FCSTD DOCUMENT  (FreeCAD 0.15R4649 (Git))
Label: PrintBot_EvolutionV1.0
License: CC-BY 3.0
LicenseURL: http://creativecommons.org/licenses/by/3.0/
objects: Part::Feature×190, Part::MultiFuse×45, Part::Cylinder×44, Sketcher::SketchObject×39, Part::Box×37, Part::Cut×34, App::DocumentObjectGroup×32, Part::Fillet×26, PartDesign::Pad×21, PartDesign::Pocket×12, Part::Chamfer×8, PartDesign::Revolution×6, Part::Compound×5, Part::Sphere×4, Part::Torus×4, Mesh::Feature×2, PartDesign::PolarPattern×1, Part::Extrusion×1, PartDesign::Mirrored×1
note: 517 computed .brp shape members not serialized (recipe doc carries the construction recipe); baked Part::Feature solids carry a one-line shape summary decoded from their .brp

FEATURE [Part::Compound] Compound  label="bottom-screws"
FEATURE [Part::Feature] Chamfer  label="shaft"
  Placement = pos=(10.55,0,41.9) rot=(0,0,1;0rad)
  shape: bbox 6 x 6 x 4.4 mm, 90 faces (baked)
FEATURE [Part::MultiFuse] Fusion  label="wires"
  Placement = pos=(20.55,0,6.35) rot=(0,0,1;0rad)
FEATURE [Part::MultiFuse] Fusion001  label="servo-1"
FEATURE [Part::Compound] Compound001  label="Servo-SM-S4303R_1"
  Links = -> [Chamfer,Fusion001,Fusion,Compound]
  Placement = pos=(9,-4,13.5) rot=(1,0,0;1.5708rad)
FEATURE [Part::MultiFuse] Fusion002  label="wires001"
  Placement = pos=(20.55,0,6.35) rot=(0,0,1;0rad)
FEATURE [Part::Compound] Compound003  label="bottom-screws001"
FEATURE [Part::MultiFuse] Fusion003  label="servo-002"
FEATURE [Part::Feature] Chamfer001  label="shaft001"
  Placement = pos=(10.55,0,41.9) rot=(0,0,1;0rad)
  shape: bbox 6 x 6 x 4.4 mm, 90 faces (baked)
FEATURE [Part::Compound] Compound002  label="Servo-SM-S4303R_2"
  Links = -> [Chamfer001,Fusion003,Fusion002,Compound003]
  Placement = pos=(9,4,13.5) rot=(-1,0,0;1.5708rad)
FEATURE [Part::Feature] Part__Feature  label="Document078"
  shape: bbox 48.01 x 1.1 x 9.213 mm, 3 faces, 0 solids (baked)
FEATURE [Part::Feature] Part__Feature001  label="Document028"
  shape: bbox 48.01 x 1.1 x 9.213 mm, 3 faces, 0 solids (baked)
FEATURE [Part::Feature] Part__Feature002  label="Document026"
  shape: bbox 48.01 x 1.1 x 9.213 mm, 3 faces, 0 solids (baked)
FEATURE [Part::Feature] Part__Feature003  label="Document025"
  shape: bbox 72.61 x 69.1 x 20.61 mm, 206 faces, 0 solids (baked)
FEATURE [Part::Feature] Part__Feature004  label="Document027"
  shape: bbox 48.01 x 1.1 x 9.213 mm, 3 faces, 0 solids (baked)
FEATURE [Part::Feature] Part__Feature005  label="Document079"
  shape: bbox 48.01 x 1.1 x 9.213 mm, 3 faces, 0 solids (baked)
FEATURE [Part::Feature] Part__Feature006  label="Document077"
  shape: bbox 48.01 x 1.1 x 9.213 mm, 3 faces, 0 solids (baked)
FEATURE [Part::Feature] Part__Feature007  label="Document080"
  shape: bbox 72.61 x 69.1 x 20.61 mm, 206 faces, 0 solids (baked)
FEATURE [Part::MultiFuse] Fusion004  label="Portapilas"
  Placement = pos=(-53,0,18) rot=(0,1,0;1.5708rad)
  Shapes = -> [Part__Feature002,Part__Feature004,Part__Feature001,Part__Feature006,Part__Feature,Part__Feature005,Part__Feature003,Part__Feature007]
FEATURE [Part::Feature] Part__Feature008  label="VRbqZUM_bloqs_Light002"
  Placement = pos=(-3.04408,-0.259919,0) rot=(0,0,-1;1.5708rad)
  shape: bbox 1.028 x 1.028 x 0.89 mm, 5 faces (baked)
FEATURE [Part::Feature] Part__Feature009  label="D2bqZUM_bloqs_Light"
  Placement = pos=(7.50008,-5.79987,0) rot=(0,0,1;3.14159rad)
  shape: bbox 1.83 x 0.8489 x 0.71 mm, 32 faces (baked)
FEATURE [Part::Feature] Part__Feature010  label="R1bqZUM_bloqs_Light"
  Placement = pos=(3.61,4.2,0) rot=(0,0,1;3.14159rad)
  shape: bbox 1.6 x 0.8 x 0.4 mm, 36 faces (baked)
FEATURE [Part::Feature] Part__Feature011  label="LDbqZUM_bloqs_Light004"
  Placement = pos=(-6.16487,-6.8001,0) rot=(0,0,-1;1.5708rad)
  shape: bbox 0.275 x 0.65 x 0.35 mm, 14 faces (baked)
FEATURE [Part::Feature] Part__Feature012  label="LDbqZUM_bloqs_Light001"
  Placement = pos=(-6.16487,-6.8001,0) rot=(0,0,-1;1.5708rad)
  shape: bbox 1 x 0.725 x 0.35 mm, 6 faces (baked)
FEATURE [Part::Feature] Part__Feature013  label="VRbqZUM_bloqs_Light"
  Placement = pos=(-3.04408,-0.259919,0) rot=(0,0,-1;1.5708rad)
  shape: bbox 1.028 x 1.028 x 0.89 mm, 5 faces (baked)
FEATURE [Part::Feature] Part__Feature014  label="R9bqZUM_bloqs_Light"
  Placement = pos=(-6.69,-5.3,0) rot=(0,0,1;3.14159rad)
  shape: bbox 1.6 x 0.8 x 0.4 mm, 36 faces (baked)
FEATURE [Part::Feature] Part__Feature015  label="R6bqZUM_bloqs_Light"
  Placement = pos=(1.91,-1.7,0) rot=(0,0,1;3.14159rad)
  shape: bbox 1.6 x 0.8 x 0.4 mm, 36 faces (baked)
FEATURE [Part::Feature] Part__Feature016  label="C3bqZUM_bloqs_Light"
  Placement = pos=(1.91,1.1,0) rot=(0,0,1;3.14159rad)
  shape: bbox 1.6 x 0.8 x 0.6 mm, 44 faces (baked)
FEATURE [Part::Feature] Part__Feature017  label="VRbqZUM_bloqs_Light006"
  Placement = pos=(-3.04408,-0.259919,0) rot=(0,0,-1;1.5708rad)
  shape: bbox 0.46 x 0.46 x 5.8 mm, 4 faces (baked)
FEATURE [Part::Feature] Part__Feature018  label="VRbqZUM_bloqs_Light007"
  Placement = pos=(-3.04408,-0.259919,0) rot=(0,0,-1;1.5708rad)
  shape: bbox 7.054 x 6.6 x 4.7 mm, 177 faces (baked)
FEATURE [Part::Feature] Part__Feature019  label="C4bqZUM_bloqs_Light"
  Placement = pos=(6.21,4.2,0) rot=(0,0,1;3.14159rad)
  shape: bbox 1.6 x 0.8 x 0.6 mm, 44 faces (baked)
FEATURE [Part::Feature] Part__Feature020  label="C1bqZUM_bloqs_Light"
  Placement = pos=(3.91,-5.1,0) rot=(0,0,1;3.14159rad)
  shape: bbox 1.6 x 0.8 x 0.6 mm, 44 faces (baked)
FEATURE [Part::Feature] Part__Feature021  label="J1bqZUM_bloqs_Light"
  Placement = pos=(-4.08502e-05,-19.573,2.98) rot=(1,0,0;1.5708rad)
  shape: bbox 10.16 x 13.59 x 10.29 mm, 129 faces (baked)
FEATURE [Part::Feature] Part__Feature022  label="VRbqZUM_bloqs_Light003"
  Placement = pos=(-3.04408,-0.259919,0) rot=(0,0,-1;1.5708rad)
  shape: bbox 1.028 x 1.028 x 0.89 mm, 5 faces (baked)
FEATURE [Part::Feature] Part__Feature023  label="LDbqZUM_bloqs_Light"
  Placement = pos=(-6.16487,-6.8001,0) rot=(0,0,-1;1.5708rad)
  shape: bbox 1.6 x 0.725 x 0.3 mm, 10 faces (baked)
FEATURE [Part::Feature] Part__Feature024  label="VRbqZUM_bloqs_Light004"
  Placement = pos=(-3.04408,-0.259919,0) rot=(0,0,-1;1.5708rad)
  shape: bbox 0.46 x 0.46 x 5.8 mm, 4 faces (baked)
FEATURE [Part::Feature] Part__Feature025  label="LDbqZUM_bloqs_Light003"
  Placement = pos=(-6.16487,-6.8001,0) rot=(0,0,-1;1.5708rad)
  shape: bbox 0.275 x 0.65 x 0.35 mm, 14 faces (baked)
FEATURE [Part::Feature] Part__Feature026  label="U2bqZUM_bloqs_Light"
  Placement = pos=(5.10492,-0.244957,0) rot=(0.57735,0.57735,0.57735;2.0944rad)
  shape: bbox 3 x 6.456 x 1.2 mm, 129 faces (baked)
FEATURE [Part::Feature] Part__Feature027  label="VRbqZUM_bloqs_Light001"
  Placement = pos=(-3.04408,-0.259919,0) rot=(0,0,-1;1.5708rad)
  shape: bbox 1.028 x 1.028 x 0.89 mm, 5 faces (baked)
FEATURE [Part::Feature] Part__Feature028  label="C2bqZUM_bloqs_Light"
  Placement = pos=(-4.21,4.2,0) rot=(0,0,1;0rad)
  shape: bbox 1.6 x 0.8 x 0.6 mm, 44 faces (baked)
FEATURE [Part::Feature] Part__Feature029  label="PCB"
  Placement = pos=(0,0,-1.6) rot=(0,0,1;0rad)
  shape: bbox 28.95 x 26.02 x 1.6 mm, 83 faces (baked)
FEATURE [Part::Feature] Part__Feature030  label="RfbbqZUM_bloqs_Light"
  Placement = pos=(7.49,-7.22,0) rot=(0,0,1;0rad)
  shape: bbox 1.6 x 0.8 x 0.4 mm, 36 faces (baked)
FEATURE [Part::Feature] Part__Feature031  label="R7bqZUM_bloqs_Light"
  Placement = pos=(1.91,-0.3,0) rot=(0,0,1;3.14159rad)
  shape: bbox 1.6 x 0.8 x 0.4 mm, 36 faces (baked)
FEATURE [Part::Feature] Part__Feature032  label="LDbqZUM_bloqs_Light002"
  Placement = pos=(-6.16487,-6.8001,0) rot=(0,0,-1;1.5708rad)
  shape: bbox 0.1601 x 0.1489 x 0.075 mm, 6 faces (baked)
FEATURE [Part::Feature] Part__Feature033  label="R5bqZUM_bloqs_Light"
  Placement = pos=(1.01,4.2,0) rot=(0,0,1;3.14159rad)
  shape: bbox 1.6 x 0.8 x 0.4 mm, 36 faces (baked)
FEATURE [Part::Feature] Part__Feature034  label="VRbqZUM_bloqs_Light005"
  Placement = pos=(-3.04408,-0.259919,0) rot=(0,0,-1;1.5708rad)
  shape: bbox 0.46 x 0.46 x 5.8 mm, 4 faces (baked)
FEATURE [Part::Feature] Part__Feature035  label="R2bqZUM_bloqs_Light"
  Placement = pos=(-1.59,4.2,0) rot=(0,0,1;3.14159rad)
  shape: bbox 1.6 x 0.8 x 0.4 mm, 36 faces (baked)
FEATURE [Part::Feature] Part__Feature036  label="RfbbqZUM_bloqs_Light001"
  Placement = pos=(7.49,-7.22,0) rot=(0,0,1;0rad)
  shape: bbox 1.6 x 0.8 x 0.4 mm, 36 faces (baked)
FEATURE [Part::Feature] Part__Feature037  label="VRbqZUM_bloqs_Light008"
  Placement = pos=(-3.04408,-0.259919,0) rot=(0,0,-1;1.5708rad)
  shape: bbox 1.028 x 1.028 x 0.89 mm, 5 faces (baked)
FEATURE [Part::Feature] Part__Feature038  label="C1bqZUM_bloqs_Light001"
  Placement = pos=(3.91,-5.1,0) rot=(0,0,1;3.14159rad)
  shape: bbox 1.6 x 0.8 x 0.6 mm, 44 faces (baked)
FEATURE [Part::Feature] Part__Feature039  label="VRbqZUM_bloqs_Light009"
  Placement = pos=(-3.04408,-0.259919,0) rot=(0,0,-1;1.5708rad)
  shape: bbox 1.028 x 1.028 x 0.89 mm, 5 faces (baked)
FEATURE [Part::Feature] Part__Feature040  label="U2bqZUM_bloqs_Light001"
  Placement = pos=(5.10492,-0.244957,0) rot=(0.57735,0.57735,0.57735;2.0944rad)
  shape: bbox 3 x 6.456 x 1.2 mm, 129 faces (baked)
FEATURE [Part::Feature] Part__Feature041  label="VRbqZUM_bloqs_Light010"
  Placement = pos=(-3.04408,-0.259919,0) rot=(0,0,-1;1.5708rad)
  shape: bbox 1.028 x 1.028 x 0.89 mm, 5 faces (baked)
FEATURE [Part::Feature] Part__Feature042  label="VRbqZUM_bloqs_Light011"
  Placement = pos=(-3.04408,-0.259919,0) rot=(0,0,-1;1.5708rad)
  shape: bbox 0.46 x 0.46 x 5.8 mm, 4 faces (baked)
FEATURE [Part::Feature] Part__Feature043  label="J1bqZUM_bloqs_Light001"
  Placement = pos=(-4.08502e-05,-19.573,2.98) rot=(1,0,0;1.5708rad)
  shape: bbox 10.16 x 13.59 x 10.29 mm, 129 faces (baked)
FEATURE [Part::Feature] Part__Feature044  label="LDbqZUM_bloqs_Light005"
  Placement = pos=(-6.16487,-6.8001,0) rot=(0,0,-1;1.5708rad)
  shape: bbox 0.275 x 0.65 x 0.35 mm, 14 faces (baked)
FEATURE [Part::Feature] Part__Feature045  label="C2bqZUM_bloqs_Light001"
  Placement = pos=(-4.21,4.2,0) rot=(0,0,1;0rad)
  shape: bbox 1.6 x 0.8 x 0.6 mm, 44 faces (baked)
FEATURE [Part::Feature] Part__Feature046  label="R1bqZUM_bloqs_Light001"
  Placement = pos=(3.61,4.2,0) rot=(0,0,1;3.14159rad)
  shape: bbox 1.6 x 0.8 x 0.4 mm, 36 faces (baked)
FEATURE [Part::Feature] Part__Feature047  label="LDbqZUM_bloqs_Light006"
  Placement = pos=(-6.16487,-6.8001,0) rot=(0,0,-1;1.5708rad)
  shape: bbox 1.6 x 0.725 x 0.3 mm, 10 faces (baked)
FEATURE [Part::Feature] Part__Feature048  label="R6bqZUM_bloqs_Light001"
  Placement = pos=(1.91,-1.7,0) rot=(0,0,1;3.14159rad)
  shape: bbox 1.6 x 0.8 x 0.4 mm, 36 faces (baked)
FEATURE [Part::Feature] Part__Feature049  label="C3bqZUM_bloqs_Light001"
  Placement = pos=(1.91,1.1,0) rot=(0,0,1;3.14159rad)
  shape: bbox 1.6 x 0.8 x 0.6 mm, 44 faces (baked)
FEATURE [Part::Feature] Part__Feature050  label="R9bqZUM_bloqs_Light001"
  Placement = pos=(-6.69,-5.3,0) rot=(0,0,1;3.14159rad)
  shape: bbox 1.6 x 0.8 x 0.4 mm, 36 faces (baked)
FEATURE [Part::Feature] Part__Feature051  label="LDbqZUM_bloqs_Light007"
  Placement = pos=(-6.16487,-6.8001,0) rot=(0,0,-1;1.5708rad)
  shape: bbox 0.275 x 0.65 x 0.35 mm, 14 faces (baked)
FEATURE [Part::Feature] Part__Feature052  label="R2bqZUM_bloqs_Light001"
  Placement = pos=(-1.59,4.2,0) rot=(0,0,1;3.14159rad)
  shape: bbox 1.6 x 0.8 x 0.4 mm, 36 faces (baked)
FEATURE [Part::Feature] Part__Feature053  label="VRbqZUM_bloqs_Light012"
  Placement = pos=(-3.04408,-0.259919,0) rot=(0,0,-1;1.5708rad)
  shape: bbox 7.054 x 6.6 x 4.7 mm, 177 faces (baked)
FEATURE [Part::Feature] Part__Feature054  label="C4bqZUM_bloqs_Light001"
  Placement = pos=(6.21,4.2,0) rot=(0,0,1;3.14159rad)
  shape: bbox 1.6 x 0.8 x 0.6 mm, 44 faces (baked)
FEATURE [Part::Feature] Part__Feature055  label="R5bqZUM_bloqs_Light001"
  Placement = pos=(1.01,4.2,0) rot=(0,0,1;3.14159rad)
  shape: bbox 1.6 x 0.8 x 0.4 mm, 36 faces (baked)
FEATURE [Part::Feature] Part__Feature056  label="VRbqZUM_bloqs_Light013"
  Placement = pos=(-3.04408,-0.259919,0) rot=(0,0,-1;1.5708rad)
  shape: bbox 0.46 x 0.46 x 5.8 mm, 4 faces (baked)
FEATURE [Part::Feature] Part__Feature057  label="PCB001"
  Placement = pos=(0,0,-1.6) rot=(0,0,1;0rad)
  shape: bbox 28.95 x 26.02 x 1.6 mm, 83 faces (baked)
FEATURE [Part::Feature] Part__Feature058  label="LDbqZUM_bloqs_Light008"
  Placement = pos=(-6.16487,-6.8001,0) rot=(0,0,-1;1.5708rad)
  shape: bbox 0.1601 x 0.1489 x 0.075 mm, 6 faces (baked)
FEATURE [Part::Feature] Part__Feature059  label="VRbqZUM_bloqs_Light014"
  Placement = pos=(-3.04408,-0.259919,0) rot=(0,0,-1;1.5708rad)
  shape: bbox 0.46 x 0.46 x 5.8 mm, 4 faces (baked)
FEATURE [Part::Feature] Part__Feature060  label="VRbqZUM_bloqs_Light015"
  Placement = pos=(-3.04408,-0.259919,0) rot=(0,0,-1;1.5708rad)
  shape: bbox 1.028 x 1.028 x 0.89 mm, 5 faces (baked)
FEATURE [Part::Feature] Part__Feature061  label="LDbqZUM_bloqs_Light009"
  Placement = pos=(-6.16487,-6.8001,0) rot=(0,0,-1;1.5708rad)
  shape: bbox 1 x 0.725 x 0.35 mm, 6 faces (baked)
FEATURE [Part::Feature] Part__Feature062  label="R7bqZUM_bloqs_Light001"
  Placement = pos=(1.91,-0.3,0) rot=(0,0,1;3.14159rad)
  shape: bbox 1.6 x 0.8 x 0.4 mm, 36 faces (baked)
FEATURE [Part::Feature] Part__Feature063  label="D2bqZUM_bloqs_Light001"
  Placement = pos=(7.50008,-5.79987,0) rot=(0,0,1;3.14159rad)
  shape: bbox 1.83 x 0.8489 x 0.71 mm, 32 faces (baked)
FEATURE [Part::Feature] Part__Feature064  label="ZUM_PCB"
  Placement = pos=(-31,-26.5,50) rot=(0,0,1;0rad)
  shape: bbox 68.6 x 53.36 x 1.91 mm, 540 faces (baked)
FEATURE [Part::Feature] Part__Feature068  label="J1"
  Placement = pos=(-4.08502e-05,-19.573,2.98) rot=(1,0,0;1.5708rad)
  shape: bbox 10.16 x 13.59 x 10.29 mm, 129 faces (baked)
FEATURE [Part::Feature] Part__Feature069  label="BUZ"
  Placement = pos=(-4.27575e-05,5.30009,0) rot=(0,0.707107,0.707107;3.14159rad)
  shape: bbox 12.81 x 12.81 x 13.08 mm, 24 faces (baked)
FEATURE [Part::Feature] Part__Feature070  label="PCB002"
  Placement = pos=(0,0,-1.6) rot=(0,0,1;0rad)
  shape: bbox 28.95 x 26.02 x 1.6 mm, 78 faces (baked)
FEATURE [Mesh::Feature] Miniservo
  Placement = pos=(53,5.65,3) rot=(0,0,1;0rad)
FEATURE [Part::MultiFuse] Fusion007  label="Zumbador_PCB"
  Placement = pos=(20.5,-5,35) rot=(0,0,1;1.5708rad)
  Shapes = -> [Part__Feature068,Part__Feature069,Part__Feature070,Miniservo]
FEATURE [Part::Box] Box001  label="Cuerpo_Madre"
  Height = 30
  Length = 62
  Placement = pos=(-22,-33,3) rot=(0,0,1;0rad)
  Width = 66
FEATURE [Part::Feature] Part__Feature078  label="Ultrasonido_BAT"
  Placement = pos=(70,0,43.5) rot=(0.57735,-0.57735,0.57735;4.18879rad)
  shape: bbox 18.72 x 56 x 27.52 mm, 81 faces (baked)
FEATURE [Part::Box] Box  label="Cuerpo_vaciado_X"
  Height = 27
  Length = 62
  Placement = pos=(-22,-25,3) rot=(0,0,1;0rad)
  Width = 50
FEATURE [Part::Box] Box002  label="Hueco_Cuerpo_Tuerca_4"
  Height = 6
  Length = 62
  Placement = pos=(-22,27.5,5.75) rot=(0,0,1;0rad)
  Width = 3
FEATURE [Part::Box] Box003  label="Hueco_Cuerpo_Tuerca_1"
  Height = 6
  Length = 62
  Placement = pos=(-22,27.55,15.75) rot=(0,0,1;0rad)
  Width = 3
FEATURE [Part::Box] Box004  label="Hueco_Cuerpo_Tuerca_2"
  Height = 6
  Length = 62
  Placement = pos=(-22,-30.5,15.75) rot=(0,0,1;0rad)
  Width = 3
FEATURE [Part::Box] Box005  label="Hueco_Cuerpo_Tuerca_3"
  Height = 6
  Length = 62
  Placement = pos=(-22,-30.55,5.75) rot=(0,0,1;0rad)
  Width = 3
FEATURE [Part::Box] Box006  label="Cuerpo_Vaciado_Y"
  Height = 22.5
  Length = 42
  Placement = pos=(-12,-33,2) rot=(0,0,1;0rad)
  Width = 66
FEATURE [Part::Cylinder] Cylinder  label="Taladro_Tornillo_Servo_2"
  Angle = 360
  Height = 8
  Placement = pos=(-16.2,25,8.4) rot=(-1,0,0;1.5708rad)
  Radius = 1.75
FEATURE [Part::Cylinder] Cylinder001  label="Taladro_Tornillo_Servo_1"
  Angle = 360
  Height = 12
  Placement = pos=(-16.2,21,18.6) rot=(-1,0,0;1.5708rad)
  Radius = 1.75
FEATURE [Part::Cylinder] Cylinder002  label="Taladro_Tornillo_Servo_3"
  Angle = 360
  Height = 9
  Placement = pos=(34.2,24,18.6) rot=(-1,0,0;1.5708rad)
  Radius = 1.75
FEATURE [Part::Cylinder] Cylinder003  label="Taladro_Tornillos_Servo_3"
  Angle = 360
  Height = 8
  Placement = pos=(34.2,25,8.4) rot=(-1,0,0;1.5708rad)
  Radius = 1.75
FEATURE [Part::Feature] Part__Feature080  label="TornilloM3x8_Servo1"
  Placement = pos=(34,-35.5,8.5) rot=(-1,0,0;1.5708rad)
  shape: bbox 5.953 x 11 x 5.953 mm, 174 faces (baked)
FEATURE [Part::Feature] Part__Feature081  label="TornilloM3x8_Servo2"
  Placement = pos=(-16,-35.5,18.5) rot=(-1,0,0;1.5708rad)
  shape: bbox 5.953 x 11 x 5.953 mm, 174 faces (baked)
FEATURE [Part::Feature] Part__Feature082  label="TornilloM3x8_Servo3"
  Placement = pos=(-16,35.5,8.5) rot=(1,0,0;1.5708rad)
  shape: bbox 5.953 x 11 x 5.953 mm, 174 faces (baked)
FEATURE [Part::Feature] Part__Feature083  label="TornilloM3x8_Servo4"
  Placement = pos=(-16,35.5,18.5) rot=(1,0,0;1.5708rad)
  shape: bbox 5.953 x 11 x 5.953 mm, 174 faces (baked)
FEATURE [Part::Cylinder] Cylinder005  label="Placa_separador_hueco"
  Angle = 360
  Height = 16
  Placement = pos=(-17,-24,33) rot=(0,0,1;0rad)
  Radius = 1.75
FEATURE [Part::Feature] Part__Feature088  label="TornilloM3x8_Servo5"
  Placement = pos=(34,35.5,18.5) rot=(1,0,0;1.5708rad)
  shape: bbox 5.953 x 11 x 5.953 mm, 174 faces (baked)
FEATURE [Part::Feature] Part__Feature089  label="TornilloM3x8_Servo6"
  Placement = pos=(34,35.5,8.5) rot=(1,0,0;1.5708rad)
  shape: bbox 5.953 x 11 x 5.953 mm, 174 faces (baked)
FEATURE [Part::Feature] Part__Feature090  label="TornilloM3x8_Servo7"
  Placement = pos=(34,-35.5,18.5) rot=(-1,0,0;1.5708rad)
  shape: bbox 5.953 x 11 x 5.953 mm, 174 faces (baked)
FEATURE [Part::Feature] Part__Feature091  label="TornilloM3x8_Servo8"
  Placement = pos=(-16,-35.5,8.5) rot=(-1,0,0;1.5708rad)
  shape: bbox 5.953 x 11 x 5.953 mm, 174 faces (baked)
FEATURE [Part::Feature] Part__Feature092  label="TornilloM3x8_Zumbador_2"
  Placement = pos=(20.5,-15,35) rot=(1,0,0;3.14159rad)
  shape: bbox 5.953 x 5.953 x 11 mm, 174 faces (baked)
FEATURE [Part::Feature] Part__Feature093  label="TornilloM3x8_Zumbador_1"
  Placement = pos=(20.5,5,35) rot=(1,0,0;3.14159rad)
  shape: bbox 5.953 x 5.953 x 11 mm, 174 faces (baked)
FEATURE [Part::Feature] Part__Feature098  label="TuercaM3_Zumbador_2"
  Placement = pos=(20.5,5,30) rot=(0,0,1;0rad)
  shape: bbox 6.929 x 6.929 x 2.801 mm, 56 faces (baked)
FEATURE [Part::Feature] Part__Feature099  label="TuercaM3_Zumbador_1"
  Placement = pos=(20.5,-15,30) rot=(0,0,1;0rad)
  shape: bbox 6.929 x 6.929 x 2.801 mm, 56 faces (baked)
FEATURE [Part::Feature] Part__Feature100  label="TornilloM3x8_LDR1"
  Placement = pos=(83.5,-37.9,5) rot=(1,0,0;3.14159rad)
  shape: bbox 5.953 x 5.953 x 11 mm, 174 faces (baked)
FEATURE [Part::MultiFuse] Fusion005  label="Sensor_IR_1"
  Placement = pos=(77,6,5) rot=(0,0,-1;1.5708rad)
  Shapes = -> [Part__Feature026,Part__Feature032,Part__Feature029,Part__Feature019,Part__Feature015,Part__Feature034,Part__Feature024,Part__Feature023,Part__Feature009,Part__Feature010,Part__Feature025,Part__Feature035,Part__Feature016,Part__Feature030,Part__Feature014,Part__Feature020,Part__Feature012,Part__Feature031,Part__Feature027,Part__Feature008,Part__Feature017,Part__Feature013,Part__Feature022,+5 more]
FEATURE [Part::MultiFuse] Fusion006  label="Sensor_IR_2"
  Placement = pos=(77,-6,5) rot=(0,0,-1;1.5708rad)
  Shapes = -> [Part__Feature040,Part__Feature058,Part__Feature057,Part__Feature054,Part__Feature048,Part__Feature059,Part__Feature042,Part__Feature047,Part__Feature063,Part__Feature046,Part__Feature051,Part__Feature052,Part__Feature049,Part__Feature036,Part__Feature050,Part__Feature038,Part__Feature061,Part__Feature062,Part__Feature041,Part__Feature037,Part__Feature056,Part__Feature039,Part__Feature060,+5 more]
FEATURE [Part::Feature] Part__Feature101  label="TornilloM3x8_LDR2"
  Placement = pos=(83.5,-17.9,5) rot=(1,0,0;3.14159rad)
  shape: bbox 5.953 x 5.953 x 11 mm, 174 faces (baked)
FEATURE [Part::Feature] Part__Feature102  label="TornilloM3x8_LDR3"
  Placement = pos=(83.5,17.9,5) rot=(1,0,0;3.14159rad)
  shape: bbox 5.953 x 5.953 x 11 mm, 174 faces (baked)
FEATURE [Part::Feature] Part__Feature103  label="TornilloM3x8_LDR4"
  Placement = pos=(83.5,37.9,5) rot=(1,0,0;3.14159rad)
  shape: bbox 5.953 x 5.953 x 11 mm, 174 faces (baked)
FEATURE [Part::Feature] Part__Feature104  label="TornilloM3x8_IR1"
  Placement = pos=(98.9,-15.9,5) rot=(1,0,0;3.14159rad)
  shape: bbox 5.953 x 5.953 x 11 mm, 174 faces (baked)
FEATURE [Part::Feature] Part__Feature105  label="TornilloM3x8_IR2"
  Placement = pos=(98.9,16.1,5) rot=(1,0,0;3.14159rad)
  shape: bbox 5.953 x 5.953 x 11 mm, 174 faces (baked)
FEATURE [Part::Feature] Part__Feature106  label="TuercaM3_Servo1"
  Placement = pos=(-16,27.65,8.75) rot=(1,0,0;1.5708rad)
  shape: bbox 6.929 x 2.801 x 6.929 mm, 56 faces (baked)
FEATURE [Part::Feature] Part__Feature107  label="TuercaM3_Servo2"
  Placement = pos=(-16,27.65,18.75) rot=(1,0,0;1.5708rad)
  shape: bbox 6.929 x 2.801 x 6.929 mm, 56 faces (baked)
FEATURE [Part::Feature] Part__Feature108  label="TuercaM3_Servo3"
  Placement = pos=(-16,-30.35,8.75) rot=(1,0,0;1.5708rad)
  shape: bbox 6.929 x 2.801 x 6.929 mm, 56 faces (baked)
FEATURE [Part::Feature] Part__Feature109  label="TuercaM3_Servo4"
  Placement = pos=(-16,-30.35,18.75) rot=(1,0,0;1.5708rad)
  shape: bbox 6.929 x 2.801 x 6.929 mm, 56 faces (baked)
FEATURE [Part::Feature] Part__Feature110  label="TuercaM3_Servo5"
  Placement = pos=(34,27.65,8.75) rot=(1,0,0;1.5708rad)
  shape: bbox 6.929 x 2.801 x 6.929 mm, 56 faces (baked)
FEATURE [Part::Feature] Part__Feature111  label="TuercaM3_Servo6"
  Placement = pos=(34,27.65,18.75) rot=(1,0,0;1.5708rad)
  shape: bbox 6.929 x 2.801 x 6.929 mm, 56 faces (baked)
FEATURE [Part::Feature] Part__Feature112  label="TuercaM3_Servo7"
  Placement = pos=(34,-30.35,18.75) rot=(1,0,0;1.5708rad)
  shape: bbox 6.929 x 2.801 x 6.929 mm, 56 faces (baked)
FEATURE [Part::Feature] Part__Feature113  label="TuercaM3_Servo8"
  Placement = pos=(34,-30.35,8.75) rot=(1,0,0;1.5708rad)
  shape: bbox 6.929 x 2.801 x 6.929 mm, 56 faces (baked)
FEATURE [Part::Feature] Part__Feature115  label="TuercaM3_LDR1"
  Placement = pos=(75.5,38,0) rot=(0,0,1;0rad)
  shape: bbox 6.929 x 6.929 x 2.801 mm, 56 faces (baked)
FEATURE [Part::Feature] Part__Feature116  label="TuercaM3_LDR3"
  Placement = pos=(75.5,-18,0) rot=(0,0,1;0rad)
  shape: bbox 6.929 x 6.929 x 2.801 mm, 56 faces (baked)
FEATURE [Part::Feature] Part__Feature117  label="TuercaM3_LDR4"
  Placement = pos=(75.5,-38,0) rot=(0,0,1;0rad)
  shape: bbox 6.929 x 6.929 x 2.801 mm, 56 faces (baked)
FEATURE [Part::Feature] Part__Feature118  label="TuercaM3_IR1"
  Placement = pos=(91,-16,0) rot=(0,0,1;0rad)
  shape: bbox 6.929 x 6.929 x 2.801 mm, 56 faces (baked)
FEATURE [Part::Feature] Part__Feature119  label="TuercaM3_IR2"
  Placement = pos=(91,16,0) rot=(0,0,1;0rad)
  shape: bbox 6.929 x 6.929 x 2.801 mm, 56 faces (baked)
FEATURE [App::DocumentObjectGroup] Group008  label="Sensores_Tornillos"
  Group = -> [Part__Feature100,Part__Feature101,Part__Feature102,Part__Feature103,Part__Feature104,Part__Feature105]
FEATURE [Part::Feature] Part__Feature122  label="final-screw-R1"
  Placement = pos=(19.5,-54.5,13.5) rot=(1,0,0;1.5708rad)
  shape: bbox 7 x 15.94 x 7 mm, 34 faces (baked)
FEATURE [Part::Feature] Part__Feature123  label="final-screw-R2"
  Placement = pos=(19.5,54.5,13.5) rot=(-1,0,0;1.5708rad)
  shape: bbox 7 x 15.94 x 7 mm, 34 faces (baked)
FEATURE [App::DocumentObjectGroup] Group014  label="Servos_Tornillos"
  Group = -> [Part__Feature080,Part__Feature081,Part__Feature082,Part__Feature083,Part__Feature088,Part__Feature089,Part__Feature090,Part__Feature091]
FEATURE [App::DocumentObjectGroup] Group015  label="Tuercas_servo"
  Group = -> [Part__Feature106,Part__Feature107,Part__Feature108,Part__Feature109,Part__Feature110,Part__Feature111,Part__Feature112,Part__Feature113]
FEATURE [App::DocumentObjectGroup] Group013  label="Servos"
  Group = -> [Group014,Group015,Compound001,Compound002]
FEATURE [App::DocumentObjectGroup] Group018  label="Tornillos_Zumbador"
  Group = -> [Part__Feature093,Part__Feature092]
FEATURE [App::DocumentObjectGroup] Group019  label="Tuercas_Zumbador"
  Group = -> [Part__Feature099,Part__Feature098]
FEATURE [App::DocumentObjectGroup] Group017  label="Zumbador"
  Group = -> [Fusion007,Group018,Group019]
FEATURE [App::DocumentObjectGroup] Group020  label="Ruedas_Tornillos"
  Group = -> [Part__Feature122,Part__Feature123]
FEATURE [Mesh::Feature] Miniservo001
  Placement = pos=(61,6,3) rot=(0,0,1;0rad)
FEATURE [Part::Box] Box013  label="Ultrasonido_cuerpo"
  Height = 2
  Length = 12
  Placement = pos=(68,-27.9,31) rot=(0,-1,0;1.5708rad)
  Width = 56
FEATURE [Part::Feature] Part__Feature128  label="TornilloM3x8_Ultrasonido1"
  Placement = pos=(71.5,-24.9,43.5) rot=(0,-1,0;1.5708rad)
  shape: bbox 11 x 5.953 x 5.953 mm, 174 faces (baked)
FEATURE [Part::Feature] Part__Feature129  label="TornilloM3x8_Ultrasonido2"
  Placement = pos=(71.5,24.9,43.5) rot=(0,-1,0;1.5708rad)
  shape: bbox 11 x 5.953 x 5.953 mm, 174 faces (baked)
FEATURE [Part::Feature] Part__Feature130  label="TuercaM3_Ultrasonido1"
  Placement = pos=(66,-25,43.5) rot=(0,1,0;1.5708rad)
  shape: bbox 2.801 x 6.929 x 6.929 mm, 56 faces (baked)
FEATURE [Part::Feature] Part__Feature131  label="TuercaM3_Ultrasonido2"
  Placement = pos=(66,25,43.5) rot=(0,1,0;1.5708rad)
  shape: bbox 2.801 x 6.929 x 6.929 mm, 56 faces (baked)
FEATURE [Part::Feature] Part__Feature133  label="Shaft-screw-final-005"
  Placement = pos=(61,0,27.5) rot=(0,0,1;0rad)
  shape: bbox 4.864 x 4.864 x 9.65 mm, 49 faces (baked)
FEATURE [Part::Box] Box015  label="Brazo_Miniservo_2"
  Height = 2.5
  Length = 13
  Placement = pos=(50,-108.5,16) rot=(0,0,1;0rad)
  Width = 4.9
FEATURE [Part::Box] Box016  label="Sujeta_miniservo_cuerpo"
  Height = 20
  Length = 18
  Placement = pos=(45,-138,1) rot=(0,0,1;0rad)
  Width = 35.9
FEATURE [Part::Cylinder] Cylinder014  label="Orificio_tornilloM3_Miniservo_1"
  Angle = 360
  Height = 20
  Placement = pos=(48,-132.8,1) rot=(0,0,1;0rad)
  Radius = 1.9
FEATURE [Part::Cylinder] Cylinder015  label="Orificio_tornilloM3_Miniservo_2"
  Angle = 360
  Height = 20
  Placement = pos=(48,-107.2,1) rot=(0,0,1;0rad)
  Radius = 1.9
FEATURE [Part::Feature] Part__Feature135  label="Shaft-screw-final-007"
  Placement = pos=(61,-8,14.5) rot=(0,0,1;0rad)
  shape: bbox 4.864 x 4.864 x 9.65 mm, 49 faces (baked)
FEATURE [Part::Feature] Part__Feature136  label="Shaft-screw-final-008"
  Placement = pos=(61,20,14.5) rot=(0,0,1;0rad)
  shape: bbox 4.864 x 4.864 x 9.65 mm, 49 faces (baked)
FEATURE [Part::Feature] Part__Feature139  label="TuercaM3_Ultrasonido3"
  Placement = pos=(52,19,0) rot=(0,0,1;0rad)
  shape: bbox 6.929 x 6.929 x 2.801 mm, 56 faces (baked)
FEATURE [Part::Feature] Part__Feature140  label="TuercaM3_Ultrasonido4"
  Placement = pos=(52,-7,0) rot=(0,0,1;0rad)
  shape: bbox 6.929 x 6.929 x 2.801 mm, 56 faces (baked)
FEATURE [App::DocumentObjectGroup] Group022  label="Ultrasonidos_Tuercas"
  Group = -> [Part__Feature131,Part__Feature130,Part__Feature139,Part__Feature140]
FEATURE [Part::Box] Box017  label="Porta-Portapilas_Madre"
  Height = 60
  Length = 26
  Placement = pos=(-57,-29,-13) rot=(0,0,1;0rad)
  Width = 58
FEATURE [Part::Box] Box018  label="Hueco_portapilas"
  Height = 55
  Length = 26
  Placement = pos=(-54,-25.5,-10.5) rot=(0,0,1;0rad)
  Width = 51
FEATURE [Sketcher::SketchObject] Sketch014  label="Portapilas_rueda_loca"
  Placement = pos=(-46.5,0,0) rot=(0.57735,-0.57735,-0.57735;2.0944rad)
  sketch-geometry (6):
    g0: LineSegment [constr] StartX=0 StartY=0 StartZ=0 EndX=0 EndY=-13 EndZ=0
    g1: ArcOfCircle CenterX=0 CenterY=-16.7163 CenterZ=0 NormalX=0 NormalY=0 NormalZ=1 Radius=3.7 StartAngle=3.87448 EndAngle=5.55029
    g2: ArcOfCircle CenterX=17.6149 CenterY=-32.5721 CenterZ=0 NormalX=0 NormalY=0 NormalZ=1 Radius=20 StartAngle=1.77802 EndAngle=2.4087
    g3: ArcOfCircle CenterX=-17.6149 CenterY=-32.5721 CenterZ=0 NormalX=0 NormalY=0 NormalZ=1 Radius=20 StartAngle=0.73289 EndAngle=1.36357
    g4: LineSegment [constr] StartX=-2.75 StartY=-19.1917 StartZ=0 EndX=2.75 EndY=-19.1917 EndZ=0
    g5: LineSegment StartX=-13.5 StartY=-13 StartZ=0 EndX=13.5 EndY=-13 EndZ=0
  constraints (19):
    c: Coincident(g0,g-1)
    c: Vertical(g0)
    c: DistanceY(g0) = -13
    c: PointOnObject(g1,g-2)
    c: Coincident(g2,g1)
    c: Coincident(g4,g1)
    c: Horizontal(g4)
    c: Coincident(g1,g3)
    c: Symmetric(g3,g2,g0)
    c: Coincident(g4,g1)
    c: Tangent(g1,g3)
    c: Coincident(g5,g3)
    c: Coincident(g5,g2)
    c: DistanceX(g5) = 27
    c: PointOnObject(g0,g5)
    c: DistanceX(g4) = 5.5
    c: Radius(g3) = 20
    c: Equal(g2,g3)
    c: Radius(g1) = 3.7
FEATURE [PartDesign::Pad] Pad002  label="[Extrusion]_Rueda_Loca"
  Length = 5
  Length2 = 100
  Placement = pos=(-46.5,0,0) rot=(0.57735,-0.57735,-0.57735;2.0944rad)
  Reversed = true
  Sketch = -> Sketch014
  Type = 0
FEATURE [Sketcher::SketchObject] Sketch015  label="[Croquis]_Rueda_Loca_para_revolucion_1"
  Placement = pos=(-46.5,0,-13) rot=(0.57735,-0.57735,-0.57735;2.0944rad)
  sketch-geometry (5):
    g0: ArcOfCircle CenterX=0 CenterY=-3.71632 CenterZ=0 NormalX=0 NormalY=0 NormalZ=1 Radius=3.7 StartAngle=3.87448 EndAngle=5.55029
    g1: ArcOfCircle CenterX=17.6149 CenterY=-19.5721 CenterZ=0 NormalX=0 NormalY=0 NormalZ=1 Radius=20 StartAngle=1.77802 EndAngle=2.4087
    g2: ArcOfCircle CenterX=-17.6149 CenterY=-19.5721 CenterZ=0 NormalX=0 NormalY=0 NormalZ=1 Radius=20 StartAngle=0.732891 EndAngle=1.36357
    g3: LineSegment [constr] StartX=-2.75 StartY=-6.19169 StartZ=0 EndX=2.75 EndY=-6.19169 EndZ=0
    g4: LineSegment StartX=-13.5 StartY=0 StartZ=0 EndX=13.5 EndY=0 EndZ=0
  constraints (17):
    c: PointOnObject(g0,g-2)
    c: Coincident(g1,g0)
    c: Coincident(g3,g0)
    c: Horizontal(g3)
    c: Coincident(g0,g2)
    c: Coincident(g3,g0)
    c: Tangent(g0,g2)
    c: DistanceX(g3) = 5.5
    c: Radius(g2) = 20
    c: Equal(g1,g2)
    c: Radius(g0) = 3.7
    c: Coincident(g4,g2)
    c: Coincident(g4,g1)
    c: DistanceX(g4) = 27
    c: PointOnObject(g2,g-1)
    c: PointOnObject(g1,g-1)
    c: Symmetric(g2,g1,g-2)
FEATURE [PartDesign::Revolution] Revolution  label="[Revolucion]_Rueda_Loca_2"
  Angle = 90
  Axis = (0,-1,0)
  Base = (-46.5,0,-13)
  Placement = pos=(-46.5,0,-13) rot=(0.57735,-0.57735,-0.57735;2.0944rad)
  ReferenceAxis = -> Sketch015 [H_Axis]
  Reversed = true
  Sketch = -> Sketch015
FEATURE [Sketcher::SketchObject] Sketch016  label="[Croquis]_Rueda_Loca_para_revolucion_2"
  Placement = pos=(-41.5,0,-13) rot=(0.57735,-0.57735,-0.57735;2.0944rad)
  sketch-geometry (5):
    g0: ArcOfCircle CenterX=0 CenterY=-3.71632 CenterZ=0 NormalX=0 NormalY=0 NormalZ=1 Radius=3.7 StartAngle=3.87448 EndAngle=5.55029
    g1: ArcOfCircle CenterX=17.6149 CenterY=-19.5721 CenterZ=0 NormalX=0 NormalY=0 NormalZ=1 Radius=20 StartAngle=1.77802 EndAngle=2.4087
    g2: ArcOfCircle CenterX=-17.6149 CenterY=-19.5721 CenterZ=0 NormalX=0 NormalY=0 NormalZ=1 Radius=20 StartAngle=0.732891 EndAngle=1.36357
    g3: LineSegment [constr] StartX=-2.75 StartY=-6.19169 StartZ=0 EndX=2.75 EndY=-6.19169 EndZ=0
    g4: LineSegment StartX=-13.5 StartY=0 StartZ=0 EndX=13.5 EndY=-1e-12 EndZ=0
  constraints (17):
    c: PointOnObject(g0,g-2)
    c: Coincident(g1,g0)
    c: Coincident(g3,g0)
    c: Horizontal(g3)
    c: Coincident(g0,g2)
    c: Coincident(g3,g0)
    c: Tangent(g0,g2)
    c: DistanceX(g3) = 5.5
    c: Radius(g2) = 20
    c: Equal(g1,g2)
    c: Radius(g0) = 3.7
    c: Coincident(g4,g2)
    c: Coincident(g4,g1)
    c: DistanceX(g4) = 27
    c: PointOnObject(g2,g-1)
    c: PointOnObject(g1,g-1)
    c: Symmetric(g2,g1,g-2)
FEATURE [PartDesign::Revolution] Revolution001  label="[Revolucion]_Rueda_Loca_1"
  Angle = 90
  Axis = (0,-1,0)
  Base = (-41.5,0,-13)
  Placement = pos=(-41.5,0,-13) rot=(0.57735,-0.57735,-0.57735;2.0944rad)
  ReferenceAxis = -> Sketch016 [H_Axis]
  Sketch = -> Sketch016
FEATURE [Part::Sphere] Sphere  label="Porta-Portapilas_Hueco_Dedo_1"
  Angle1 = -90
  Angle2 = 90
  Angle3 = 360
  Placement = pos=(-47,35,22) rot=(0,0,1;0rad)
  Radius = 9
FEATURE [Part::Sphere] Sphere001  label="Porta-Portapilas_Hueco_Dedo_2"
  Angle1 = -90
  Angle2 = 90
  Angle3 = 360
  Placement = pos=(-47,-35,22) rot=(0,0,1;0rad)
  Radius = 9
FEATURE [Part::MultiFuse] Fusion017  label="[Union]_Porta-Portapilas_Dedo"
  Placement = pos=(0,0,2) rot=(0,0,1;0rad)
  Shapes = -> [Sphere,Sphere001]
FEATURE [Sketcher::SketchObject] Sketch018  label="[Croquis]_Base"
  sketch-geometry (32):
    g0: LineSegment StartX=-57 StartY=-29.5 StartZ=0 EndX=-57 EndY=-42.2633 EndZ=0
    g1: ArcOfCircle CenterX=56 CenterY=10.5824 CenterZ=0 NormalX=0 NormalY=0 NormalZ=1 Radius=45.4176 StartAngle=1.05094 EndAngle=1.5708
    g2: LineSegment StartX=78.5613 StartY=50 StartZ=0 EndX=99.5269 EndY=38 EndZ=0
    g3: LineSegment StartX=115 StartY=15 StartZ=0 EndX=115 EndY=-15 EndZ=0
    g4: ArcOfCircle CenterX=56 CenterY=-10.5824 CenterZ=0 NormalX=0 NormalY=0 NormalZ=1 Radius=45.4176 StartAngle=4.71239 EndAngle=5.23224
    g5: LineSegment StartX=78.5613 StartY=-50 StartZ=0 EndX=99.5269 EndY=-38 EndZ=0
    g6: LineSegment StartX=-33 StartY=56 StartZ=0 EndX=-17 EndY=56 EndZ=0
    g7: LineSegment StartX=-17 StartY=56 StartZ=0 EndX=-17 EndY=44 EndZ=0
    g8: LineSegment StartX=-17 StartY=44 StartZ=0 EndX=56 EndY=44 EndZ=0
    g9: LineSegment StartX=56 StartY=56 StartZ=0 EndX=56 EndY=44 EndZ=0
    g10: LineSegment StartX=-33 StartY=-56 StartZ=0 EndX=-17 EndY=-56 EndZ=0
    g11: LineSegment StartX=-17 StartY=-56 StartZ=0 EndX=-17 EndY=-44 EndZ=0
    g12: LineSegment StartX=-17 StartY=-44 StartZ=0 EndX=56 EndY=-44 EndZ=0
    g13: LineSegment StartX=56 StartY=-44 StartZ=0 EndX=56 EndY=-56 EndZ=0
    g14: LineSegment [constr] StartX=-23 StartY=56 StartZ=0 EndX=-23 EndY=0 EndZ=0
    g15: LineSegment [constr] StartX=0 StartY=0 StartZ=0 EndX=115 EndY=0 EndZ=0
    g16: LineSegment [constr] StartX=-17 StartY=44 StartZ=0 EndX=-23 EndY=44 EndZ=0
    g17: LineSegment [constr] StartX=-23 StartY=0 StartZ=0 EndX=0 EndY=0 EndZ=0
    g18: LineSegment [constr] StartX=78.5613 StartY=50 StartZ=0 EndX=78.5613 EndY=0 EndZ=0
    g19: LineSegment [constr] StartX=99.5269 StartY=38 StartZ=0 EndX=99.5269 EndY=0 EndZ=0
    g20: LineSegment StartX=-57 StartY=42.2633 StartZ=0 EndX=-57 EndY=29.5 EndZ=0
    g21: LineSegment StartX=-57 StartY=29.5 StartZ=0 EndX=-29 EndY=29.5 EndZ=0
    g22: LineSegment StartX=-57 StartY=-29.5 StartZ=0 EndX=-29 EndY=-29.5 EndZ=0
    g23: LineSegment StartX=-29 StartY=29.5 StartZ=0 EndX=-29 EndY=-29.5 EndZ=0
    g24: LineSegment [constr] StartX=-29 StartY=0 StartZ=0 EndX=0 EndY=0 EndZ=0
    g25: LineSegment [constr] StartX=0 StartY=0 StartZ=0 EndX=115 EndY=0 EndZ=0
    g26: LineSegment StartX=99.5269 StartY=-38 StartZ=0 EndX=99.5269 EndY=-23.8562 EndZ=0
    g27: LineSegment StartX=99.5269 StartY=-23.8562 StartZ=0 EndX=115 EndY=-15 EndZ=0
    g28: LineSegment StartX=99.5269 StartY=38 StartZ=0 EndX=99.5269 EndY=23.8562 EndZ=0
    g29: LineSegment StartX=99.5269 StartY=23.8562 StartZ=0 EndX=115 EndY=15 EndZ=0
    g30: LineSegment StartX=-57 StartY=-42.2633 StartZ=0 EndX=-33 EndY=-56 EndZ=0
    g31: LineSegment StartX=-57 StartY=42.2633 StartZ=0 EndX=-33 EndY=56 EndZ=0
  constraints (95):
    c: Vertical(g0)
    c: Coincident(g2,g1)
    c: Vertical(g3)
    c: Coincident(g5,g4)
    c: Horizontal(g6)
    c: Coincident(g7,g6)
    c: Vertical(g7)
    c: Coincident(g8,g7)
    c: Horizontal(g8)
    c: Coincident(g9,g1)
    c: Coincident(g9,g8)
    c: Vertical(g9)
    c: Horizontal(g10)
    c: Coincident(g11,g10)
    c: Vertical(g11)
    c: Coincident(g12,g11)
    c: Horizontal(g12)
    c: Coincident(g13,g12)
    c: Coincident(g13,g4)
    c: Vertical(g13)
    c: Equal(g6,g10)
    c: Equal(g8,g12)
    c: Equal(g9,g13)
    c: Equal(g7,g11)
    c: Equal(g13,g11)
    c: Equal(g4,g1)
    c: Equal(g2,g5)
    c: Tangent(g4,g5)
    c: DistanceX(g12) = 73
    c: Perpendicular(g4,g13)
    c: DistanceY(g3) = -30
    c: Symmetric(g3,g3,g-1)
    c: DistanceY(g7) = -12
    c: PointOnObject(g14,g6)
    c: Vertical(g14)
    c: DistanceY(g14) = -56
    c: Coincident(g15,g-1)
    c: PointOnObject(g15,g3)
    c: Horizontal(g15)
    c: DistanceX(g15) = 115
    c: Coincident(g16,g7)
    c: PointOnObject(g16,g14)
    c: Horizontal(g16)
    c: DistanceX(g16) = -6
    c: Coincident(g17,g14)
    c: Coincident(g17,g-1)
    c: DistanceX(g17) = 23
    c: Symmetric(g5,g2,g-1)
    c: Coincident(g18,g1)
    c: PointOnObject(g18,g15)
    c: Vertical(g18)
    c: Coincident(g19,g2)
    c: PointOnObject(g19,g15)
    c: Vertical(g19)
    c: DistanceY(g19) = -38
    c: DistanceY(g18) = -50
    c: Vertical(g20)
    c: Symmetric(g0,g20,g-1)
    c: Coincident(g21,g20)
    c: Horizontal(g21)
    c: Coincident(g22,g0)
    c: Horizontal(g22)
    c: Coincident(g23,g21)
    c: Coincident(g23,g22)
    c: Vertical(g23)
    c: DistanceX(g21) = 28
    c: DistanceY(g23) = -59
    c: PointOnObject(g24,g23)
    c: Coincident(g24,g-1)
    c: Horizontal(g24)
    c: DistanceX(g24) = 29
    c: Horizontal(g17)
    c: Symmetric(g12,g8,g-1)
    c: PointOnObject(g25,g-2)
    c: Coincident(g25,g15)
    c: Horizontal(g25)
    c: DistanceX(g10) = 16
    c: Tangent(g2,g1)
    c: Vertical(g26)
    c: Coincident(g27,g26)
    c: Coincident(g27,g3)
    c: Parallel(g5,g27)
    c: Coincident(g5,g26)
    c: Coincident(g28,g2)
    c: PointOnObject(g28,g19)
    c: Coincident(g29,g28)
    c: Coincident(g29,g3)
    c: Equal(g28,g26)
    c: Distance(g29) = 17.8283
    c: Parallel(g30,g29)
    c: Coincident(g0,g30)
    c: Coincident(g10,g30)
    c: Parallel(g31,g27)
    c: Coincident(g6,g31)
    c: Coincident(g20,g31)
FEATURE [Part::Cylinder] Cylinder018  label="Rueda_Madre"
  Angle = 360
  Height = 8
  Placement = pos=(19.5,-46,13.5) rot=(1,0,0;1.5708rad)
  Radius = 32
FEATURE [Part::Cylinder] Cylinder020  label="Porta-Portapilas_Cilindro_Cables"
  Angle = 360
  Height = 4
  Placement = pos=(-43,-11.5,43) rot=(0,0,1;0rad)
  Radius = 5
FEATURE [Part::Box] Box019  label="Porta-Portapilas_Cubo_Cables"
  Height = 4
  Length = 20
  Placement = pos=(-43,-16.5,43) rot=(0,0,1;0rad)
  Width = 10
FEATURE [Part::Chamfer] Chamfer002
  Base = -> Chamfer
  Edges = 1 edges r=0.3: [Edge135]
FEATURE [Part::Fillet] Fillet006  label="Horn_Rueda_1"
  Base = -> Chamfer002
  Edges = 1 edges r=0.1: [Edge8]
  Placement = pos=(19.5,-51,13.5) rot=(1,0,0;1.5708rad)
FEATURE [Part::Cylinder] Cylinder021  label="Taladro_Ultrasonido_Servo"
  Angle = 360
  Height = 10
  Placement = pos=(61,0,27) rot=(0,0,1;0rad)
  Radius = 1.75
FEATURE [Part::Cylinder] Cylinder022  label="Taladro_Ultrasonido_Tornillo2"
  Angle = 360
  Height = 10
  Placement = pos=(62,-25,40) rot=(0,1,0;1.5708rad)
  Radius = 1.85
FEATURE [Part::Cylinder] Cylinder023  label="Taladro_Ultrasonido_Tornillo_1"
  Angle = 360
  Height = 10
  Placement = pos=(62,25,40) rot=(0,1,0;1.5708rad)
  Radius = 1.85
FEATURE [Part::MultiFuse] Fusion027  label="[Union]_Taladros_Ultrasonido"
  Shapes = -> [Cylinder023,Cylinder022,Cylinder021]
FEATURE [Sketcher::SketchObject] Sketch022  label="[Croquis]_Ultrasonido_Base"
  Placement = pos=(68,-27.9,31) rot=(0.707107,-0.707107,0;3.14159rad)
  Support = -> Box013 [Face1]
  sketch-geometry (11):
    g0: LineSegment StartX=-56 StartY=0 StartZ=0 EndX=-56 EndY=2 EndZ=0
    g1: LineSegment StartX=0 StartY=0 StartZ=0 EndX=0 EndY=2 EndZ=0
    g2: LineSegment [constr] StartX=-28 StartY=0 StartZ=0 EndX=-28 EndY=21.5 EndZ=0
    g3: LineSegment [constr] StartX=-28 StartY=0 StartZ=0 EndX=-56 EndY=0 EndZ=0
    g4: LineSegment StartX=-56 StartY=0 StartZ=0 EndX=0 EndY=0 EndZ=0
    g5: ArcOfCircle CenterX=-51 CenterY=21.7516 CenterZ=0 NormalX=0 NormalY=0 NormalZ=1 Radius=19.7516 StartAngle=4.71239 EndAngle=6.27045
    g6: ArcOfCircle CenterX=-5 CenterY=21.7516 CenterZ=0 NormalX=0 NormalY=0 NormalZ=1 Radius=19.7516 StartAngle=3.15433 EndAngle=4.71239
    g7: ArcOfCircle CenterX=-28 CenterY=21.5 CenterZ=0 NormalX=0 NormalY=0 NormalZ=1 Radius=3.25 StartAngle=0 EndAngle=3.14159
    g8: LineSegment [constr] StartX=-31.25 StartY=21.5 StartZ=0 EndX=-24.75 EndY=21.5 EndZ=0
    g9: LineSegment StartX=-56 StartY=2 StartZ=0 EndX=-51 EndY=2 EndZ=0
    g10: LineSegment StartX=0 StartY=2 StartZ=0 EndX=-5 EndY=2 EndZ=0
FEATURE [Part::Feature] Part__Feature149  label="R6bqZUM_bloqs_Light002"
  Placement = pos=(1.91,-1.7,0) rot=(0,0,1;3.14159rad)
  shape: bbox 1.6 x 0.8 x 0.4 mm, 36 faces (baked)
FEATURE [Part::Feature] Part__Feature150  label="RfbbqZUM_bloqs_Light002"
  Placement = pos=(7.49,-7.22,0) rot=(0,0,1;0rad)
  shape: bbox 1.6 x 0.8 x 0.4 mm, 36 faces (baked)
FEATURE [Part::Feature] Part__Feature151  label="J1bqZUM_bloqs_Light002"
  Placement = pos=(-4.08502e-05,-19.573,2.98) rot=(1,0,0;1.5708rad)
  shape: bbox 10.16 x 13.59 x 10.29 mm, 129 faces (baked)
FEATURE [Part::Feature] Part__Feature152  label="R2bqZUM_bloqs_Light002"
  Placement = pos=(-1.59,4.2,0) rot=(0,0,1;3.14159rad)
  shape: bbox 1.6 x 0.8 x 0.4 mm, 36 faces (baked)
FEATURE [Part::Feature] Part__Feature153  label="R8bqZUM_bloqs_Light"
  Placement = pos=(-8.39353,3.11612,1.5) rot=(0,0,1;3.14159rad)
  shape: bbox 5.212 x 4.302 x 4.742 mm, 74 faces (baked)
FEATURE [Part::Feature] Part__Feature154  label="C4bqZUM_bloqs_Light002"
  Placement = pos=(6.21,4.2,0) rot=(0,0,1;3.14159rad)
  shape: bbox 1.6 x 0.8 x 0.6 mm, 44 faces (baked)
FEATURE [Part::Feature] Part__Feature155  label="U2bqZUM_bloqs_Light002"
  Placement = pos=(5.10492,-0.244957,0) rot=(0.57735,0.57735,0.57735;2.0944rad)
  shape: bbox 3 x 6.456 x 1.2 mm, 129 faces (baked)
FEATURE [Part::Feature] Part__Feature156  label="R5bqZUM_bloqs_Light002"
  Placement = pos=(1.01,4.2,0) rot=(0,0,1;3.14159rad)
  shape: bbox 1.6 x 0.8 x 0.4 mm, 36 faces (baked)
FEATURE [Part::Feature] Part__Feature157  label="C3bqZUM_bloqs_Light002"
  Placement = pos=(1.91,1.1,0) rot=(0,0,1;3.14159rad)
  shape: bbox 1.6 x 0.8 x 0.6 mm, 44 faces (baked)
FEATURE [Part::Feature] Part__Feature158  label="C2bqZUM_bloqs_Light002"
  Placement = pos=(-4.21,4.2,0) rot=(0,0,1;0rad)
  shape: bbox 1.6 x 0.8 x 0.6 mm, 44 faces (baked)
FEATURE [Part::Feature] Part__Feature159  label="R7bqZUM_bloqs_Light002"
  Placement = pos=(1.91,-0.3,0) rot=(0,0,1;3.14159rad)
  shape: bbox 1.6 x 0.8 x 0.4 mm, 36 faces (baked)
FEATURE [Part::Feature] Part__Feature160  label="PCB005"
  Placement = pos=(0,0,-1.6) rot=(0,0,1;0rad)
  shape: bbox 28.95 x 26.02 x 1.6 mm, 83 faces (baked)
FEATURE [Part::Feature] Part__Feature161  label="C1bqZUM_bloqs_Light002"
  Placement = pos=(3.91,-5.1,0) rot=(0,0,1;3.14159rad)
  shape: bbox 1.6 x 0.8 x 0.6 mm, 44 faces (baked)
FEATURE [Part::Feature] Part__Feature162  label="D2bqZUM_bloqs_Light002"
  Placement = pos=(7.50008,-5.79987,0) rot=(0,0,1;3.14159rad)
  shape: bbox 1.83 x 0.8489 x 0.71 mm, 32 faces (baked)
FEATURE [Part::Feature] Part__Feature163  label="R9bqZUM_bloqs_Light002"
  Placement = pos=(-6.69,-5.3,0) rot=(0,0,1;3.14159rad)
  shape: bbox 1.6 x 0.8 x 0.4 mm, 36 faces (baked)
FEATURE [Part::MultiFuse] Fusion028  label="Sensor_LDR1"
  Placement = pos=(83.5,-28,5) rot=(0,0,-1;1.5708rad)
  Shapes = -> [Part__Feature160,Part__Feature156,Part__Feature153,Part__Feature159,Part__Feature152,Part__Feature161,Part__Feature162,Part__Feature163,Part__Feature155,Part__Feature149,Part__Feature154,Part__Feature158,Part__Feature151,Part__Feature157,Part__Feature150]
FEATURE [Part::Feature] Part__Feature164  label="J1bqZUM_bloqs_Light003"
  Placement = pos=(-4.08502e-05,-19.573,2.98) rot=(1,0,0;1.5708rad)
  shape: bbox 10.16 x 13.59 x 10.29 mm, 129 faces (baked)
FEATURE [Part::Feature] Part__Feature165  label="R2bqZUM_bloqs_Light003"
  Placement = pos=(-1.59,4.2,0) rot=(0,0,1;3.14159rad)
  shape: bbox 1.6 x 0.8 x 0.4 mm, 36 faces (baked)
FEATURE [Part::Feature] Part__Feature166  label="R8bqZUM_bloqs_Light001"
  Placement = pos=(-8.39353,3.11612,1.5) rot=(0,0,1;3.14159rad)
  shape: bbox 5.212 x 4.302 x 4.742 mm, 74 faces (baked)
FEATURE [Part::Feature] Part__Feature167  label="C1bqZUM_bloqs_Light003"
  Placement = pos=(3.91,-5.1,0) rot=(0,0,1;3.14159rad)
  shape: bbox 1.6 x 0.8 x 0.6 mm, 44 faces (baked)
FEATURE [Part::Feature] Part__Feature168  label="RfbbqZUM_bloqs_Light003"
  Placement = pos=(7.49,-7.22,0) rot=(0,0,1;0rad)
  shape: bbox 1.6 x 0.8 x 0.4 mm, 36 faces (baked)
FEATURE [Part::Feature] Part__Feature169  label="C2bqZUM_bloqs_Light003"
  Placement = pos=(-4.21,4.2,0) rot=(0,0,1;0rad)
  shape: bbox 1.6 x 0.8 x 0.6 mm, 44 faces (baked)
FEATURE [Part::Feature] Part__Feature170  label="PCB006"
  Placement = pos=(0,0,-1.6) rot=(0,0,1;0rad)
  shape: bbox 28.95 x 26.02 x 1.6 mm, 83 faces (baked)
FEATURE [Part::Feature] Part__Feature171  label="R7bqZUM_bloqs_Light003"
  Placement = pos=(1.91,-0.3,0) rot=(0,0,1;3.14159rad)
  shape: bbox 1.6 x 0.8 x 0.4 mm, 36 faces (baked)
FEATURE [Part::Feature] Part__Feature172  label="R5bqZUM_bloqs_Light003"
  Placement = pos=(1.01,4.2,0) rot=(0,0,1;3.14159rad)
  shape: bbox 1.6 x 0.8 x 0.4 mm, 36 faces (baked)
FEATURE [Part::Feature] Part__Feature173  label="C4bqZUM_bloqs_Light003"
  Placement = pos=(6.21,4.2,0) rot=(0,0,1;3.14159rad)
  shape: bbox 1.6 x 0.8 x 0.6 mm, 44 faces (baked)
FEATURE [Part::Feature] Part__Feature174  label="R6bqZUM_bloqs_Light003"
  Placement = pos=(1.91,-1.7,0) rot=(0,0,1;3.14159rad)
  shape: bbox 1.6 x 0.8 x 0.4 mm, 36 faces (baked)
FEATURE [Part::Feature] Part__Feature175  label="U2bqZUM_bloqs_Light003"
  Placement = pos=(5.10492,-0.244957,0) rot=(0.57735,0.57735,0.57735;2.0944rad)
  shape: bbox 3 x 6.456 x 1.2 mm, 129 faces (baked)
FEATURE [Part::Feature] Part__Feature176  label="R9bqZUM_bloqs_Light003"
  Placement = pos=(-6.69,-5.3,0) rot=(0,0,1;3.14159rad)
  shape: bbox 1.6 x 0.8 x 0.4 mm, 36 faces (baked)
FEATURE [Part::Feature] Part__Feature177  label="C3bqZUM_bloqs_Light003"
  Placement = pos=(1.91,1.1,0) rot=(0,0,1;3.14159rad)
  shape: bbox 1.6 x 0.8 x 0.6 mm, 44 faces (baked)
FEATURE [Part::Feature] Part__Feature178  label="D2bqZUM_bloqs_Light003"
  Placement = pos=(7.50008,-5.79987,0) rot=(0,0,1;3.14159rad)
  shape: bbox 1.83 x 0.8489 x 0.71 mm, 32 faces (baked)
FEATURE [Part::MultiFuse] Fusion029  label="Sensor_LDR2"
  Placement = pos=(83.5,28,5) rot=(0,0,-1;1.5708rad)
  Shapes = -> [Part__Feature170,Part__Feature172,Part__Feature166,Part__Feature171,Part__Feature165,Part__Feature167,Part__Feature178,Part__Feature176,Part__Feature175,Part__Feature174,Part__Feature173,Part__Feature169,Part__Feature164,Part__Feature177,Part__Feature168]
FEATURE [Part::Box] Box020  label="Sujeta_Tuerca_ Base_3"
  Height = 17
  Length = 10
  Placement = pos=(-22,15,3) rot=(0,0,1;0rad)
  Width = 10
FEATURE [Part::Box] Box021  label="Hueco_Cuerpo_Tuerca_6"
  Height = 6
  Length = 62
  Placement = pos=(-22,23,5.5) rot=(1,0,0;1.5708rad)
  Width = 3
FEATURE [Part::Chamfer] Chamfer003  label="[Chaflan]_Sujeta_Tuerca_Base_3"
  Base = -> Box020
  Edges = 1 edges r=9.99: [Edge10]
FEATURE [Part::Box] Box023  label="Sujeta_Tuerca_Techo_3"
  Height = 6
  Length = 10
  Placement = pos=(-22,18,24) rot=(0,0,1;0rad)
  Width = 7
FEATURE [Part::Box] Box024  label="Hueco_Cuerpo_Tuerca_5"
  Height = 6
  Length = 10
  Placement = pos=(-22,27.35,26.5) rot=(1,0,0;1.5708rad)
  Width = 3
FEATURE [Part::Box] Box025  label="Hueco_Cuerpo_Tuerca_8"
  Height = 6
  Length = 62
  Placement = pos=(-22,-17,5.55) rot=(1,0,0;1.5708rad)
  Width = 3
FEATURE [Part::Box] Box026  label="Sujeta_Tuerca_Base_1"
  Height = 21
  Length = 10
  Placement = pos=(-22,15,3) rot=(0,0,1;0rad)
  Width = 10
FEATURE [Part::Chamfer] Chamfer004  label="[Chaflan]_Sujeta_Tuerca_Base_1"
  Base = -> Box026
  Edges = 1 edges r=9.99: [Edge10]
  Placement = pos=(52,0,0) rot=(0,0,1;0rad)
FEATURE [Part::Box] Box027  label="Sujeta_Tuerca_Base_2"
  Height = 17
  Length = 10
  Placement = pos=(-22,15,3) rot=(0,0,1;0rad)
  Width = 10
FEATURE [Part::Chamfer] Chamfer005  label="[Chaflan]_Sujeta_Tuerca_Base_2"
  Base = -> Box027
  Edges = 1 edges r=9.99: [Edge10]
  Placement = pos=(-34,0,0) rot=(0,0,1;3.14159rad)
FEATURE [Part::Box] Box029  label="Sujeta_Tuerca_Techo_4"
  Height = 6
  Length = 10
  Placement = pos=(30,-25,24) rot=(0,0,1;0rad)
  Width = 12
FEATURE [Part::MultiFuse] Fusion030  label="[Union]_Cuerpo_vaciado_XY"
  Shapes = -> [Box006,Box]
FEATURE [Part::Cut] Cut  label="[Diferencia]_Cuerpo_Madre_Vaciado_XY"
  Base = -> Box001
  Tool = -> Fusion030
FEATURE [Part::Box] Box030  label="Hueco_Cuerpo_Tuerca_7"
  Height = 6
  Length = 10
  Placement = pos=(-22,-21,26.5) rot=(1,0,0;1.5708rad)
  Width = 3
FEATURE [Part::Box] Box031  label="Sujeta_Tuerca_Techo_2"
  Height = 6
  Length = 10
  Placement = pos=(30,3,24) rot=(0,0,1;0rad)
  Width = 12
FEATURE [Part::Box] Box032  label="Hueco_Cuerpo_Tuerca_9"
  Height = 6
  Length = 10
  Placement = pos=(30,-15.75,26.5) rot=(1,0,0;1.5708rad)
  Width = 3
FEATURE [Part::Box] Box033  label="Sujeta_Tuerca_Techo_1"
  Height = 6
  Length = 10
  Placement = pos=(-22,-25,24) rot=(0,0,1;0rad)
  Width = 7
FEATURE [Part::Box] Box034  label="Hueco_Cuerpo_Tuerca_10"
  Height = 6
  Length = 10
  Placement = pos=(30,12,26.25) rot=(1,0,0;1.5708rad)
  Width = 3
FEATURE [Part::Cylinder] Cylinder024  label="Taladro_tornillo_ZUM_1"
  Angle = 360
  Height = 9
  Placement = pos=(35,9,24) rot=(0,0,1;0rad)
  Radius = 1.75
FEATURE [Part::Cylinder] Cylinder025  label="Taladro_Tornillo_ZUM_2"
  Angle = 360
  Height = 9
  Placement = pos=(35,-19,24) rot=(0,0,1;0rad)
  Radius = 1.75
FEATURE [Part::Cylinder] Cylinder026  label="Taladro_tornillo_ZUM_3"
  Angle = 360
  Height = 9
  Placement = pos=(-17,-24,24) rot=(0,0,1;0rad)
  Radius = 1.75
FEATURE [Part::Cylinder] Cylinder027  label="Taladro_tornillo_ZUM_4"
  Angle = 360
  Height = 9
  Placement = pos=(-15.75,24.25,24) rot=(0,0,1;0rad)
  Radius = 1.75
FEATURE [Part::Cylinder] Cylinder028  label="Taladro_tornillo_ZUM_5"
  Angle = 360
  Height = 9
  Placement = pos=(-17,20,3) rot=(0,0,1;0rad)
  Radius = 1.75
FEATURE [Part::Cylinder] Cylinder029  label="Taladro_tornillo_ZUM_6"
  Angle = 360
  Height = 9
  Placement = pos=(35,-20,3) rot=(0,0,1;0rad)
  Radius = 1.75
FEATURE [Part::Cylinder] Cylinder030  label="Taladro_tornillo_ZUM_7"
  Angle = 360
  Height = 9
  Placement = pos=(-17,-20,3) rot=(0,0,1;0rad)
  Radius = 1.75
FEATURE [Part::Cylinder] Cylinder031  label="Taladro_tornillo_ZUM_8"
  Angle = 360
  Height = 9
  Placement = pos=(35,20,3) rot=(0,0,1;0rad)
  Radius = 1.75
FEATURE [Part::Cylinder] Cylinder032  label="Taladro_Tornillo_Servo_4"
  Angle = 360
  Height = 12
  Placement = pos=(-16.2,-33,18.6) rot=(-1,0,0;1.5708rad)
  Radius = 1.75
FEATURE [Part::Cylinder] Cylinder033  label="Taladro_Tornillo_Servo_5"
  Angle = 360
  Height = 8
  Placement = pos=(-16.2,-33,8.4) rot=(-1,0,0;1.5708rad)
  Radius = 1.75
FEATURE [Part::Cylinder] Cylinder034  label="Taladro_Tornillo_Servo_6"
  Angle = 360
  Height = 12
  Placement = pos=(34.2,-33,18.6) rot=(-1,0,0;1.5708rad)
  Radius = 1.75
FEATURE [Part::Cylinder] Cylinder035  label="Taladro_Tornillo_Servo_7"
  Angle = 360
  Height = 12
  Placement = pos=(34.2,-33,8.4) rot=(-1,0,0;1.5708rad)
  Radius = 1.75
FEATURE [Part::Box] Box014  label="Brazo_Miniservo_1"
  Height = 2.5
  Length = 13
  Placement = pos=(50,-136.5,16) rot=(0,0,1;0rad)
  Width = 4.9
FEATURE [Part::Box] Box035  label="Hueco_Miniservo"
  Height = 20
  Length = 13
  Placement = pos=(50,-132.1,1) rot=(0,0,1;0rad)
  Width = 24.1
FEATURE [Part::MultiFuse] Fusion034  label="[Union]_Huecos_miniservo"
  Shapes = -> [Box014,Box015,Box035]
FEATURE [Part::Cut] Cut012  label="[Diferencia]Sujeta_Miniservo_Huecos"
  Base = -> Box016
  Tool = -> Fusion034
FEATURE [Part::MultiFuse] Fusion035  label="[Union]_Sujeta_miniservo_orificios_tornillos"
  Shapes = -> [Cylinder015,Cylinder014]
FEATURE [Part::Cut] Cut013  label="[Diferencia]_Sujeta_Miniservo_Tornillos"
  Base = -> Cut012
  Tool = -> Fusion035
FEATURE [Part::Cylinder] Cylinder036  label="Taladro_Miniservo_2"
  Angle = 360
  Height = 8
  Placement = pos=(57,-106,14) rot=(0,0,1;0rad)
  Radius = 1.25
FEATURE [Part::Cylinder] Cylinder037  label="Taladro_Miniservo_1"
  Angle = 360
  Height = 8
  Placement = pos=(57,-134,14) rot=(0,0,1;0rad)
  Radius = 1.25
FEATURE [Part::MultiFuse] Fusion036  label="[Union]Sujeta_Miniservo_Taladros"
  Shapes = -> [Cylinder037,Cylinder036]
FEATURE [Part::Box] Box038  label="Hueco_Cables_Miniservo"
  Height = 10
  Length = 14
  Placement = pos=(57,-14,-4) rot=(0,0,1;0rad)
  Width = 10
FEATURE [Part::Cut] Cut016  label="[Diferencia]_Sujeta_Taladros"
  Base = -> Cut013
  Tool = -> Fusion036
FEATURE [Part::Fillet] Fillet008  label="[Redondeado]_Sujeta_Miniservo_Primer_Redondeo"
  Base = -> Cut016
  Edges = 9 edges r=1.3: [Edge1,Edge2,Edge3,Edge6,Edge7,Edge8,Edge9,Edge12,Edge19]
  Placement = pos=(5,126,2) rot=(0,0,1;0rad)
FEATURE [Part::Cut] Cut017  label="[Diferencia]_Sujeta_Miniservo_Cables"
  Base = -> Fillet008
  Placement = pos=(-1,0,0) rot=(0,0,1;0rad)
  Tool = -> Box038
FEATURE [Part::Torus] Torus  label="Toroide_neumatico_1"
  Angle1 = -180
  Angle2 = 180
  Angle3 = 360
  Placement = pos=(19.5,-51,13.5) rot=(1,0,0;1.5708rad)
  Radius1 = 32
  Radius2 = 2
FEATURE [Part::Torus] Torus001  label="Toroide_neumatico_resta"
  Angle1 = -180
  Angle2 = 180
  Angle3 = 360
  Placement = pos=(19.5,-50,13.5) rot=(1,0,0;1.5708rad)
  Radius1 = 32
  Radius2 = 2.5
FEATURE [Sketcher::SketchObject] Sketch025  label="[Croquis]_Rueda_Huella_Horn"
  Placement = pos=(19.5,-54,13.5) rot=(1,0,0;1.5708rad)
  Support = -> Cylinder018 [Face2]
  sketch-geometry (20):
    g0: ArcOfCircle CenterX=0 CenterY=17 CenterZ=0 NormalX=0 NormalY=0 NormalZ=1 Radius=2.75 StartAngle=0.177686 EndAngle=1.5708
    g1: LineSegment StartX=0 StartY=17 StartZ=0 EndX=0 EndY=0 EndZ=0
    g2: LineSegment StartX=2.7067 StartY=17.4861 StartZ=0 EndX=4.5 EndY=7.5 EndZ=0
    g3: LineSegment [constr] StartX=0 StartY=7.5 StartZ=0 EndX=0 EndY=0 EndZ=0
    g4: LineSegment StartX=4.5 StartY=7.5 StartZ=0 EndX=4.5 EndY=5.5 EndZ=0
    g5: ArcOfCircle CenterX=5.5 CenterY=5.50001 CenterZ=0 NormalX=0 NormalY=0 NormalZ=1 Radius=1 StartAngle=3.14159 EndAngle=4.71239
    g6: LineSegment StartX=5.5 StartY=4.50001 StartZ=0 EndX=7.5 EndY=4.50001 EndZ=0
    g7: LineSegment StartX=7.5 StartY=4.50001 StartZ=0 EndX=17.4861 EndY=2.7067 EndZ=0
    g8: LineSegment [constr] StartX=0 StartY=19.75 StartZ=0 EndX=0 EndY=0 EndZ=0
    g9: LineSegment StartX=0 StartY=0 StartZ=0 EndX=19.75 EndY=0 EndZ=0
    g10: ArcOfCircle CenterX=17 CenterY=0 CenterZ=0 NormalX=0 NormalY=0 NormalZ=1 Radius=2.75 StartAngle=0 EndAngle=1.39311
    g11: LineSegment [constr] StartX=4.5 StartY=7.5 StartZ=0 EndX=0 EndY=7.5 EndZ=0
    g12: ArcOfCircle CenterX=0 CenterY=17 CenterZ=0 NormalX=0 NormalY=0 NormalZ=1 Radius=2.75 StartAngle=1.5708 EndAngle=2.96391
    g13: LineSegment StartX=-2.7067 StartY=17.4861 StartZ=0 EndX=-4.5 EndY=7.5 EndZ=0
    g14: LineSegment StartX=-4.5 StartY=7.5 StartZ=0 EndX=-4.5 EndY=5.5 EndZ=0
    g15: ArcOfCircle CenterX=-17 CenterY=0 CenterZ=0 NormalX=0 NormalY=0 NormalZ=1 Radius=2.75 StartAngle=1.74848 EndAngle=3.14159
    g16: LineSegment StartX=-19.75 StartY=0 StartZ=0 EndX=0 EndY=0 EndZ=0
    g17: LineSegment StartX=-5.5 StartY=4.50001 StartZ=0 EndX=-7.5 EndY=4.50001 EndZ=0
    g18: LineSegment StartX=-17.4861 StartY=2.7067 StartZ=0 EndX=-7.5 EndY=4.50001 EndZ=0
    g19: ArcOfCircle CenterX=-5.5 CenterY=5.50001 CenterZ=0 NormalX=0 NormalY=0 NormalZ=1 Radius=1 StartAngle=4.71239 EndAngle=6.28318
  constraints (59):
    c: PointOnObject(g0,g-2)
    c: Radius(g0) = 2.75
    c: Coincident(g1,g-1)
    c: DistanceY(g1) = -17
    c: Coincident(g0,g1)
    c: Coincident(g2,g0)
    c: Coincident(g3,g-1)
    c: Vertical(g3)
    c: DistanceY(g3) = -7.5
    c: Coincident(g4,g2)
    c: Vertical(g4)
    c: DistanceY(g4) = -2
    c: Coincident(g5,g4)
    c: Tangent(g5,g4)
    c: Coincident(g6,g5)
    c: Tangent(g5,g6)
    c: Horizontal(g6)
    c: Equal(g6,g4)
    c: Coincident(g7,g6)
    c: PointOnObject(g0,g-2)
    c: Coincident(g8,g0)
    c: Coincident(g8,g-1)
    c: Coincident(g9,g-1)
    c: Horizontal(g9)
    c: PointOnObject(g10,g9)
    c: Coincident(g10,g7)
    c: Coincident(g10,g9)
    c: Equal(g8,g9)
    c: Tangent(g10,g7)
    c: Equal(g0,g10)
    c: Equal(g7,g2)
    c: Coincident(g11,g2)
    c: PointOnObject(g11,g1)
    c: Horizontal(g11)
    c: Tangent(g0,g2)
    c: DistanceX(g11) = -4.5
    c: Radius(g5) = 1
    c: Coincident(g12,g0)
    c: Coincident(g12,g0)
    c: Symmetric(g12,g0,g1)
    c: Coincident(g13,g12)
    c: Coincident(g14,g13)
    c: Vertical(g14)
    c: Symmetric(g2,g13,g-2)
    c: Equal(g14,g4)
    c: Symmetric(g17,g5,g-2)
    c: Symmetric(g15,g7,g-2)
    c: PointOnObject(g15,g-1)
    c: PointOnObject(g15,g-1)
    c: Equal(g15,g10)
    c: Coincident(g16,g15)
    c: Coincident(g16,g-1)
    c: Horizontal(g17)
    c: Symmetric(g17,g6,g-2)
    c: Coincident(g18,g15)
    c: Coincident(g18,g17)
    c: Coincident(g19,g14)
    c: Equal(g19,g5)
    c: Coincident(g19,g17)
FEATURE [PartDesign::Pocket] Pocket011  label="[Extrusion]_Rueda_Huella_Horn"
  Length = 5
  Placement = pos=(19.5,-46,13.5) rot=(1,0,0;1.5708rad)
  Sketch = -> Sketch025
  Type = 0
FEATURE [Part::Box] Box039  label="Hueco_Conector_Miniservo"
  Height = 11
  Length = 18
  Placement = pos=(49,20,3) rot=(0,0,1;0rad)
  Width = 10
FEATURE [Part::Cut] Cut019  label="[Diferencia]_Sujeta_Hueco_Conector"
  Base = -> Cut017
  Tool = -> Box039
FEATURE [Part::Fillet] Fillet010  label="SUJETA_MINISERVO--[Redondeo]_Sujeta_Hueco_Conector"
  Base = -> Cut019
  Edges = 11 edges r=1.5: [Edge8,Edge9,Edge27,Edge28,Edge29,Edge30,Edge46,Edge47,Edge80,Edge97,Edge98]
  Placement = pos=(0,0,-1) rot=(0,0,1;0rad)
FEATURE [Sketcher::SketchObject] Sketch028  label="[Croquis]_Huella_Zumbador"
  Placement = pos=(-5,0,33) rot=(0,0,1;0rad)
  sketch-geometry (8):
    g0: LineSegment StartX=15 StartY=2 StartZ=0 EndX=36 EndY=2 EndZ=0
    g1: LineSegment StartX=36 StartY=2 StartZ=0 EndX=36 EndY=-12 EndZ=0
    g2: LineSegment StartX=36 StartY=-12 StartZ=0 EndX=15 EndY=-12 EndZ=0
    g3: LineSegment StartX=15 StartY=-12 StartZ=0 EndX=15 EndY=2 EndZ=0
    g4: Circle CenterX=25.5 CenterY=5 CenterZ=0 NormalX=0 NormalY=0 NormalZ=1 Radius=2
    g5: Circle CenterX=25.5 CenterY=-15 CenterZ=0 NormalX=0 NormalY=0 NormalZ=1 Radius=2
    g6: LineSegment [constr] StartX=25.5 StartY=5 StartZ=0 EndX=25.5 EndY=-15 EndZ=0
    g7: LineSegment [constr] StartX=15 StartY=-5 StartZ=0 EndX=25.5 EndY=-5 EndZ=0
  constraints (23):
    c: Coincident(g0,g1)
    c: Coincident(g1,g2)
    c: Coincident(g2,g3)
    c: Coincident(g3,g0)
    c: Horizontal(g0)
    c: Horizontal(g2)
    c: Vertical(g1)
    c: Vertical(g3)
    c: Equal(g4,g5)
    c: Radius(g4) = 2
    c: DistanceX(g0) = 21
    c: DistanceY(g1) = -14
    c: Coincident(g6,g4)
    c: Coincident(g6,g5)
    c: Vertical(g6)
    c: DistanceY(g6) = -20
    c: PointOnObject(g7,g3)
    c: PointOnObject(g7,g6)
    c: DistanceX(g7) = 10.5
    c: Symmetric(g4,g5,g7)
    c: Symmetric(g0,g2,g7)
    c: DistanceX(g-1,g0) = 15
    c: DistanceY(g-1,g0) = 2
FEATURE [PartDesign::Pad] Pad  label="[Extrusion]_Ultrasonido_Base"
  Length = 5
  Length2 = 100
  Placement = pos=(68,-27.9,31) rot=(0,-1,0;1.5708rad)
  Sketch = -> Sketch022
  Type = 0
FEATURE [Sketcher::SketchObject] Sketch021  label="[Croquis]_Ultrasonido_Aspa"
  Placement = pos=(68,-27.9,26) rot=(0.707107,-0.707107,0;3.14159rad)
  Support = -> Pad [Face5]
  sketch-geometry (7):
    g0: LineSegment StartX=-25.7554 StartY=21.6552 StartZ=0 EndX=-24.7577 EndY=7.22412 EndZ=0
    g1: LineSegment StartX=-30.2446 StartY=21.6552 StartZ=0 EndX=-31.2423 EndY=7.22412 EndZ=0
    g2: ArcOfCircle CenterX=-28 CenterY=21.5 CenterZ=0 NormalX=0 NormalY=0 NormalZ=1 Radius=2.25 StartAngle=0.0690289 EndAngle=3.07256
    g3: ArcOfCircle CenterX=-28 CenterY=7 CenterZ=0 NormalX=0 NormalY=0 NormalZ=1 Radius=3.25 StartAngle=3.07258 EndAngle=6.3522
    g4: LineSegment [constr] StartX=-28 StartY=0 StartZ=0 EndX=-28 EndY=7 EndZ=0
    g5: LineSegment [constr] StartX=-28 StartY=7 StartZ=0 EndX=-28 EndY=21.5 EndZ=0
    g6: LineSegment [constr] StartX=-28 StartY=0 StartZ=0 EndX=-56 EndY=0 EndZ=0
FEATURE [PartDesign::Pocket] Pocket012  label="[Vaciado]_Ultrasonido_Aspa"
  Length = 3
  Placement = pos=(68,-27.9,31) rot=(0,-1,0;1.5708rad)
  Sketch = -> Sketch021
  Type = 0
FEATURE [Sketcher::SketchObject] Sketch  label="[Croquis]ultrasonido_vaciado_PCB"
  Placement = pos=(66,0,0) rot=(0.57735,-0.57735,-0.57735;2.0944rad)
  sketch-geometry (8):
    g0: LineSegment [constr] StartX=-26.1 StartY=43 StartZ=0 EndX=-23.6 EndY=43 EndZ=0
    g1: ArcOfCircle CenterX=-23.6097 CenterY=41 CenterZ=0 NormalX=0 NormalY=0 NormalZ=1 Radius=2 StartAngle=6.28318 EndAngle=7.84913
    g2: ArcOfCircle CenterX=-11.6097 CenterY=41 CenterZ=0 NormalX=0 NormalY=0 NormalZ=1 Radius=9.99999 StartAngle=3.14159 EndAngle=4.71239
    g3: ArcOfCircle CenterX=11.6097 CenterY=41 CenterZ=0 NormalX=0 NormalY=0 NormalZ=1 Radius=9.99999 StartAngle=4.71239 EndAngle=6.26521
    g4: ArcOfCircle CenterX=23.6 CenterY=41 CenterZ=0 NormalX=0 NormalY=0 NormalZ=1 Radius=2 StartAngle=1.5708 EndAngle=3.23159
    g5: LineSegment StartX=-11.6097 StartY=31 StartZ=0 EndX=11.6097 EndY=31 EndZ=0
    g6: LineSegment StartX=-23.6 StartY=43 StartZ=0 EndX=23.6 EndY=43 EndZ=0
    g7: LineSegment [constr] StartX=-21.6097 StartY=41 StartZ=0 EndX=-21.6097 EndY=31 EndZ=0
FEATURE [PartDesign::Pad] Pad006  label="[Extrusion_]Base"
  Length = 2.8
  Length2 = 100
  Sketch = -> Sketch018
  Type = 0
FEATURE [Sketcher::SketchObject] Sketch023  label="[Croquis]_Taladros_Base"
  Placement = pos=(0,56,0) rot=(0,0.707107,0.707107;3.14159rad)
  Support = -> Pad006 [Face23]
  sketch-geometry (46):
    g0: Circle CenterX=99 CenterY=16 CenterZ=0 NormalX=0 NormalY=0 NormalZ=1 Radius=1.75
    g1: Circle CenterX=99 CenterY=-16 CenterZ=0 NormalX=0 NormalY=0 NormalZ=1 Radius=1.75
    g2: Circle CenterX=83.5 CenterY=18 CenterZ=0 NormalX=0 NormalY=0 NormalZ=1 Radius=1.75
    g3: Circle CenterX=83.5 CenterY=-18 CenterZ=0 NormalX=0 NormalY=0 NormalZ=1 Radius=1.75
    g4: Circle CenterX=83.5 CenterY=38 CenterZ=0 NormalX=0 NormalY=0 NormalZ=1 Radius=1.75
    g5: LineSegment [constr] StartX=83.5 StartY=38 StartZ=0 EndX=83.5 EndY=18 EndZ=0
    g6: Circle CenterX=83.5 CenterY=-38 CenterZ=0 NormalX=0 NormalY=0 NormalZ=1 Radius=1.75
    g7: LineSegment [constr] StartX=83.5 StartY=-18 StartZ=0 EndX=83.5 EndY=-38 EndZ=0
    g8: LineSegment [constr] StartX=83.5 StartY=18 StartZ=0 EndX=83.5 EndY=0 EndZ=0
    g9: LineSegment [constr] StartX=99 StartY=16 StartZ=0 EndX=99 EndY=0 EndZ=0
    g10: LineSegment [constr] StartX=83.5 StartY=0 StartZ=0 EndX=99 EndY=0 EndZ=0
    g11: LineSegment StartX=74.5 StartY=35 StartZ=0 EndX=95.5 EndY=35 EndZ=0
    g12: LineSegment StartX=95.5 StartY=35 StartZ=0 EndX=95.5 EndY=21 EndZ=0
    g13: LineSegment StartX=95.5 StartY=21 StartZ=0 EndX=74.5 EndY=21 EndZ=0
    g14: LineSegment StartX=74.5 StartY=21 StartZ=0 EndX=74.5 EndY=35 EndZ=0
    g15: LineSegment [constr] StartX=95.5 StartY=28 StartZ=0 EndX=83.5 EndY=28 EndZ=0
    g16: LineSegment StartX=74.5 StartY=-21 StartZ=0 EndX=95.5 EndY=-21 EndZ=0
    g17: LineSegment StartX=95.5 StartY=-21 StartZ=0 EndX=95.5 EndY=-35 EndZ=0
    g18: LineSegment StartX=95.5 StartY=-35 StartZ=0 EndX=74.5 EndY=-35 EndZ=0
    g19: LineSegment StartX=74.5 StartY=-35 StartZ=0 EndX=74.5 EndY=-21 EndZ=0
    g20: LineSegment [constr] StartX=83.5 StartY=28 StartZ=0 EndX=83.5 EndY=38 EndZ=0
    g21: LineSegment StartX=111.5 StartY=13 StartZ=0 EndX=86.5 EndY=13 EndZ=0
    g22: LineSegment StartX=86.5 StartY=13 StartZ=0 EndX=86.5 EndY=-13 EndZ=0
    g23: LineSegment StartX=86.5 StartY=-13 StartZ=0 EndX=111.5 EndY=-13 EndZ=0
    g24: LineSegment StartX=111.5 StartY=-13 StartZ=0 EndX=111.5 EndY=13 EndZ=0
    g25: Circle CenterX=52 CenterY=6.8 CenterZ=0 NormalX=0 NormalY=0 NormalZ=1 Radius=1.75
    g26: Circle CenterX=52 CenterY=-18.8 CenterZ=0 NormalX=0 NormalY=0 NormalZ=1 Radius=1.75
    g27: Circle CenterX=35 CenterY=20 CenterZ=0 NormalX=0 NormalY=0 NormalZ=1 Radius=1.75
    g28: Circle CenterX=35 CenterY=-20 CenterZ=0 NormalX=0 NormalY=0 NormalZ=1 Radius=1.75
    g29: LineSegment [constr] StartX=52 StartY=6.8 StartZ=0 EndX=52 EndY=0 EndZ=0
    g30: LineSegment [constr] StartX=52 StartY=-18.8 StartZ=0 EndX=52 EndY=0 EndZ=0
    g31: LineSegment [constr] StartX=83.5 StartY=0 StartZ=0 EndX=52 EndY=0 EndZ=0
    g32: LineSegment [constr] StartX=52 StartY=0 StartZ=0 EndX=35 EndY=0 EndZ=0
    g33: LineSegment [constr] StartX=35 StartY=20 StartZ=0 EndX=35 EndY=0 EndZ=0
    g34: LineSegment [constr] StartX=35 StartY=-20 StartZ=0 EndX=35 EndY=0 EndZ=0
    g35: Circle CenterX=-17 CenterY=20 CenterZ=0 NormalX=0 NormalY=0 NormalZ=1 Radius=1.75
    g36: Circle CenterX=-17 CenterY=-20 CenterZ=0 NormalX=0 NormalY=0 NormalZ=1 Radius=1.75
    g37: LineSegment [constr] StartX=-17 StartY=20 StartZ=0 EndX=-17 EndY=0 EndZ=0
    g38: LineSegment [constr] StartX=35 StartY=0 StartZ=0 EndX=-17 EndY=0 EndZ=0
    g39: LineSegment [constr] StartX=-17 StartY=0 StartZ=0 EndX=-51.95 EndY=0 EndZ=0
    g40: LineSegment [constr] StartX=0 StartY=0 StartZ=0 EndX=-17 EndY=0 EndZ=0
    g41: Circle CenterX=60.6926 CenterY=51.0481 CenterZ=0 NormalX=0 NormalY=0 NormalZ=1 Radius=1.75
    g42: Circle CenterX=-23.268 CenterY=51.0481 CenterZ=0 NormalX=0 NormalY=0 NormalZ=1 Radius=1.75
    g43: Circle CenterX=-23.268 CenterY=-51.0481 CenterZ=0 NormalX=0 NormalY=0 NormalZ=1 Radius=1.75
    g44: Circle CenterX=60.6926 CenterY=-51.0481 CenterZ=0 NormalX=0 NormalY=0 NormalZ=1 Radius=1.75
    g45: LineSegment [constr] StartX=-23.268 StartY=51.0481 StartZ=0 EndX=60.6926 EndY=51.0481 EndZ=0
  constraints (118):
    c: Symmetric(g1,g0,g-1)
    c: Equal(g0,g1)
    c: Equal(g3,g0)
    c: Equal(g2,g0)
    c: Symmetric(g2,g3,g-1)
    c: Equal(g4,g0)
    c: Radius(g0) = 1.75
    c: Coincident(g5,g4)
    c: Coincident(g5,g2)
    c: Vertical(g5)
    c: DistanceY(g5) = -20
    c: Equal(g6,g0)
    c: Coincident(g7,g3)
    c: Coincident(g7,g6)
    c: Vertical(g7)
    c: Coincident(g8,g2)
    c: PointOnObject(g8,g-1)
    c: Vertical(g8)
    c: DistanceY(g8) = -18
    c: Equal(g7,g5)
    c: Coincident(g9,g0)
    c: PointOnObject(g9,g-1)
    c: Vertical(g9)
    c: DistanceY(g9) = -16
    c: Coincident(g10,g8)
    c: Coincident(g10,g9)
    c: DistanceX(g10) = 15.5
    c: Coincident(g11,g12)
    c: Coincident(g12,g13)
    c: Coincident(g13,g14)
    c: Coincident(g14,g11)
    c: Horizontal(g11)
    c: Horizontal(g13)
    c: Vertical(g12)
    c: Vertical(g14)
    c: PointOnObject(g15,g12)
    c: PointOnObject(g15,g5)
    c: Horizontal(g15)
    c: DistanceY(g12) = -14
    c: DistanceX(g11) = 21
    c: DistanceX(g15) = -12
    c: Symmetric(g11,g12,g15)
    c: Coincident(g16,g17)
    c: Coincident(g17,g18)
    c: Coincident(g18,g19)
    c: Coincident(g19,g16)
    c: Horizontal(g16)
    c: Horizontal(g18)
    c: Vertical(g17)
    c: Vertical(g19)
    c: Symmetric(g16,g12,g-1)
    c: Equal(g12,g17)
    c: Equal(g13,g16)
    c: Coincident(g20,g15)
    c: Coincident(g20,g4)
    c: DistanceY(g20) = 10
    c: Coincident(g21,g22)
    c: Coincident(g22,g23)
    c: Coincident(g23,g24)
    c: Coincident(g24,g21)
    c: Horizontal(g21)
    c: Horizontal(g23)
    c: Vertical(g22)
    c: Vertical(g24)
    c: Symmetric(g21,g23,g-1)
    c: DistanceX(g21) = -25
    c: Symmetric(g21,g21,g9)
    c: DistanceY(g24) = 26
    c: Equal(g25,g0)
    c: Equal(g27,g0)
    c: Equal(g28,g0)
    c: Equal(g26,g0)
    c: Coincident(g29,g25)
    c: PointOnObject(g29,g-1)
    c: Vertical(g29)
    c: Coincident(g30,g26)
    c: Coincident(g30,g29)
    c: Vertical(g30)
    c: DistanceY(g29) = -6.8
    c: DistanceY(g30) = 18.8
    c: Coincident(g31,g8)
    c: Coincident(g31,g29)
    c: DistanceX(g31) = -31.5
    c: Coincident(g32,g29)
    c: Horizontal(g32)
    c: DistanceX(g32) = -17
    c: Coincident(g33,g27)
    c: Coincident(g33,g32)
    c: Vertical(g33)
    c: Coincident(g34,g28)
    c: Coincident(g34,g32)
    c: Vertical(g34)
    c: DistanceY(g33) = -20
    c: Equal(g0,g35)
    c: Equal(g36,g0)
    c: Coincident(g37,g35)
    c: Vertical(g37)
    c: DistanceY(g37) = -20
    c: Coincident(g38,g32)
    c: DistanceX(g38) = -52
    c: Symmetric(g28,g27,g38)
    c: Symmetric(g36,g35,g-1)
    c: Horizontal(g39)
    c: Coincident(g38,g37)
    c: Coincident(g40,g-1)
    c: Coincident(g40,g37)
    c: DistanceX(g40) = -17
    c: Coincident(g39,g37)
    c: DistanceX(g39) = -34.95
    c: Equal(g41,g4)
    c: Equal(g44,g41)
    c: Equal(g42,g41)
    c: Equal(g43,g42)
    c: Symmetric(g42,g43,g31)
    c: Symmetric(g41,g44,g31)
    c: Horizontal(g45)
    c: Coincident(g45,g41)
    c: Coincident(g45,g42)
FEATURE [PartDesign::Pocket] Pocket009  label="[Vaciado]_Taladros_Base"
  Length = 5
  Sketch = -> Sketch023
  Type = 1
FEATURE [Part::Cylinder] Cylinder040  label="Taladro_Tornillo_Rueda"
  Angle = 360
  Height = 10
  Placement = pos=(19.5,-39,13.5) rot=(1,0,0;1.5708rad)
  Radius = 4.75
FEATURE [PartDesign::PolarPattern] PolarPattern  label="[Patron_en_polar]_Rueda_Huella_Horn"
  Angle = 360
  Axis = -> Sketch025 [N_Axis]
  Occurrences = 2
  Originals = -> [Pocket011]
  Placement = pos=(19.5,-46,13.5) rot=(1,0,0;1.5708rad)
FEATURE [Part::Cut] Cut022  label="[Diferencia]_Taladro_Tornillo_Rueda"
  Base = -> PolarPattern
  Tool = -> Cylinder040
FEATURE [Sketcher::SketchObject] Sketch030  label="[Croquis]_Hexagonos_Grandes_Rueda"
  ExternalGeometry = -> [Cut022]
  Placement = pos=(0,-54,0) rot=(1,0,0;1.5708rad)
  Support = -> Cut022 [Face2]
  sketch-geometry (31):
    g0: LineSegment [constr] StartX=19.5 StartY=45.5 StartZ=0 EndX=19.5 EndY=13.5 EndZ=0
    g1: LineSegment [constr] StartX=19.5 StartY=13.5 StartZ=0 EndX=51.5 EndY=13.5 EndZ=0
    g2: LineSegment StartX=27.2782 StartY=21.2782 StartZ=0 EndX=35.9715 EndY=18.9488 EndZ=0
    g3: LineSegment StartX=35.9715 StartY=18.9488 StartZ=0 EndX=42.3355 EndY=25.3128 EndZ=0
    g4: LineSegment StartX=42.3355 StartY=25.3128 StartZ=0 EndX=40.0061 EndY=34.0061 EndZ=0
    g5: LineSegment StartX=40.0061 StartY=34.0061 StartZ=0 EndX=31.3128 EndY=36.3355 EndZ=0
    g6: LineSegment StartX=31.3128 StartY=36.3355 StartZ=0 EndX=24.9488 EndY=29.9715 EndZ=0
    g7: LineSegment StartX=24.9488 StartY=29.9715 StartZ=0 EndX=27.2782 EndY=21.2782 EndZ=0
    g8: Circle [constr] CenterX=33.6421 CenterY=27.6421 CenterZ=0 NormalX=0 NormalY=0 NormalZ=1 Radius=9
    g9: LineSegment [constr] StartX=33.6421 StartY=27.6421 StartZ=0 EndX=19.5 EndY=13.5 EndZ=0
    g10: LineSegment StartX=11.7218 StartY=21.2782 StartZ=0 EndX=14.0512 EndY=29.9715 EndZ=0
    g11: LineSegment StartX=14.0512 StartY=29.9715 StartZ=0 EndX=7.68724 EndY=36.3355 EndZ=0
    g12: LineSegment StartX=7.68724 StartY=36.3355 StartZ=0 EndX=-1.0061 EndY=34.0061 EndZ=0
    g13: LineSegment StartX=-1.0061 StartY=34.0061 StartZ=0 EndX=-3.33547 EndY=25.3128 EndZ=0
    g14: LineSegment StartX=-3.33547 StartY=25.3128 StartZ=0 EndX=3.02849 EndY=18.9488 EndZ=0
    g15: LineSegment StartX=3.02849 StartY=18.9488 StartZ=0 EndX=11.7218 EndY=21.2782 EndZ=0
    g16: Circle [constr] CenterX=5.35786 CenterY=27.6421 CenterZ=0 NormalX=0 NormalY=0 NormalZ=1 Radius=9
    g17: LineSegment StartX=7.68724 StartY=-9.33547 StartZ=0 EndX=14.0512 EndY=-2.97151 EndZ=0
    g18: LineSegment StartX=14.0512 StartY=-2.97151 StartZ=0 EndX=11.7218 EndY=5.72183 EndZ=0
    g19: LineSegment StartX=11.7218 StartY=5.72183 StartZ=0 EndX=3.02849 EndY=8.0512 EndZ=0
    g20: LineSegment StartX=3.02849 StartY=8.0512 StartZ=0 EndX=-3.33547 EndY=1.68724 EndZ=0
    g21: LineSegment StartX=-3.33547 StartY=1.68724 StartZ=0 EndX=-1.0061 EndY=-7.0061 EndZ=0
    g22: LineSegment StartX=-1.0061 StartY=-7.0061 StartZ=0 EndX=7.68724 EndY=-9.33547 EndZ=0
    g23: Circle [constr] CenterX=5.35786 CenterY=-0.642136 CenterZ=0 NormalX=0 NormalY=0 NormalZ=1 Radius=9
    g24: LineSegment StartX=40.0061 StartY=-7.0061 StartZ=0 EndX=42.3355 EndY=1.68724 EndZ=0
    g25: LineSegment StartX=42.3355 StartY=1.68724 StartZ=0 EndX=35.9715 EndY=8.0512 EndZ=0
    g26: LineSegment StartX=35.9715 StartY=8.0512 StartZ=0 EndX=27.2782 EndY=5.72183 EndZ=0
    g27: LineSegment StartX=27.2782 StartY=5.72183 StartZ=0 EndX=24.9488 EndY=-2.97151 EndZ=0
    g28: LineSegment StartX=24.9488 StartY=-2.97151 StartZ=0 EndX=31.3128 EndY=-9.33547 EndZ=0
    g29: LineSegment StartX=31.3128 StartY=-9.33547 StartZ=0 EndX=40.0061 EndY=-7.0061 EndZ=0
    g30: Circle [constr] CenterX=33.6421 CenterY=-0.642136 CenterZ=0 NormalX=0 NormalY=0 NormalZ=1 Radius=9
  constraints (70):
    c: PointOnObject(g0,g-3)
    c: Coincident(g0,g-3)
    c: Vertical(g0)
    c: Coincident(g1,g0)
    c: PointOnObject(g1,g-3)
    c: Horizontal(g1)
    c: Coincident(g2,g3)
    c: Coincident(g3,g4)
    c: Coincident(g4,g5)
    c: Coincident(g5,g6)
    c: Coincident(g6,g7)
    c: Coincident(g7,g2)
    c: Equal(g2, g3-g7) x5
    c: PointOnObject(g2,g8)
    c: PointOnObject(g3,g8)
    c: PointOnObject(g4,g8)
    c: PointOnObject(g5,g8)
    c: PointOnObject(g6,g8)
    c: PointOnObject(g7,g8)
    c: Coincident(g9,g8)
    c: Coincident(g9,g0)
    c: PointOnObject(g2,g9)
    c: Angle(g9,g0) = 0.785398
    c: Radius(g8) = 9
    c: Distance(g9) = 20
    c: Coincident(g10,g11)
    c: Coincident(g11,g12)
    c: Coincident(g12,g13)
    c: Coincident(g13,g14)
    c: Coincident(g14,g15)
    c: Coincident(g15,g10)
    c: Equal(g10, g11-g15) x5
    c: PointOnObject(g10,g16)
    c: PointOnObject(g11,g16)
    c: PointOnObject(g12,g16)
    c: PointOnObject(g13,g16)
    c: PointOnObject(g14,g16)
    c: PointOnObject(g15,g16)
    c: Symmetric(g10,g2,g0)
    c: Symmetric(g16,g8,g0)
    c: Coincident(g17,g18)
    c: Coincident(g18,g19)
    c: Coincident(g19,g20)
    c: Coincident(g20,g21)
    c: Coincident(g21,g22)
    c: Coincident(g22,g17)
    c: Equal(g17, g18-g22) x5
    c: PointOnObject(g17,g23)
    c: PointOnObject(g18,g23)
    c: PointOnObject(g19,g23)
    c: PointOnObject(g20,g23)
    c: PointOnObject(g21,g23)
    c: PointOnObject(g22,g23)
    c: Symmetric(g18,g10,g1)
    c: Symmetric(g23,g16,g1)
    c: Coincident(g24,g25)
    c: Coincident(g25,g26)
    c: Coincident(g26,g27)
    c: Coincident(g27,g28)
    c: Coincident(g28,g29)
    c: Coincident(g29,g24)
    c: Equal(g24, g25-g29) x5
    c: PointOnObject(g24,g30)
    c: PointOnObject(g25,g30)
    c: PointOnObject(g26,g30)
    c: PointOnObject(g27,g30)
    c: PointOnObject(g28,g30)
    c: PointOnObject(g29,g30)
    c: Symmetric(g26,g2,g1)
    c: Symmetric(g30,g8,g1)
FEATURE [PartDesign::Pocket] Pocket015  label="[Vaciado]_Hexagonos_Grandes_Rueda"
  Length = 5
  Sketch = -> Sketch030
  Type = 1
FEATURE [Sketcher::SketchObject] Sketch031  label="[Croquis]_Hexagonos_Pequeños_Rueda"
  ExternalGeometry = -> [Pocket015]
  Placement = pos=(0,-54,0) rot=(1,0,0;1.5708rad)
  Support = -> Pocket015 [Face2]
  sketch-geometry (32):
    g0: LineSegment StartX=17.25 StartY=34.6029 StartZ=0 EndX=21.75 EndY=34.6029 EndZ=0
    g1: LineSegment StartX=21.75 StartY=34.6029 StartZ=0 EndX=24 EndY=38.5 EndZ=0
    g2: LineSegment StartX=24 StartY=38.5 StartZ=0 EndX=21.75 EndY=42.3971 EndZ=0
    g3: LineSegment StartX=21.75 StartY=42.3971 StartZ=0 EndX=17.25 EndY=42.3971 EndZ=0
    g4: LineSegment StartX=17.25 StartY=42.3971 StartZ=0 EndX=15 EndY=38.5 EndZ=0
    g5: LineSegment StartX=15 StartY=38.5 StartZ=0 EndX=17.25 EndY=34.6029 EndZ=0
    g6: Circle [constr] CenterX=19.5 CenterY=38.5 CenterZ=0 NormalX=0 NormalY=0 NormalZ=1 Radius=4.5
    g7: LineSegment [constr] StartX=19.5 StartY=13.5 StartZ=0 EndX=19.5 EndY=38.5 EndZ=0
    g8: LineSegment StartX=40.6029 StartY=11.25 StartZ=0 EndX=44.5 EndY=9 EndZ=0
    g9: LineSegment StartX=44.5 StartY=9 StartZ=0 EndX=48.3971 EndY=11.25 EndZ=0
    g10: LineSegment StartX=48.3971 StartY=11.25 StartZ=0 EndX=48.3971 EndY=15.75 EndZ=0
    g11: LineSegment StartX=48.3971 StartY=15.75 StartZ=0 EndX=44.5 EndY=18 EndZ=0
    g12: LineSegment StartX=44.5 StartY=18 StartZ=0 EndX=40.6029 EndY=15.75 EndZ=0
    g13: LineSegment StartX=40.6029 StartY=15.75 StartZ=0 EndX=40.6029 EndY=11.25 EndZ=0
    g14: Circle [constr] CenterX=44.5 CenterY=13.5 CenterZ=0 NormalX=0 NormalY=0 NormalZ=1 Radius=4.5
    g15: LineSegment [constr] StartX=19.5 StartY=13.5 StartZ=0 EndX=44.5 EndY=13.5 EndZ=0
    g16: LineSegment StartX=-5.5 StartY=9 StartZ=0 EndX=-1.60289 EndY=11.25 EndZ=0
    g17: LineSegment StartX=-1.60289 StartY=11.25 StartZ=0 EndX=-1.60289 EndY=15.75 EndZ=0
    g18: LineSegment StartX=-1.60289 StartY=15.75 StartZ=0 EndX=-5.5 EndY=18 EndZ=0
    g19: LineSegment StartX=-5.5 StartY=18 StartZ=0 EndX=-9.39711 EndY=15.75 EndZ=0
    g20: LineSegment StartX=-9.39711 StartY=15.75 StartZ=0 EndX=-9.39711 EndY=11.25 EndZ=0
    g21: LineSegment StartX=-9.39711 StartY=11.25 StartZ=0 EndX=-5.5 EndY=9 EndZ=0
    g22: Circle [constr] CenterX=-5.5 CenterY=13.5 CenterZ=0 NormalX=0 NormalY=0 NormalZ=1 Radius=4.5
    g23: LineSegment [constr] StartX=-5.5 StartY=13.5 StartZ=0 EndX=19.5 EndY=13.5 EndZ=0
    g24: LineSegment StartX=17.25 StartY=-15.3971 StartZ=0 EndX=21.75 EndY=-15.3971 EndZ=0
    g25: LineSegment StartX=21.75 StartY=-15.3971 StartZ=0 EndX=24 EndY=-11.5 EndZ=0
    g26: LineSegment StartX=24 StartY=-11.5 StartZ=0 EndX=21.75 EndY=-7.60289 EndZ=0
    g27: LineSegment StartX=21.75 StartY=-7.60289 StartZ=0 EndX=17.25 EndY=-7.60289 EndZ=0
    g28: LineSegment StartX=17.25 StartY=-7.60289 StartZ=0 EndX=15 EndY=-11.5 EndZ=0
    g29: LineSegment StartX=15 StartY=-11.5 StartZ=0 EndX=17.25 EndY=-15.3971 EndZ=0
    g30: Circle [constr] CenterX=19.5 CenterY=-11.5 CenterZ=0 NormalX=0 NormalY=0 NormalZ=1 Radius=4.5
    g31: LineSegment [constr] StartX=19.5 StartY=13.5 StartZ=0 EndX=19.5 EndY=-11.5 EndZ=0
  constraints (76):
    c: Coincident(g0,g1)
    c: Coincident(g1,g2)
    c: Coincident(g2,g3)
    c: Coincident(g3,g4)
    c: Coincident(g4,g5)
    c: Coincident(g5,g0)
    c: Equal(g0, g1-g5) x5
    c: PointOnObject(g0,g6)
    c: PointOnObject(g1,g6)
    c: PointOnObject(g2,g6)
    c: PointOnObject(g3,g6)
    c: PointOnObject(g4,g6)
    c: PointOnObject(g5,g6)
    c: Coincident(g7,g-3)
    c: Vertical(g7)
    c: Radius(g6) = 4.5
    c: Coincident(g6,g7)
    c: DistanceY(g7) = 25
    c: Horizontal(g0)
    c: Coincident(g8,g9)
    c: Coincident(g9,g10)
    c: Coincident(g10,g11)
    c: Coincident(g11,g12)
    c: Coincident(g12,g13)
    c: Coincident(g13,g8)
    c: Equal(g8, g9-g13) x5
    c: PointOnObject(g8,g14)
    c: PointOnObject(g9,g14)
    c: PointOnObject(g10,g14)
    c: PointOnObject(g11,g14)
    c: PointOnObject(g12,g14)
    c: PointOnObject(g13,g14)
    c: Coincident(g15,g7)
    c: Coincident(g15,g14)
    c: Horizontal(g15)
    c: Equal(g15,g7)
    c: Equal(g14,g6)
    c: Vertical(g13)
    c: Coincident(g16,g17)
    c: Coincident(g17,g18)
    c: Coincident(g18,g19)
    c: Coincident(g19,g20)
    c: Coincident(g20,g21)
    c: Coincident(g21,g16)
    c: Equal(g16, g17-g21) x5
    c: PointOnObject(g16,g22)
    c: PointOnObject(g17,g22)
    c: PointOnObject(g18,g22)
    c: PointOnObject(g19,g22)
    c: PointOnObject(g20,g22)
    c: PointOnObject(g21,g22)
    c: Equal(g22,g6)
    c: Vertical(g17)
    c: Coincident(g23,g22)
    c: Coincident(g23,g7)
    c: Equal(g23,g7)
    c: Horizontal(g23)
    c: Coincident(g24,g25)
    c: Coincident(g25,g26)
    c: Coincident(g26,g27)
    c: Coincident(g27,g28)
    c: Coincident(g28,g29)
    c: Coincident(g29,g24)
    c: Equal(g24, g25-g29) x5
    c: PointOnObject(g24,g30)
    c: PointOnObject(g25,g30)
    c: PointOnObject(g26,g30)
    c: PointOnObject(g27,g30)
    c: PointOnObject(g28,g30)
    c: PointOnObject(g29,g30)
    c: Equal(g30,g6)
    c: Horizontal(g27)
    c: Coincident(g31,g7)
    c: Coincident(g31,g30)
    c: Vertical(g31)
    c: Equal(g31,g7)
FEATURE [PartDesign::Pocket] Pocket016  label="[Vaciado]_Hexagonos_Pequeños_Rueda"
  Length = 5
  Sketch = -> Sketch031
  Type = 1
FEATURE [Part::Fillet] Fillet013  label="[Redondeo_]_Hexagonos_Rueda"
  Base = -> Pocket016
  Edges = 48 edges: [Edge181 r=3,Edge182 r=3,Edge183 r=3,Edge184 r=3,Edge185 r=3,Edge186 r=3,Edge187 r=3,Edge188 r=3,Edge189 r=3,Edge190 r=3,Edge191 r=3,Edge192 r=3,Edge193 r=3,Edge194 r=3,Edge195 r=3,Edge196 r=3,Edge197 r=3,Edge198 r=3,Edge199 r=3,Edge200 r=3,Edge201 r=3,Edge202 r=3,Edge203 r=3,Edge204 r=3,Edge205 r=1,Edge206 r=1,Edge207 r=1,Edge208 r=1,Edge209 r=1,Edge210 r=1,Edge211 r=1,Edge212 r=1,Edge213 r=1,Edge214 r=1,Edge215 r=1,Edge216 r=1,Edge217 r=1,Edge218 r=1,Edge219 r=1,Edge220 r=1,Edge221 r=1,Edge222 r=1,Edge223 r=1,Edge224 r=1,Edge225 r=1,Edge226 r=1,Edge227 r=1,Edge228 r=1]
FEATURE [Part::Cylinder] Cylinder041  label="Cylinder001"
  Angle = 360
  Height = 2
  Placement = pos=(19.5,-52,13.5) rot=(1,0,0;1.5708rad)
  Radius = 30
FEATURE [Part::Cut] Cut023  label="[Diferencia]_Rueda_Cilindro"
  Base = -> Fillet013
  Tool = -> Cylinder041
FEATURE [Part::Sphere] Sphere006  label="Esfera_Rueda"
  Angle1 = -90
  Angle2 = 90
  Angle3 = 360
  Placement = pos=(19.5,-49,13.5) rot=(0,0,1;0rad)
  Radius = 5.5
FEATURE [Part::Cut] Cut024  label="[Diferencia]_Rueda_Esfera"
  Base = -> Cut023
  Tool = -> Sphere006
FEATURE [Part::Fillet] Fillet014  label="[Redondeo]_Rueda_Exterior"
  Base = -> Cut024
  Edges = 6 edges: [Edge1 r=1,Edge2 r=0.99,Edge4 r=1,Edge6 r=1,Edge374 r=2,Edge376 r=2]
FEATURE [Part::Cut] Cut025  label="RUEDA_1--[Diferencia]_Rueda_Toroide"
  Base = -> Fillet014
  Placement = pos=(0,-1,0) rot=(0,0,1;0rad)
  Tool = -> Torus001
FEATURE [Part::Fillet] Fillet015  label="[Redondeo]_Rueda_Interior"
  Base = -> Cut024
  Edges = 6 edges: [Edge1 r=1,Edge2 r=0.99,Edge4 r=1,Edge6 r=1,Edge374 r=2,Edge376 r=2]
FEATURE [Part::Torus] Torus003  label="Toroide_neumatico_2"
  Angle1 = -180
  Angle2 = 180
  Angle3 = 360
  Placement = pos=(19.5,51,13.5) rot=(1,0,0;1.5708rad)
  Radius1 = 32
  Radius2 = 2
FEATURE [Part::Chamfer] Chamfer007
  Base = -> Chamfer
  Edges = 1 edges r=0.3: [Edge135]
FEATURE [Part::Fillet] Fillet016  label="Horn_Rueda_2"
  Base = -> Chamfer007
  Edges = 1 edges r=0.1: [Edge8]
  Placement = pos=(19.5,51,13.5) rot=(-1,0,0;1.5708rad)
FEATURE [App::DocumentObjectGroup] Group027  label="Ruedas_Horn"
  Group = -> [Fillet016,Fillet006]
FEATURE [App::DocumentObjectGroup] Group028  label="Ruedas_Neumatico"
  Group = -> [Torus003,Torus]
FEATURE [Part::Feature] Part__Feature179  label="Tornillo_M3x25_Ultrasonido1"
  Placement = pos=(52,-7,22) rot=(1,0,0;3.14159rad)
  shape: bbox 6.148 x 6.148 x 28 mm, 376 faces (baked)
FEATURE [Part::Feature] Part__Feature180  label="Tornillo_M3x25_Ultrasonido2"
  Placement = pos=(52,19,22) rot=(1,0,0;3.14159rad)
  shape: bbox 6.148 x 6.148 x 28 mm, 376 faces (baked)
FEATURE [App::DocumentObjectGroup] Group021  label="Ultrasonidos_Tornillos"
  Group = -> [Part__Feature128,Part__Feature129,Part__Feature133,Part__Feature136,Part__Feature135,Part__Feature179,Part__Feature180]
FEATURE [Part::Feature] Part__Feature181  label="Tornillo_M3x25_ZUM_1"
  Placement = pos=(-17,-24,50) rot=(1,0,0;3.14159rad)
  shape: bbox 6.148 x 6.148 x 28 mm, 376 faces (baked)
FEATURE [Part::Feature] Part__Feature182  label="Tornillo_M3x25_ZUM_2"
  Placement = pos=(35,-19,50) rot=(1,0,0;3.14159rad)
  shape: bbox 6.148 x 6.148 x 28 mm, 376 faces (baked)
FEATURE [Part::Feature] Part__Feature183  label="Tornillo_M3x25_ZUM_3"
  Placement = pos=(35,9,50) rot=(1,0,0;3.14159rad)
  shape: bbox 6.148 x 6.148 x 28 mm, 376 faces (baked)
FEATURE [Part::Feature] Part__Feature184  label="Tornillo_M3x25_ZUM_4"
  Placement = pos=(-15.75,24.3,50) rot=(1,0,0;3.14159rad)
  shape: bbox 6.148 x 6.148 x 28 mm, 376 faces (baked)
FEATURE [Part::Feature] Part__Feature185  label="TuercaM3_ZUM_Cuerpo_1"
  Placement = pos=(35.5,20,8.5) rot=(0,0,1;0rad)
  shape: bbox 6.929 x 6.929 x 2.801 mm, 56 faces (baked)
FEATURE [Part::Feature] Part__Feature186  label="TuercaM3_ZUM_Cuerpo_2"
  Placement = pos=(35.5,-20,8.5) rot=(0,0,1;0rad)
  shape: bbox 6.929 x 6.929 x 2.801 mm, 56 faces (baked)
FEATURE [Part::Feature] Part__Feature187  label="TuercaM3_ZUM_Cuerpo_3"
  Placement = pos=(-17.5,-20,8.5) rot=(0,0,1;0rad)
  shape: bbox 6.929 x 6.929 x 2.801 mm, 56 faces (baked)
FEATURE [Part::Feature] Part__Feature188  label="TuercaM3_ZUM_Cuerpo_4"
  Placement = pos=(-17.5,20,8.5) rot=(0,0,1;0rad)
  shape: bbox 6.929 x 6.929 x 2.801 mm, 56 faces (baked)
FEATURE [Part::Feature] Part__Feature189  label="TuercaM3_ZUM_Cuerpo_5"
  Placement = pos=(35,9,29) rot=(0,0,1;0rad)
  shape: bbox 6.929 x 6.929 x 2.801 mm, 56 faces (baked)
FEATURE [Part::Feature] Part__Feature190  label="TuercaM3_ZUM_Cuerpo_6"
  Placement = pos=(35,-18.75,29.5) rot=(0,0,1;0rad)
  shape: bbox 6.929 x 6.929 x 2.801 mm, 56 faces (baked)
FEATURE [Part::Feature] Part__Feature191  label="TuercaM3_ZUM_Cuerpo_7"
  Placement = pos=(-17,24.4,29.5) rot=(0,0,1;0rad)
  shape: bbox 6.929 x 6.929 x 2.801 mm, 56 faces (baked)
FEATURE [Part::Feature] Part__Feature192  label="TuercaM3_ZUM_Cuerpo_8"
  Placement = pos=(-17,-24,29.5) rot=(0,0,1;0rad)
  shape: bbox 6.929 x 6.929 x 2.801 mm, 56 faces (baked)
FEATURE [App::DocumentObjectGroup] Group007  label="ZUM_Tuercas"
  Group = -> [Part__Feature185,Part__Feature186,Part__Feature187,Part__Feature188,Part__Feature189,Part__Feature190,Part__Feature191,Part__Feature192]
FEATURE [Part::Feature] Part__Feature193  label="TornilloM3x8_ZUM_1"
  Placement = pos=(35.5,-19.9,0) rot=(0,0,1;0rad)
  shape: bbox 5.953 x 5.953 x 11 mm, 174 faces (baked)
FEATURE [Part::Feature] Part__Feature194  label="TornilloM3x8_ZUM_2"
  Placement = pos=(35.5,19.9,0) rot=(0,0,1;0rad)
  shape: bbox 5.953 x 5.953 x 11 mm, 174 faces (baked)
FEATURE [Part::Feature] Part__Feature195  label="TornilloM3x8_ZUM_3"
  Placement = pos=(-17.5,19.9,0) rot=(0,0,1;0rad)
  shape: bbox 5.953 x 5.953 x 11 mm, 174 faces (baked)
FEATURE [Part::Feature] Part__Feature196  label="TornilloM3x8_ZUM_4"
  Placement = pos=(-17.5,-20.1,0) rot=(0,0,1;0rad)
  shape: bbox 5.953 x 5.953 x 11 mm, 174 faces (baked)
FEATURE [App::DocumentObjectGroup] Group006  label="ZUM_Tornillos"
  Group = -> [Part__Feature181,Part__Feature182,Part__Feature183,Part__Feature184,Part__Feature193,Part__Feature194,Part__Feature195,Part__Feature196]
FEATURE [Sketcher::SketchObject] Sketch033  label="[Croquis]_Rueda_Tapa"
  Placement = pos=(19.5,-57,13.5) rot=(1,0,0;1.5708rad)
  sketch-geometry (14):
    g0: LineSegment StartX=-6.62347 StartY=6.62347 StartZ=0 EndX=-3 EndY=20.1464 EndZ=0
    g1: LineSegment StartX=-3 StartY=20.1464 StartZ=0 EndX=3 EndY=20.1464 EndZ=0
    g2: LineSegment StartX=3 StartY=20.1464 StartZ=0 EndX=6.62347 EndY=6.62347 EndZ=0
    g3: LineSegment StartX=-6.62347 StartY=6.62347 StartZ=0 EndX=-20.1464 EndY=3 EndZ=0
    g4: LineSegment [constr] StartX=-6.62347 StartY=6.62347 StartZ=0 EndX=0 EndY=0 EndZ=0
    g5: LineSegment StartX=-20.1464 StartY=3 StartZ=0 EndX=-20.1464 EndY=-3 EndZ=0
    g6: LineSegment StartX=-20.1464 StartY=-3 StartZ=0 EndX=-6.62347 EndY=-6.62347 EndZ=0
    g7: LineSegment StartX=6.62347 StartY=6.62347 StartZ=0 EndX=20.1464 EndY=3 EndZ=0
    g8: LineSegment StartX=20.1464 StartY=3 StartZ=0 EndX=20.1464 EndY=-3 EndZ=0
    g9: LineSegment StartX=20.1464 StartY=-3 StartZ=0 EndX=6.62347 EndY=-6.62347 EndZ=0
    g10: LineSegment StartX=6.62347 StartY=-6.62347 StartZ=0 EndX=3 EndY=-20.1464 EndZ=0
    g11: LineSegment StartX=3 StartY=-20.1464 StartZ=0 EndX=-3 EndY=-20.1464 EndZ=0
    g12: LineSegment StartX=-3 StartY=-20.1464 StartZ=0 EndX=-6.62347 EndY=-6.62347 EndZ=0
    g13: LineSegment [constr] StartX=0 StartY=0 StartZ=0 EndX=6.62347 EndY=-6.62347 EndZ=0
  constraints (41):
    c: Coincident(g1,g0)
    c: Horizontal(g1)
    c: Coincident(g2,g1)
    c: Coincident(g3,g0)
    c: Coincident(g4,g0)
    c: Coincident(g4,g-1)
    c: Angle(g-2,g4) = 0.785398
    c: Angle(g4,g0) = 2.0944
    c: Symmetric(g0,g1,g-2)
    c: Coincident(g5,g3)
    c: Vertical(g5)
    c: Equal(g5,g1)
    c: Equal(g0,g3)
    c: Coincident(g6,g5)
    c: Coincident(g7,g2)
    c: Coincident(g7,g8)
    c: Vertical(g8)
    c: Coincident(g8,g9)
    c: Coincident(g9,g10)
    c: Coincident(g10,g11)
    c: Horizontal(g11)
    c: Coincident(g11,g12)
    c: Coincident(g12,g6)
    c: Equal(g9,g7)
    c: Equal(g7,g2)
    c: Equal(g2,g10)
    c: Equal(g10,g12)
    c: Equal(g12,g6)
    c: Equal(g6,g3)
    c: Equal(g1,g8)
    c: Equal(g8,g11)
    c: Equal(g11,g5)
    c: Symmetric(g8,g7,g-1)
    c: Symmetric(g10,g11,g-2)
    c: Symmetric(g5,g3,g-1)
    c: Coincident(g13,g-1)
    c: Coincident(g13,g9)
    c: Equal(g13,g4)
    c: Angle(g13,g-1) = 0.785398
    c: Distance(g0) = 14
    c: DistanceX(g1) = 6
FEATURE [PartDesign::Pad] Pad007  label="[Extrusion]_Rueda_Tapa"
  Length = 2
  Length2 = 100
  Placement = pos=(19.5,-57,13.5) rot=(1,0,0;1.5708rad)
  Sketch = -> Sketch033
  Type = 0
FEATURE [Part::Fillet] Fillet017  label="[Redondeado]_Rueda_Tapa_Aristas_Laterales"
  Base = -> Pad007
  Edges = 12 edges r=2: [Edge1,Edge2,Edge5,Edge8,Edge11,Edge14,Edge17,Edge20,Edge23,Edge26,Edge29,Edge32]
FEATURE [Part::Cylinder] Cylinder042  label="Taladro_Tornillo_Tapa_Rueda"
  Angle = 360
  Height = 10
  Placement = pos=(19.5,-46,13.5) rot=(1,0,0;1.5708rad)
  Radius = 1.75
FEATURE [Sketcher::SketchObject] Sketch034  label="Rueda_Tapa_Hexagono"
  Placement = pos=(19.5,-59,13.5) rot=(1,0,0;1.5708rad)
  sketch-geometry (7):
    g0: LineSegment StartX=-3.5 StartY=-6.06218 StartZ=0 EndX=3.5 EndY=-6.06218 EndZ=0
    g1: LineSegment StartX=3.5 StartY=-6.06218 StartZ=0 EndX=7 EndY=0 EndZ=0
    g2: LineSegment StartX=7 StartY=0 StartZ=0 EndX=3.5 EndY=6.06218 EndZ=0
    g3: LineSegment StartX=3.5 StartY=6.06218 StartZ=0 EndX=-3.5 EndY=6.06218 EndZ=0
    g4: LineSegment StartX=-3.5 StartY=6.06218 StartZ=0 EndX=-7 EndY=0 EndZ=0
    g5: LineSegment StartX=-7 StartY=0 StartZ=0 EndX=-3.5 EndY=-6.06218 EndZ=0
    g6: Circle [constr] CenterX=0 CenterY=0 CenterZ=0 NormalX=0 NormalY=0 NormalZ=1 Radius=7
  constraints (17):
    c: Coincident(g0,g1)
    c: Coincident(g1,g2)
    c: Coincident(g2,g3)
    c: Coincident(g3,g4)
    c: Coincident(g4,g5)
    c: Coincident(g5,g0)
    c: Equal(g0, g1-g5) x5
    c: PointOnObject(g0,g6)
    c: PointOnObject(g1,g6)
    c: PointOnObject(g2,g6)
    c: PointOnObject(g3,g6)
    c: PointOnObject(g4,g6)
    c: PointOnObject(g5,g6)
    c: Coincident(g3,g-1)
    c: Coincident(g6,g-1)
    c: Horizontal(g3)
    c: Radius(g6) = 7
FEATURE [PartDesign::Pad] Pad008  label="[Extrusion]_Rueda_Tapa_Hexagono"
  Length = 2
  Length2 = 100
  Placement = pos=(19.5,-59,13.5) rot=(1,0,0;1.5708rad)
  Sketch = -> Sketch034
  Type = 0
FEATURE [Part::Fillet] Fillet018  label="[Redondeado]_Rueda_Tapa_Aristas_Frontales"
  Base = -> Fillet017
  Edges = 3 edges r=1.9: [Edge4,Edge29,Edge32]
  Placement = pos=(0,4,0) rot=(0,0,1;0rad)
FEATURE [Part::Fillet] Fillet019  label="[Redondeado]_Rueda_Tapa_Hexagono"
  Base = -> Pad008
  Edges = 6 edges r=1: [Edge1,Edge2,Edge5,Edge8,Edge11,Edge14]
FEATURE [Part::Fillet] Fillet020  label="[Redondeado]_Rueda_Tapa_Hexagono_Frontal"
  Base = -> Fillet019
  Edges = 3 edges r=1: [Edge24,Edge26,Edge28]
  Placement = pos=(0,5,0) rot=(0,0,1;0rad)
FEATURE [Part::MultiFuse] Fusion041  label="[Fusion]_Tapa_Rueda"
  Shapes = -> [Fillet020,Fillet018]
FEATURE [Part::Cylinder] Cylinder043  label="Taladro_Tornillo_Cabeza_Tapa_Rueda"
  Angle = 360
  Height = 2
  Placement = pos=(19.5,-54,13.5) rot=(1,0,0;1.5708rad)
  Radius = 4.25
FEATURE [Part::MultiFuse] Fusion042  label="[Fusion]_Taladros_Tapa_Rueda"
  Shapes = -> [Cylinder043,Cylinder042]
FEATURE [Part::Cut] Cut027  label="Tapa_Rueda_1"
  Base = -> Fusion041
  Tool = -> Fusion042
FEATURE [Part::MultiFuse] Fusion043  label="[Fusion]_Tapa_Rueda001"
  Shapes = -> [Fillet020,Fillet018]
FEATURE [Part::MultiFuse] Fusion044  label="[Fusion]_Taladros_Tapa_Rueda001"
  Shapes = -> [Cylinder043,Cylinder042]
FEATURE [Part::Cut] Cut028  label="Tapa_Rueda_2"
  Base = -> Fusion043
  Placement = pos=(39,0,0) rot=(0,0,1;3.14159rad)
  Tool = -> Fusion044
FEATURE [App::DocumentObjectGroup] Group031  label="Ruedas_Tapas"
  Group = -> [Cut027,Cut028]
FEATURE [Part::Fillet] Fillet022  label="[Redondeo]_Rueda_Exterior001"
  Base = -> Cut024
  Edges = 6 edges: [Edge1 r=1,Edge2 r=0.99,Edge4 r=1,Edge6 r=1,Edge374 r=2,Edge376 r=2]
FEATURE [Part::Torus] Torus004  label="Toroide_neumatico_resta001"
  Angle1 = -180
  Angle2 = 180
  Angle3 = 360
  Placement = pos=(19.5,-50,13.5) rot=(1,0,0;1.5708rad)
  Radius1 = 32
  Radius2 = 2.5
FEATURE [Part::Cut] Cut029  label="RUEDA_2--[Diferencia]_Rueda_Toroide"
  Base = -> Fillet022
  Placement = pos=(39,1,0) rot=(0,0,1;3.14159rad)
  Tool = -> Torus004
FEATURE [App::DocumentObjectGroup] Group030  label="Ruedas_Printbot"
  Group = -> [Cylinder018,Pocket011,Cut022,Pocket015,Cut025,Torus001,Fillet013,Fillet015,Cut029]
FEATURE [App::DocumentObjectGroup] Group010  label="Ruedas"
  Group = -> [Group020,Group027,Group028,Group030,Group031]
FEATURE [Part::Box] Box040  label="Cubo_Resta_Ultrasonido"
  Height = 10
  Length = 11
  Placement = pos=(41,-5,29) rot=(0,0,1;0rad)
  Width = 10
FEATURE [Part::Cylinder] Cylinder044  label="Cilindro_Resta_Ultrasonido"
  Angle = 360
  Height = 10
  Placement = pos=(53,0,29) rot=(0,0,1;0rad)
  Radius = 4.6
FEATURE [Part::Cut] Cut030  label="[Diferencia]_Ultrasonido_Cubo_Cilindro"
  Base = -> Box040
  Placement = pos=(1,0.1,0) rot=(0,0,1;0rad)
  Tool = -> Cylinder044
FEATURE [Part::MultiFuse] Fusion045  label="[Union]_Ultrasonido_Huecos_Taladros"
  Shapes = -> [Cut030,Fusion027]
FEATURE [Sketcher::SketchObject] Sketch035  label="[Croquis]_Ultrasonido_PCB"
  ExternalGeometry = -> [Pocket012]
  Placement = pos=(66,-27.9,31) rot=(0,-1,0;1.5708rad)
  Support = -> Pocket012 [Face3]
  sketch-geometry (9):
    g0: ArcOfCircle CenterX=10 CenterY=51.5 CenterZ=0 NormalX=0 NormalY=0 NormalZ=1 Radius=2 StartAngle=4.71239 EndAngle=6.28319
    g1: ArcOfCircle CenterX=9.99998 CenterY=39.5 CenterZ=0 NormalX=0 NormalY=0 NormalZ=1 Radius=9.99998 StartAngle=1.57079 EndAngle=3.14159
    g2: ArcOfCircle CenterX=10 CenterY=4.5 CenterZ=0 NormalX=0 NormalY=0 NormalZ=1 Radius=2 StartAngle=1.2894e-08 EndAngle=1.5708
    g3: ArcOfCircle CenterX=9.99998 CenterY=16.5 CenterZ=0 NormalX=0 NormalY=0 NormalZ=1 Radius=9.99998 StartAngle=3.14159 EndAngle=4.71239
    g4: LineSegment StartX=12 StartY=51.5 StartZ=0 EndX=12 EndY=4.5 EndZ=0
    g5: LineSegment StartX=0 StartY=39.5 StartZ=0 EndX=0 EndY=16.5 EndZ=0
    g6: LineSegment [constr] StartX=12 StartY=28 StartZ=0 EndX=0 EndY=28 EndZ=0
    g7: LineSegment [constr] StartX=12 StartY=51.5 StartZ=0 EndX=12 EndY=28 EndZ=0
    g8: LineSegment [constr] StartX=10 StartY=56 StartZ=0 EndX=10 EndY=49.5 EndZ=0
  constraints (27):
    c: PointOnObject(g8,g-4)
    c: PointOnObject(g0,g-3)
    c: Radius(g0) = 2
    c: Coincident(g1,g0)
    c: PointOnObject(g1,g-5)
    c: Tangent(g1,g-5)
    c: Tangent(g1,g0)
    c: PointOnObject(g2,g-3)
    c: Equal(g2,g0)
    c: Tangent(g2,g-3)
    c: Coincident(g3,g2)
    c: PointOnObject(g3,g-5)
    c: Tangent(g2,g3)
    c: Coincident(g4,g0)
    c: Coincident(g4,g2)
    c: Equal(g3,g1)
    c: Coincident(g5,g1)
    c: Coincident(g5,g3)
    c: PointOnObject(g6,g4)
    c: PointOnObject(g6,g-2)
    c: Horizontal(g6)
    c: Coincident(g7,g0)
    c: Coincident(g7,g6)
    c: DistanceY(g7) = -23.5
    c: Symmetric(g1,g3,g6)
    c: Vertical(g8)
    c: Coincident(g8,g0)
FEATURE [PartDesign::Pocket] Pocket017  label="[Vaciado]_Ultrasonido_PCB"
  Length = 5
  Placement = pos=(68,-27.9,31) rot=(0,-1,0;1.5708rad)
  Sketch = -> Sketch035
  Type = 0
FEATURE [Part::Cut] Cut031  label="[Diferencia]_Ultrasonido_Huecos"
  Base = -> Pocket017
  Tool = -> Fusion045
FEATURE [Part::Fillet] Fillet023  label="[Redondeado]_Ultrasonido_Huecos"
  Base = -> Cut031
  Edges = 5 edges r=2: [Edge4,Edge24,Edge25,Edge46,Edge48]
  Placement = pos=(0,0,50) rot=(0,0,1;0rad)
FEATURE [Part::Sphere] Sphere007  label="Ultrasonidos_Esfera"
  Angle1 = -90
  Angle2 = 90
  Angle3 = 360
  Placement = pos=(61,0.05,77.5) rot=(0,0,1;0rad)
  Radius = 3.2
FEATURE [Part::Cut] Cut032  label="[Diferencia]_Ultrasonido_Huecos_Esfera"
  Base = -> Fillet023
  Placement = pos=(0,0,-46.5) rot=(0,0,1;0rad)
  Tool = -> Sphere007
FEATURE [Part::Feature] Part__Feature114  label="TuercaM3_LDR2"
  Placement = pos=(75.5,18,0) rot=(0,0,1;0rad)
  shape: bbox 6.929 x 6.929 x 2.801 mm, 56 faces (baked)
FEATURE [Part::MultiFuse] Fusion020  label="Tuercas_sensores001"
  Placement = pos=(8,0,0) rot=(0,0,1;0rad)
  Shapes = -> [Part__Feature114,Part__Feature115,Part__Feature118,Part__Feature117,Part__Feature119,Part__Feature116]
FEATURE [App::DocumentObjectGroup] Group009  label="Sensores_Tuercas"
  Group = -> [Part__Feature114,Part__Feature115,Part__Feature116,Part__Feature117,Part__Feature118,Part__Feature119,Fusion020]
FEATURE [Sketcher::SketchObject] Sketch036
  sketch-geometry (8):
    g0: ArcOfCircle CenterX=-85.1605 CenterY=0 CenterZ=0 NormalX=0 NormalY=0 NormalZ=1 Radius=4 StartAngle=3.14159 EndAngle=3.95469
    g1: ArcOfCircle CenterX=-96.1565 CenterY=-11.6227 CenterZ=0 NormalX=0 NormalY=0 NormalZ=1 Radius=12 StartAngle=6.26222 EndAngle=7.09628
    g2: ArcOfCircle CenterX=-78.1605 CenterY=-12 CenterZ=0 NormalX=0 NormalY=0 NormalZ=1 Radius=6 StartAngle=3.12063 EndAngle=6.30415
    g3: ArcOfCircle CenterX=-71.1605 CenterY=-7.788e-09 CenterZ=0 NormalX=0 NormalY=0 NormalZ=1 Radius=4 StartAngle=5.47009 EndAngle=6.28319
    g4: ArcOfCircle CenterX=-60.1645 CenterY=-11.6227 CenterZ=0 NormalX=0 NormalY=0 NormalZ=1 Radius=12 StartAngle=2.3285 EndAngle=3.16255
    g5: LineSegment [constr] StartX=-78.1605 StartY=0 StartZ=0 EndX=-78.1605 EndY=-18 EndZ=0
    g6: LineSegment StartX=-89.1605 StartY=0 StartZ=0 EndX=-78.1605 EndY=0 EndZ=0
    g7: LineSegment StartX=-78.1605 StartY=0 StartZ=0 EndX=-67.1605 EndY=0 EndZ=0
  constraints (27):
    c: Coincident(g1,g0)
    c: Coincident(g2,g1)
    c: Coincident(g4,g3)
    c: Coincident(g4,g2)
    c: Tangent(g1,g2)
    c: Tangent(g4,g2)
    c: Tangent(g4,g3)
    c: Tangent(g1,g0)
    c: Equal(g0,g3)
    c: Vertical(g5)
    c: Symmetric(g1,g2,g5)
    c: Symmetric(g0,g3,g5)
    c: PointOnObject(g5,g2)
    c: Coincident(g6,g0)
    c: Coincident(g6,g5)
    c: Horizontal(g6)
    c: Coincident(g7,g5)
    c: Coincident(g7,g3)
    c: Horizontal(g7)
    c: DistanceX(g7) = 11
    c: Radius(g2) = 6
    c: Perpendicular(g0,g6)
    c: DistanceY(g5) = -18
    c: Radius(g1) = 12
    c: Radius(g0) = 4
    c: PointOnObject(g5,g-1)
    c: DistanceX(g-1,g3) = -67.1605
FEATURE [Sketcher::SketchObject] Sketch037
  Placement = pos=(-66,0,0) rot=(0.57735,-0.57735,-0.57735;2.0944rad)
  sketch-geometry (6):
    g0: ArcOfCircle CenterX=14.0605 CenterY=19.4746 CenterZ=0 NormalX=0 NormalY=0 NormalZ=1 Radius=15.4747 StartAngle=3.90571 EndAngle=4.70928
    g1: ArcOfCircle CenterX=0 CenterY=6 CenterZ=0 NormalX=0 NormalY=0 NormalZ=1 Radius=4 StartAngle=0.764125 EndAngle=1.5708
    g2: LineSegment StartX=0 StartY=18 StartZ=0 EndX=18 EndY=18 EndZ=0
    g3: LineSegment StartX=18 StartY=0 StartZ=0 EndX=18 EndY=18 EndZ=0
    g4: ArcOfCircle CenterX=14 CenterY=0 CenterZ=0 NormalX=0 NormalY=0 NormalZ=1 Radius=4 StartAngle=0 EndAngle=1.56769
    g5: LineSegment StartX=0 StartY=10 StartZ=0 EndX=0 EndY=18 EndZ=0
  constraints (21):
    c: Coincident(g1,g0)
    c: Tangent(g0,g1)
    c: PointOnObject(g3,g-1)
    c: PointOnObject(g1,g-2)
    c: Perpendicular(g1,g-2)
    c: Horizontal(g2)
    c: Vertical(g3)
    c: Coincident(g2,g3)
    c: PointOnObject(g4,g-1)
    c: Coincident(g4,g0)
    c: Coincident(g4,g3)
    c: Equal(g4,g1)
    c: Radius(g4) = 4
    c: Tangent(g4,g0)
    c: DistanceY(g3) = 18
    c: PointOnObject(g5,g-2)
    c: Vertical(g5)
    c: Coincident(g1,g5)
    c: Coincident(g2,g5)
    c: DistanceX(g2) = 18
    c: DistanceY(g5) = 8
FEATURE [Part::Fillet] Fillet026  label="BASE_FINAL[Redondeado]_Taladros_Base"
  Base = -> Pocket009
  Edges = 20 edges: [Edge1 r=5,Edge2 r=5,Edge11 r=5,Edge14 r=5,Edge17 r=8,Edge20 r=5,Edge23 r=5,Edge26 r=5,Edge29 r=5,Edge35 r=5,Edge38 r=5,Edge41 r=5,Edge44 r=5,Edge47 r=5,Edge50 r=5,Edge56 r=5,Edge59 r=5,Edge62 r=5,Edge65 r=5,Edge68 r=8]
FEATURE [Part::Cylinder] Cylinder045  label="Cylinder"
  Angle = 360
  Height = 10
  Placement = pos=(-44,-38,-2) rot=(0,0,1;0rad)
  Radius = 1.75
FEATURE [Part::Cylinder] Cylinder048  label="Cylinder004"
  Angle = 360
  Height = 8
  Placement = pos=(-44,-38,5) rot=(0,0,1;0rad)
  Radius = 2.75
FEATURE [Part::Feature] bq_logo007_solid  label="bq_logo002 (Solid)"
  Placement = pos=(-56,0,15) rot=(-0.57735,-0.57735,0.57735;2.0944rad)
  shape: bbox 3 x 25 x 21.48 mm, 152 faces (baked)
FEATURE [PartDesign::Pad] Pad010  label="[Extrusion_]Base001"
  Length = 2.8
  Length2 = 100
  Sketch = -> Sketch018
  Type = 0
FEATURE [Sketcher::SketchObject] Sketch038  label="[Croquis]_Taladros_Base_bis"
  ExternalGeometry = -> [Fillet026]
  Placement = pos=(0,0,0) rot=(1,0,0;3.14159rad)
  Support = -> Fillet026 [Face2]
  sketch-geometry (48):
    g0: LineSegment StartX=89.025 StartY=13 StartZ=0 EndX=111.275 EndY=13 EndZ=0
    g1: LineSegment StartX=111.275 StartY=13 StartZ=0 EndX=111.275 EndY=-13 EndZ=0
    g2: LineSegment StartX=111.275 StartY=-13 StartZ=0 EndX=89.025 EndY=-13 EndZ=0
    g3: LineSegment StartX=89.025 StartY=-13 StartZ=0 EndX=89.025 EndY=13 EndZ=0
    g4: Circle CenterX=98.9 CenterY=16 CenterZ=0 NormalX=0 NormalY=0 NormalZ=1 Radius=1.5
    g5: LineSegment StartX=73 StartY=35 StartZ=0 EndX=94 EndY=35 EndZ=0
    g6: LineSegment StartX=94 StartY=35 StartZ=0 EndX=94 EndY=21 EndZ=0
    g7: LineSegment StartX=94 StartY=21 StartZ=0 EndX=73 EndY=21 EndZ=0
    g8: LineSegment StartX=73 StartY=21 StartZ=0 EndX=73 EndY=35 EndZ=0
    g9: LineSegment StartX=73 StartY=-21 StartZ=0 EndX=94 EndY=-21 EndZ=0
    g10: LineSegment StartX=94 StartY=-21 StartZ=0 EndX=94 EndY=-35 EndZ=0
    g11: LineSegment StartX=94 StartY=-35 StartZ=0 EndX=73 EndY=-35 EndZ=0
    g12: LineSegment StartX=73 StartY=-35 StartZ=0 EndX=73 EndY=-21 EndZ=0
    g13: Circle CenterX=83.5 CenterY=38 CenterZ=0 NormalX=0 NormalY=0 NormalZ=1 Radius=1.5
    g14: Circle CenterX=83.5 CenterY=18 CenterZ=0 NormalX=0 NormalY=0 NormalZ=1 Radius=1.5
    g15: LineSegment [constr] StartX=83.5 StartY=18 StartZ=0 EndX=83.5 EndY=38 EndZ=0
    g16: LineSegment [constr] StartX=94 StartY=28 StartZ=0 EndX=73 EndY=28 EndZ=0
    g17: Circle CenterX=83.5 CenterY=-18 CenterZ=0 NormalX=0 NormalY=0 NormalZ=1 Radius=1.5
    g18: Circle CenterX=83.5 CenterY=-38 CenterZ=0 NormalX=0 NormalY=0 NormalZ=1 Radius=1.5
    g19: LineSegment [constr] StartX=83.5 StartY=28 StartZ=0 EndX=83.5 EndY=0 EndZ=0
    g20: LineSegment [constr] StartX=100.15 StartY=0 StartZ=0 EndX=83.5 EndY=0 EndZ=0
    g21: Circle CenterX=52 CenterY=6.8 CenterZ=0 NormalX=0 NormalY=0 NormalZ=1 Radius=1.5
    g22: LineSegment [constr] StartX=52 StartY=0 StartZ=0 EndX=52 EndY=6.8 EndZ=0
    g23: LineSegment [constr] StartX=52 StartY=0 StartZ=0 EndX=52 EndY=-18.8 EndZ=0
    g24: Circle CenterX=52 CenterY=-18.8 CenterZ=0 NormalX=0 NormalY=0 NormalZ=1 Radius=1.5
    g25: LineSegment [constr] StartX=52 StartY=0 StartZ=0 EndX=83.5 EndY=0 EndZ=0
    g26: Circle CenterX=35.5 CenterY=20 CenterZ=0 NormalX=0 NormalY=0 NormalZ=1 Radius=1.5
    g27: LineSegment [constr] StartX=35.5 StartY=20 StartZ=0 EndX=35.5 EndY=0 EndZ=0
    g28: LineSegment [constr] StartX=35.5 StartY=0 StartZ=0 EndX=52 EndY=0 EndZ=0
    g29: Circle CenterX=-16.5 CenterY=20 CenterZ=0 NormalX=0 NormalY=0 NormalZ=1 Radius=1.5
    g30: Circle CenterX=-16.5 CenterY=-20 CenterZ=0 NormalX=0 NormalY=0 NormalZ=1 Radius=1.5
    g31: Circle CenterX=35.5 CenterY=-20 CenterZ=0 NormalX=0 NormalY=0 NormalZ=1 Radius=1.5
    g32: LineSegment [constr] StartX=-16.5 StartY=0 StartZ=0 EndX=-16.5 EndY=20 EndZ=0
    g33: LineSegment [constr] StartX=-16.5 StartY=0 StartZ=0 EndX=35.5 EndY=0 EndZ=0
    g34: LineSegment [constr] StartX=-29 StartY=0 StartZ=0 EndX=-16.5 EndY=0 EndZ=0
    g35: Circle CenterX=98.9 CenterY=-16 CenterZ=0 NormalX=0 NormalY=0 NormalZ=1 Radius=1.5
    g36: Circle CenterX=62 CenterY=46 CenterZ=0 NormalX=0 NormalY=0 NormalZ=1 Radius=1.5
    g37: Circle CenterX=-23 CenterY=46 CenterZ=0 NormalX=0 NormalY=0 NormalZ=1 Radius=1.5
    g38: Circle CenterX=-23 CenterY=-46 CenterZ=0 NormalX=0 NormalY=0 NormalZ=1 Radius=1.5
    g39: Circle CenterX=62 CenterY=-46 CenterZ=0 NormalX=0 NormalY=0 NormalZ=1 Radius=1.5
    g40: LineSegment [constr] StartX=-23 StartY=46 StartZ=0 EndX=62 EndY=46 EndZ=0
    g41: LineSegment [constr] StartX=62 StartY=46 StartZ=0 EndX=62 EndY=0 EndZ=0
    g42: Circle CenterX=-44 CenterY=38 CenterZ=0 NormalX=0 NormalY=0 NormalZ=1 Radius=1.5
    g43: Circle CenterX=-44 CenterY=-38 CenterZ=0 NormalX=0 NormalY=0 NormalZ=1 Radius=1.5
    g44: LineSegment [constr] StartX=-44 StartY=38 StartZ=0 EndX=-44 EndY=-38 EndZ=0
    g45: LineSegment StartX=-29 StartY=29.5 StartZ=0 EndX=-29 EndY=-28.853 EndZ=0
    g46: Circle CenterX=52 CenterY=-6.8 CenterZ=0 NormalX=0 NormalY=0 NormalZ=1 Radius=1.5
    g47: Circle CenterX=52 CenterY=18.8 CenterZ=0 NormalX=0 NormalY=0 NormalZ=1 Radius=1.5
  constraints (125):
    c: Coincident(g0,g1)
    c: Coincident(g1,g2)
    c: Coincident(g2,g3)
    c: Coincident(g3,g0)
    c: Horizontal(g0)
    c: Horizontal(g2)
    c: Vertical(g1)
    c: Vertical(g3)
    c: DistanceX(g0) = 22.25
    c: DistanceY(g1) = -26
    c: Symmetric(g0,g2,g-1)
    c: Radius(g4) = 1.5
    c: PointOnObject(g20,g-1)
    c: Coincident(g5,g6)
    c: Coincident(g6,g7)
    c: Coincident(g7,g8)
    c: Coincident(g8,g5)
    c: Horizontal(g5)
    c: Horizontal(g7)
    c: Vertical(g6)
    c: Vertical(g8)
    c: Coincident(g9,g10)
    c: Coincident(g10,g11)
    c: Coincident(g11,g12)
    c: Coincident(g12,g9)
    c: Horizontal(g9)
    c: Horizontal(g11)
    c: Vertical(g10)
    c: Vertical(g12)
    c: DistanceX(g5) = 21
    c: DistanceY(g6) = -14
    c: Equal(g6,g10)
    c: Equal(g5,g9)
    c: Symmetric(g5,g10,g-1)
    c: Equal(g13,g14)
    c: Equal(g13,g4)
    c: Coincident(g15,g13)
    c: Coincident(g15,g14)
    c: Symmetric(g5,g5,g15)
    c: DistanceY(g15) = 20
    c: PointOnObject(g16,g6)
    c: PointOnObject(g16,g8)
    c: Symmetric(g5,g7,g16)
    c: Symmetric(g14,g13,g16)
    c: Equal(g18,g17)
    c: Equal(g17,g4)
    c: Symmetric(g17,g14,g-1)
    c: Symmetric(g18,g13,g-1)
    c: PointOnObject(g19,g16)
    c: PointOnObject(g19,g-1)
    c: Vertical(g19)
    c: PointOnObject(g19,g15)
    c: DistanceY(g19) = -28
    c: Coincident(g20,g19)
    c: DistanceX(g20) = -16.65
    c: PointOnObject(g22,g-1)
    c: Vertical(g22)
    c: Coincident(g23,g22)
    c: Vertical(g23)
    c: Coincident(g21,g22)
    c: DistanceY(g22) = 6.8
    c: Coincident(g24,g23)
    c: Equal(g24,g21)
    c: Equal(g21,g4)
    c: DistanceY(g23) = -18.8
    c: Coincident(g25,g22)
    c: DistanceX(g25) = 31.5
    c: Coincident(g25,g19)
    c: Equal(g4,g26)
    c: Coincident(g27,g26)
    c: Vertical(g27)
    c: DistanceY(g27) = -20
    c: PointOnObject(g27,g-1)
    c: Coincident(g28,g27)
    c: Coincident(g28,g22)
    c: DistanceX(g28) = 16.5
    c: Equal(g30,g29)
    c: Equal(g29,g13)
    c: Equal(g31,g26)
    c: Symmetric(g31,g26,g-1)
    c: Symmetric(g29,g30,g-1)
    c: PointOnObject(g32,g-1)
    c: Coincident(g32,g29)
    c: Vertical(g32)
    c: Equal(g32,g27)
    c: Coincident(g33,g32)
    c: Coincident(g33,g27)
    c: DistanceX(g33) = 52
    c: PointOnObject(g34,g-3)
    c: Coincident(g34,g32)
    c: Horizontal(g34)
    c: Equal(g35,g4)
    c: DistanceX(g34) = 12.5
    c: Equal(g38,g13)
    c: Equal(g36,g13)
    c: Equal(g37,g13)
    c: Equal(g39,g13)
    c: Symmetric(g38,g37,g33)
    c: Symmetric(g36,g39,g25)
    c: Coincident(g37,g40)
    c: Coincident(g40,g36)
    c: Horizontal(g40)
    c: DistanceX(g40) = 85
    c: Coincident(g41,g36)
    c: PointOnObject(g41,g25)
    c: Vertical(g41)
    c: DistanceY(g41) = -46
    c: DistanceX(g37,g-3) = -6
    c: Symmetric(g42,g43,g33)
    c: Coincident(g44,g42)
    c: Coincident(g44,g43)
    c: DistanceY(g44) = -76
    c: Equal(g42,g43)
    c: Equal(g42,g37)
    c: DistanceX(g42,g34) = 15
    c: Coincident(g45,g-3)
    c: Vertical(g45)
    c: DistanceY(g4,g20) = -16
    c: DistanceX(g4,g20) = 1.25
    c: Symmetric(g4,g35,g-1)
    c: PointOnObject(g46,g23)
    c: Equal(g46,g21)
    c: Symmetric(g21,g46,g25)
    c: Equal(g21,g47)
    c: Symmetric(g47,g23,g25)
FEATURE [PartDesign::Pocket] Pocket018  label="BASE_FINAL_[Vaciado]Taladros"
  Length = 5
  Sketch = -> Sketch038
  Type = 0
FEATURE [Part::Feature] Part__Feature200  label="TornilloM3x8_Portapilas"
  Placement = pos=(-44,-37.9,5) rot=(1,0,0;3.14159rad)
  shape: bbox 5.953 x 5.953 x 11 mm, 174 faces (baked)
FEATURE [Part::Feature] Part__Feature201  label="TornilloM3x8_Portapilas001"
  Placement = pos=(-44,37.9,5) rot=(1,0,0;3.14159rad)
  shape: bbox 5.953 x 5.953 x 11 mm, 174 faces (baked)
FEATURE [App::DocumentObjectGroup] Group032  label="Portapilas_Tornillos"
  Group = -> [Part__Feature200,Part__Feature201]
FEATURE [Part::Feature] Part__Feature202  label="TornilloM3x8_Skin"
  Placement = pos=(62,-45.9,6) rot=(1,0,0;3.14159rad)
  shape: bbox 5.953 x 5.953 x 11 mm, 174 faces (baked)
FEATURE [Part::Feature] Part__Feature203  label="TornilloM3x8_Skin001"
  Placement = pos=(-23,-45.9,6) rot=(1,0,0;3.14159rad)
  shape: bbox 5.953 x 5.953 x 11 mm, 174 faces (baked)
FEATURE [Part::Feature] Part__Feature204  label="TornilloM3x8_Skin002"
  Placement = pos=(-23,45.9,6) rot=(1,0,0;3.14159rad)
  shape: bbox 5.953 x 5.953 x 11 mm, 174 faces (baked)
FEATURE [Part::Feature] Part__Feature205  label="TornilloM3x8_Skin003"
  Placement = pos=(62,45.9,6) rot=(1,0,0;3.14159rad)
  shape: bbox 5.953 x 5.953 x 11 mm, 174 faces (baked)
FEATURE [App::DocumentObjectGroup] Group034  label="Skin_Tornillos"
  Group = -> [Part__Feature202,Part__Feature203,Part__Feature204,Part__Feature205]
FEATURE [Part::Feature] Part__Feature206  label="TuercaM3_LDR005"
  Placement = pos=(62,-46,0) rot=(0,0,1;0rad)
  shape: bbox 6.929 x 6.929 x 2.801 mm, 56 faces (baked)
FEATURE [Part::Feature] Part__Feature207  label="TuercaM3_LDR006"
  Placement = pos=(62,46,0) rot=(0,0,1;0rad)
  shape: bbox 6.929 x 6.929 x 2.801 mm, 56 faces (baked)
FEATURE [Part::Feature] Part__Feature208  label="TuercaM3_LDR007"
  Placement = pos=(-23,-46,0) rot=(0,0,1;0rad)
  shape: bbox 6.929 x 6.929 x 2.801 mm, 56 faces (baked)
FEATURE [Part::Feature] Part__Feature209  label="TuercaM3_LDR008"
  Placement = pos=(-23,46,0) rot=(0,0,1;0rad)
  shape: bbox 6.929 x 6.929 x 2.801 mm, 56 faces (baked)
FEATURE [App::DocumentObjectGroup] Group035  label="Skin-Tuercas"
  Group = -> [Part__Feature206,Part__Feature207,Part__Feature208,Part__Feature209]
FEATURE [App::DocumentObjectGroup] Group033  label="Skin"
  Group = -> [Group034,Group035]
FEATURE [Sketcher::SketchObject] Sketch039  label="[Croquis]_Guardabarros"
  Placement = pos=(0,-40,0) rot=(1,0,0;1.5708rad)
  sketch-geometry (15):
    g0: LineSegment [constr] StartX=19.5 StartY=13.5 StartZ=0 EndX=19.5 EndY=0 EndZ=0
    g1: ArcOfCircle CenterX=19.5 CenterY=13.5 CenterZ=0 NormalX=0 NormalY=0 NormalZ=1 Radius=35 StartAngle=1.5708 EndAngle=3.14159
    g2: LineSegment StartX=-15.5 StartY=13.5002 StartZ=0 EndX=-15.5 EndY=9.40739 EndZ=0
    g3: ArcOfCircle CenterX=19.5 CenterY=13.5 CenterZ=0 NormalX=0 NormalY=0 NormalZ=1 Radius=38 StartAngle=1.5708 EndAngle=3.14159
    g4: LineSegment [constr] StartX=-18.5 StartY=13.5002 StartZ=0 EndX=-15.5 EndY=13.5002 EndZ=0
    g5: LineSegment StartX=-18.5 StartY=13.5002 StartZ=0 EndX=-18.5 EndY=9.40739 EndZ=0
    g6: LineSegment StartX=-21.9104 StartY=6 StartZ=0 EndX=-30.5 EndY=6 EndZ=0
    g7: LineSegment StartX=-30.5 StartY=6 StartZ=0 EndX=-30.5 EndY=3 EndZ=0
    g8: LineSegment StartX=-30.5 StartY=3 StartZ=0 EndX=-21.9033 EndY=3 EndZ=0
    g9: ArcOfCircle CenterX=-21.9074 CenterY=9.40742 CenterZ=0 NormalX=0 NormalY=0 NormalZ=1 Radius=6.40742 StartAngle=4.71304 EndAngle=6.28318
    g10: ArcOfCircle CenterX=-21.9074 CenterY=9.40742 CenterZ=0 NormalX=0 NormalY=0 NormalZ=1 Radius=3.40742 StartAngle=4.7115 EndAngle=6.28318
    g11: LineSegment [constr] StartX=-18.5 StartY=9.40739 StartZ=0 EndX=-15.5 EndY=9.40739 EndZ=0
    g12: LineSegment [constr] StartX=19.5 StartY=13.5 StartZ=0 EndX=19.5 EndY=48.5 EndZ=0
    g13: LineSegment [constr] StartX=19.5 StartY=48.5 StartZ=0 EndX=19.5 EndY=51.5 EndZ=0
    g14: LineSegment StartX=19.5 StartY=51.5 StartZ=0 EndX=19.5 EndY=48.5 EndZ=0
  constraints (40):
    c: Vertical(g0)
    c: DistanceX(g-1,g0) = 19.5
    c: DistanceY(g-1,g0) = 13.5
    c: PointOnObject(g0,g-1)
    c: Coincident(g1,g0)
    c: Radius(g1) = 35
    c: Coincident(g2,g1)
    c: Vertical(g2)
    c: Coincident(g3,g0)
    c: Radius(g3) = 38
    c: Coincident(g4,g3)
    c: Coincident(g4,g1)
    c: Horizontal(g4)
    c: Coincident(g5,g3)
    c: Vertical(g5)
    c: Horizontal(g6)
    c: Coincident(g6,g7)
    c: Vertical(g7)
    c: Coincident(g7,g8)
    c: Horizontal(g8)
    c: DistanceY(g7) = -3
    c: DistanceY(g-1,g7) = 3
    c: Coincident(g9,g8)
    c: Coincident(g9,g2)
    c: DistanceX(g6,g0) = 50
    c: Coincident(g10,g6)
    c: Coincident(g10,g5)
    c: Coincident(g11,g5)
    c: Coincident(g11,g2)
    c: Horizontal(g11)
    c: Coincident(g9,g10)
    c: Coincident(g12,g0)
    c: Vertical(g12)
    c: Coincident(g1,g12)
    c: Coincident(g13,g1)
    c: Coincident(g13,g3)
    c: Vertical(g13)
    c: Tangent(g10,g5)
    c: Coincident(g14,g3)
    c: Coincident(g14,g1)
FEATURE [PartDesign::Pad] Pad011  label="[Extrusion]_Guardabarros_2]"
  Length = 12
  Length2 = 100
  Placement = pos=(0,-40,0) rot=(1,0,0;1.5708rad)
  Sketch = -> Sketch039
  Type = 0
FEATURE [Part::Cylinder] Cylinder049  label="Taladro-Guardabarros_2"
  Angle = 360
  Height = 10
  Placement = pos=(-23,-46,0) rot=(0,0,1;0rad)
  Radius = 1.75
FEATURE [Part::Cylinder] Cylinder050  label="Taladro_Guardabarros_1"
  Angle = 360
  Height = 10
  Placement = pos=(62,-46,0) rot=(0,0,1;0rad)
  Radius = 1.75
FEATURE [Part::MultiFuse] Fusion051  label="Taladros_Guardabarros"
  Shapes = -> [Cylinder050,Cylinder049]
FEATURE [Part::Cylinder] Cylinder051  label="Cilindro_Resta_Ultrasonido001"
  Angle = 360
  Height = 10
  Placement = pos=(53,0,29) rot=(0,0,1;0rad)
  Radius = 4.6
FEATURE [Part::Box] Box041  label="Cubo_Resta_Ultrasonido001"
  Height = 10
  Length = 11
  Placement = pos=(41,-5,29) rot=(0,0,1;0rad)
  Width = 10
FEATURE [Part::Cut] Cut051  label="[Diferencia]_Ultrasonido_Cubo_Cilindro001"
  Base = -> Box041
  Placement = pos=(1,0.1,0) rot=(0,0,1;0rad)
  Tool = -> Cylinder051
FEATURE [Part::Cut] Cut052  label="SUJETA_ULTRASONIDO--[Diferencia]_Ultrasonido_Huecos"
  Base = -> Cut032
  Tool = -> Cut051
FEATURE [Part::Feature] Cut053_solid001  label="Cut053 (Solid)001"
  Placement = pos=(-23,-20,6) rot=(0,0,1;0rad)
  shape: bbox 20 x 5.903 x 1.3 mm, 4 faces (baked)
FEATURE [Part::Feature] Cut053_solid  label="Cut053 (Solid)002"
  Placement = pos=(-23,20,6) rot=(0,0,1;0rad)
  shape: bbox 20 x 5.903 x 1.3 mm, 4 faces (baked)
FEATURE [Part::Feature] Cut053_solid002  label="Cut053 (Solid)003"
  Placement = pos=(-30,-18.75,27) rot=(0,0,1;0rad)
  shape: bbox 20 x 5.903 x 1.3 mm, 4 faces (baked)
FEATURE [Part::Feature] Cut053_solid003  label="Cut053 (Solid)004"
  Placement = pos=(-30,9,26.75) rot=(0,0,1;0rad)
  shape: bbox 20 x 5.903 x 1.3 mm, 4 faces (baked)
FEATURE [Part::Feature] Cut053_solid004  label="Cut053 (Solid)005"
  Placement = pos=(-85,24.4,27) rot=(0,0,1;0rad)
  shape: bbox 20 x 5.903 x 1.3 mm, 4 faces (baked)
FEATURE [Part::Feature] Cut053_solid005  label="Cut053 (Solid)006"
  Placement = pos=(-85,-24,27) rot=(0,0,1;0rad)
  shape: bbox 20 x 5.903 x 1.3 mm, 4 faces (baked)
FEATURE [Part::Feature] Cut053_solid006  label="Cut053 (Solid)007"
  Placement = pos=(-85,-20,6) rot=(0,0,1;0rad)
  shape: bbox 20 x 5.903 x 1.3 mm, 4 faces (baked)
FEATURE [Part::Feature] Cut053_solid007  label="Cut053 (Solid)008"
  Placement = pos=(-85,20,6) rot=(0,0,1;0rad)
  shape: bbox 20 x 5.903 x 1.3 mm, 4 faces (baked)
FEATURE [Part::MultiFuse] Fusion053
  Shapes = -> [Cut053_solid007,Cut053_solid001,Cut053_solid005,Cut053_solid006,Cut053_solid003,Cut053_solid002,Cut053_solid,Cut053_solid004]
FEATURE [Sketcher::SketchObject] Sketch042  label="servo-doc-sketch"
  Placement = pos=(3,12,30) rot=(0,0,1;3.14159rad)
  sketch-geometry (16):
    g0: LineSegment StartX=9.5 StartY=13.5 StartZ=0 EndX=-9.5 EndY=13.5 EndZ=0
    g1: LineSegment StartX=-9.5 StartY=13.5 StartZ=0 EndX=-9.5 EndY=27 EndZ=0
    g2: LineSegment StartX=-9.5 StartY=27 StartZ=0 EndX=-14 EndY=27 EndZ=0
    g3: LineSegment StartX=-14 StartY=27 StartZ=0 EndX=-14 EndY=28.5 EndZ=0
    g4: LineSegment StartX=-6 StartY=31.5 StartZ=0 EndX=-6 EndY=34 EndZ=0
    g5: LineSegment StartX=-6 StartY=34 StartZ=0 EndX=-3.7 EndY=34 EndZ=0
    g6: LineSegment StartX=-3.7 StartY=34 StartZ=0 EndX=-3.7 EndY=31.5 EndZ=0
    g7: LineSegment StartX=-3.7 StartY=31.5 StartZ=0 EndX=6.5 EndY=31.5 EndZ=0
    g8: LineSegment StartX=6.5 StartY=31.5 StartZ=0 EndX=9.5 EndY=28.5 EndZ=0
    g9: LineSegment StartX=9.5 StartY=28.5 StartZ=0 EndX=14 EndY=28.5 EndZ=0
    g10: LineSegment StartX=14 StartY=28.5 StartZ=0 EndX=14 EndY=27 EndZ=0
    g11: LineSegment StartX=14 StartY=27 StartZ=0 EndX=9.5 EndY=27 EndZ=0
    g12: LineSegment StartX=9.5 StartY=27 StartZ=0 EndX=9.5 EndY=13.5 EndZ=0
    g13: LineSegment StartX=-14 StartY=28.5 StartZ=0 EndX=-9.5 EndY=28.5 EndZ=0
    g14: LineSegment StartX=-9.5 StartY=28.5 StartZ=0 EndX=-9.5 EndY=31.5 EndZ=0
    g15: LineSegment StartX=-9.5 StartY=31.5 StartZ=0 EndX=-6 EndY=31.5 EndZ=0
  constraints (47):
    c: Horizontal(g0)
    c: Coincident(g0,g1)
    c: Vertical(g1)
    c: Coincident(g1,g2)
    c: Horizontal(g2)
    c: Coincident(g2,g3)
    c: Coincident(g4,g5)
    c: Horizontal(g5)
    c: Coincident(g5,g6)
    c: Vertical(g6)
    c: Coincident(g6,g7)
    c: Horizontal(g7)
    c: Coincident(g7,g8)
    c: Coincident(g8,g9)
    c: Horizontal(g9)
    c: Coincident(g9,g10)
    c: Coincident(g10,g11)
    c: Horizontal(g11)
    c: Coincident(g11,g12)
    c: Coincident(g12,g0)
    c: Vertical(g12)
    c: Symmetric(g0,g0,g-2)
    c: Vertical(g3)
    c: Coincident(g3,g13)
    c: Horizontal(g13)
    c: Coincident(g13,g14)
    c: Coincident(g14,g15)
    c: Coincident(g15,g4)
    c: Horizontal(g15)
    c: Symmetric(g1,g11,g-2)
    c: Symmetric(g3,g9,g-2)
    c: PointOnObject(g4,g7)
    c: Vertical(g4)
    c: Vertical(g14)
    c: PointOnObject(g13,g1)
    c: PointOnObject(g8,g12)
    c: Vertical(g10)
    c: Angle(g8,g-1) = 0.785398
    c: DistanceX(g0) = -19
    c: DistanceY(g14,g0) = -18
    c: DistanceY(g14) = 3
    c: DistanceX(g2) = -4.5
    c: DistanceY(g3) = 1.5
    c: DistanceY(g6) = -2.5
    c: DistanceX(g5) = 2.3
    c: DistanceX(g15) = 3.5
    c: DistanceY(g-1,g0) = 13.5
FEATURE [PartDesign::Pad] Pad013
  Length = 0.5
  Length2 = 100
  Placement = pos=(3,12,30) rot=(0,0,1;3.14159rad)
  Sketch = -> Sketch042
  Type = 0
FEATURE [Sketcher::SketchObject] Sketch043  label="servo-doc-sketch001"
  Placement = pos=(3,-12,30.5) rot=(0,1,0;3.14159rad)
  sketch-geometry (16):
    g0: LineSegment StartX=9.5 StartY=13.5 StartZ=0 EndX=-9.5 EndY=13.5 EndZ=0
    g1: LineSegment StartX=-9.5 StartY=13.5 StartZ=0 EndX=-9.5 EndY=27 EndZ=0
    g2: LineSegment StartX=-9.5 StartY=27 StartZ=0 EndX=-14 EndY=27 EndZ=0
    g3: LineSegment StartX=-14 StartY=27 StartZ=0 EndX=-14 EndY=28.5 EndZ=0
    g4: LineSegment StartX=-6 StartY=31.5 StartZ=0 EndX=-6 EndY=34 EndZ=0
    g5: LineSegment StartX=-6 StartY=34 StartZ=0 EndX=-3.7 EndY=34 EndZ=0
    g6: LineSegment StartX=-3.7 StartY=34 StartZ=0 EndX=-3.7 EndY=31.5 EndZ=0
    g7: LineSegment StartX=-3.7 StartY=31.5 StartZ=0 EndX=6.5 EndY=31.5 EndZ=0
    g8: LineSegment StartX=6.5 StartY=31.5 StartZ=0 EndX=9.5 EndY=28.5 EndZ=0
    g9: LineSegment StartX=9.5 StartY=28.5 StartZ=0 EndX=14 EndY=28.5 EndZ=0
    g10: LineSegment StartX=14 StartY=28.5 StartZ=0 EndX=14 EndY=27 EndZ=0
    g11: LineSegment StartX=14 StartY=27 StartZ=0 EndX=9.5 EndY=27 EndZ=0
    g12: LineSegment StartX=9.5 StartY=27 StartZ=0 EndX=9.5 EndY=13.5 EndZ=0
    g13: LineSegment StartX=-14 StartY=28.5 StartZ=0 EndX=-9.5 EndY=28.5 EndZ=0
    g14: LineSegment StartX=-9.5 StartY=28.5 StartZ=0 EndX=-9.5 EndY=31.5 EndZ=0
    g15: LineSegment StartX=-9.5 StartY=31.5 StartZ=0 EndX=-6 EndY=31.5 EndZ=0
  constraints (47):
    c: Horizontal(g0)
    c: Coincident(g0,g1)
    c: Vertical(g1)
    c: Coincident(g1,g2)
    c: Horizontal(g2)
    c: Coincident(g2,g3)
    c: Coincident(g4,g5)
    c: Horizontal(g5)
    c: Coincident(g5,g6)
    c: Vertical(g6)
    c: Coincident(g6,g7)
    c: Horizontal(g7)
    c: Coincident(g7,g8)
    c: Coincident(g8,g9)
    c: Horizontal(g9)
    c: Coincident(g9,g10)
    c: Coincident(g10,g11)
    c: Horizontal(g11)
    c: Coincident(g11,g12)
    c: Coincident(g12,g0)
    c: Vertical(g12)
    c: Symmetric(g0,g0,g-2)
    c: Vertical(g3)
    c: Coincident(g3,g13)
    c: Horizontal(g13)
    c: Coincident(g13,g14)
    c: Coincident(g14,g15)
    c: Coincident(g15,g4)
    c: Horizontal(g15)
    c: Symmetric(g1,g11,g-2)
    c: Symmetric(g3,g9,g-2)
    c: PointOnObject(g4,g7)
    c: Vertical(g4)
    c: Vertical(g14)
    c: PointOnObject(g13,g1)
    c: PointOnObject(g8,g12)
    c: Vertical(g10)
    c: Angle(g8,g-1) = 0.785398
    c: DistanceX(g0) = -19
    c: DistanceY(g14,g0) = -18
    c: DistanceY(g14) = 3
    c: DistanceX(g2) = -4.5
    c: DistanceY(g3) = 1.5
    c: DistanceY(g6) = -2.5
    c: DistanceX(g5) = 2.3
    c: DistanceX(g15) = 3.5
    c: DistanceY(g-1,g0) = 13.5
FEATURE [PartDesign::Pad] Pad014
  Length = 0.5
  Length2 = 100
  Placement = pos=(3,-12,30.5) rot=(0,1,0;3.14159rad)
  Sketch = -> Sketch043
  Type = 0
FEATURE [Part::MultiFuse] Fusion054  label="Huellas_posicion_servos"
  Placement = pos=(-4,0,0) rot=(0,0,1;0rad)
  Shapes = -> [Pad014,Pad013]
FEATURE [Sketcher::SketchObject] Sketch044
  ExternalGeometry = -> [Fillet010]
  Placement = pos=(0,-12,-1) rot=(1,0,0;1.5708rad)
  Support = -> Fillet010 [Face20]
  sketch-geometry (7):
    g0: LineSegment StartX=54.3 StartY=19.95 StartZ=0 EndX=54.3 EndY=17.95 EndZ=0
    g1: LineSegment StartX=54.3 StartY=17.95 StartZ=0 EndX=60.3 EndY=17.95 EndZ=0
    g2: LineSegment StartX=60.3 StartY=17.95 StartZ=0 EndX=60.3 EndY=16.95 EndZ=0
    g3: LineSegment StartX=60.3 StartY=16.95 StartZ=0 EndX=62.3 EndY=18.95 EndZ=0
    g4: LineSegment StartX=62.3 StartY=18.95 StartZ=0 EndX=60.3 EndY=20.95 EndZ=0
    g5: LineSegment StartX=60.3 StartY=20.95 StartZ=0 EndX=60.3 EndY=19.95 EndZ=0
    g6: LineSegment StartX=60.3 StartY=19.95 StartZ=0 EndX=54.3 EndY=19.95 EndZ=0
  constraints (21):
    c: Vertical(g0)
    c: Coincident(g0,g1)
    c: Horizontal(g1)
    c: Coincident(g1,g2)
    c: Vertical(g2)
    c: Coincident(g2,g3)
    c: Coincident(g3,g4)
    c: Coincident(g4,g5)
    c: Vertical(g5)
    c: Coincident(g5,g6)
    c: Coincident(g0,g6)
    c: Horizontal(g6)
    c: DistanceX(g6) = -6
    c: DistanceY(g0) = -2
    c: Equal(g4,g3)
    c: Equal(g5,g2)
    c: Equal(g1,g6)
    c: Angle(g4,g3) = 1.5708
    c: DistanceY(g2) = -1
    c: DistanceX(g-3,g0) = 4
    c: DistanceY(g-3,g0) = -1.75
FEATURE [PartDesign::Pocket] Pocket020
  Length = 0.5
  Placement = pos=(0,0,-1) rot=(0,0,1;0rad)
  Sketch = -> Sketch044
  Type = 0
FEATURE [Sketcher::SketchObject] Sketch045
  Placement = pos=(0,23.9,-1) rot=(0,0.707107,0.707107;3.14159rad)
  Support = -> Pocket020 [Face14]
  sketch-geometry (7):
    g0: LineSegment StartX=-60.3 StartY=19.95 StartZ=0 EndX=-54.3 EndY=19.95 EndZ=0
    g1: LineSegment StartX=-54.3 StartY=19.95 StartZ=0 EndX=-54.3 EndY=17.95 EndZ=0
    g2: LineSegment StartX=-54.3 StartY=17.95 StartZ=0 EndX=-60.3 EndY=17.95 EndZ=0
    g3: LineSegment StartX=-60.3 StartY=17.95 StartZ=0 EndX=-60.3 EndY=16.95 EndZ=0
    g4: LineSegment StartX=-60.3 StartY=16.95 StartZ=0 EndX=-62.3 EndY=18.95 EndZ=0
    g5: LineSegment StartX=-62.3 StartY=18.95 StartZ=0 EndX=-60.3 EndY=20.95 EndZ=0
    g6: LineSegment StartX=-60.3 StartY=20.95 StartZ=0 EndX=-60.3 EndY=19.95 EndZ=0
  constraints (19):
    c: Horizontal(g0)
    c: Coincident(g0,g1)
    c: Coincident(g1,g2)
    c: Horizontal(g2)
    c: Coincident(g2,g3)
    c: Coincident(g3,g4)
    c: Coincident(g4,g5)
    c: Coincident(g5,g6)
    c: Coincident(g6,g0)
    c: Equal(g5,g4)
    c: Angle(g4,g5) = 1.5708
    c: Vertical(g6)
    c: Vertical(g3)
    c: Equal(g2,g0)
    c: Vertical(g1)
    c: DistanceY(g6) = -1
    c: DistanceX(g0) = 6
    c: DistanceY(g1) = -2
    c: Equal(g3,g6)
FEATURE [PartDesign::Pocket] Pocket021  label="[Vaciado]Huella_flecha"
  Length = 0.5
  Placement = pos=(0,0,-1) rot=(0,0,1;0rad)
  Sketch = -> Sketch045
  Type = 0
FEATURE [Sketcher::SketchObject] Sketch046  label="servo-doc-sketch002"
  Placement = pos=(53.5,6,2.5) rot=(0.57735,0.57735,0.57735;2.0944rad)
  sketch-geometry (16):
    g0: LineSegment StartX=4.75 StartY=6.75 StartZ=0 EndX=-4.75 EndY=6.75 EndZ=0
    g1: LineSegment StartX=-4.75 StartY=6.75 StartZ=0 EndX=-4.75 EndY=13.5 EndZ=0
    g2: LineSegment StartX=-4.75 StartY=13.5 StartZ=0 EndX=-7 EndY=13.5 EndZ=0
    g3: LineSegment StartX=-7 StartY=13.5 StartZ=0 EndX=-7 EndY=14.25 EndZ=0
    g4: LineSegment StartX=-3 StartY=15.75 StartZ=0 EndX=-3 EndY=17 EndZ=0
    g5: LineSegment StartX=-3 StartY=17 StartZ=0 EndX=-1.85 EndY=17 EndZ=0
    g6: LineSegment StartX=-1.85 StartY=17 StartZ=0 EndX=-1.85 EndY=15.75 EndZ=0
    g7: LineSegment StartX=-1.85 StartY=15.75 StartZ=0 EndX=3.25 EndY=15.75 EndZ=0
    g8: LineSegment StartX=3.25 StartY=15.75 StartZ=0 EndX=4.75 EndY=14.25 EndZ=0
    g9: LineSegment StartX=4.75 StartY=14.25 StartZ=0 EndX=7 EndY=14.25 EndZ=0
    g10: LineSegment StartX=7 StartY=14.25 StartZ=0 EndX=7 EndY=13.5 EndZ=0
    g11: LineSegment StartX=7 StartY=13.5 StartZ=0 EndX=4.75 EndY=13.5 EndZ=0
    g12: LineSegment StartX=4.75 StartY=13.5 StartZ=0 EndX=4.75 EndY=6.75 EndZ=0
    g13: LineSegment StartX=-7 StartY=14.25 StartZ=0 EndX=-4.75 EndY=14.25 EndZ=0
    g14: LineSegment StartX=-4.75 StartY=14.25 StartZ=0 EndX=-4.75 EndY=15.75 EndZ=0
    g15: LineSegment StartX=-4.75 StartY=15.75 StartZ=0 EndX=-3 EndY=15.75 EndZ=0
  constraints (47):
    c: Horizontal(g0)
    c: Coincident(g0,g1)
    c: Vertical(g1)
    c: Coincident(g1,g2)
    c: Horizontal(g2)
    c: Coincident(g2,g3)
    c: Coincident(g4,g5)
    c: Horizontal(g5)
    c: Coincident(g5,g6)
    c: Vertical(g6)
    c: Coincident(g6,g7)
    c: Horizontal(g7)
    c: Coincident(g7,g8)
    c: Coincident(g8,g9)
    c: Horizontal(g9)
    c: Coincident(g9,g10)
    c: Coincident(g10,g11)
    c: Horizontal(g11)
    c: Coincident(g11,g12)
    c: Coincident(g12,g0)
    c: Vertical(g12)
    c: Symmetric(g0,g0,g-2)
    c: Vertical(g3)
    c: Coincident(g3,g13)
    c: Horizontal(g13)
    c: Coincident(g13,g14)
    c: Coincident(g14,g15)
    c: Coincident(g15,g4)
    c: Horizontal(g15)
    c: Symmetric(g1,g11,g-2)
    c: Symmetric(g3,g9,g-2)
    c: PointOnObject(g4,g7)
    c: Vertical(g4)
    c: Vertical(g14)
    c: PointOnObject(g13,g1)
    c: PointOnObject(g8,g12)
    c: Vertical(g10)
    c: Angle(g8,g-1) = 0.785398
    c: DistanceX(g0) = -9.5
    c: DistanceY(g14,g0) = -9
    c: DistanceY(g14) = 1.5
    c: DistanceX(g2) = -2.25
    c: DistanceY(g3) = 0.75
    c: DistanceY(g6) = -1.25
    c: DistanceX(g5) = 1.15
    c: DistanceX(g15) = 1.75
    c: DistanceY(g-1,g0) = 6.75
FEATURE [PartDesign::Pad] Pad015
  Length = 0.5
  Length2 = 100
  Placement = pos=(53.5,6,2.5) rot=(0.57735,0.57735,0.57735;2.0944rad)
  Sketch = -> Sketch046
  Type = 0
FEATURE [Part::Cut] Cut056  label="SUJETA MINISERVO FINAL"
  Base = -> Pocket021
  Tool = -> Pad015
FEATURE [App::DocumentObjectGroup] Group024  label="Sujeta_Miniservo"
  Group = -> [Cut017,Box039,Fillet010,Pocket020,Pocket021,Pad015,Cut056]
FEATURE [Part::Fillet] Fillet031  label="BASE FINAL"
  Base = -> Pocket018
  Edges = 14 edges r=2: [Edge158,Edge160,Edge201,Edge202,Edge203,Edge204,Edge209,Edge210,Edge211,Edge212,Edge220,Edge221,Edge222,Edge223]
FEATURE [Part::Feature] Face
  shape: bbox 2e-07 x 56 x 17 mm, 1 faces, 0 solids (baked)
FEATURE [Part::Extrusion] Extrude
  Base = -> Face
  Dir = (2,0,0)
  Solid = true
FEATURE [Sketcher::SketchObject] Sketch047
  ExternalGeometry = -> [Extrude]
  Placement = pos=(70,0,0) rot=(0.57735,0.57735,0.57735;2.0944rad)
  Support = -> Extrude [Face16]
  sketch-geometry (2):
    g0: Circle CenterX=-25 CenterY=43.5 CenterZ=0 NormalX=0 NormalY=0 NormalZ=1 Radius=1.75
    g1: Circle CenterX=25 CenterY=43.5 CenterZ=0 NormalX=0 NormalY=0 NormalZ=1 Radius=1.75
  constraints (5):
    c: Radius(g0) = 1.75
    c: DistanceY(g-3,g0) = -3
    c: DistanceX(g0,g-4) = -2.9
    c: Equal(g1,g0)
    c: Symmetric(g0,g1,g-2)
FEATURE [PartDesign::Pocket] Pocket022
  Length = 5
  Sketch = -> Sketch047
  Type = 0
FEATURE [Part::MultiFuse] Fusion055  label="SUJETA_ULTRASONIDO_FINAL"
  Shapes = -> [Pocket022,Cut052]
FEATURE [PartDesign::Mirrored] Mirrored
  MirrorPlane = -> Pad011 [Face1]
  Originals = -> [Pad011]
  Placement = pos=(0,-40,0) rot=(1,0,0;1.5708rad)
FEATURE [Part::Fillet] Fillet032
  Base = -> Mirrored
  Edges = 4 edges r=5: [Edge12,Edge13,Edge30,Edge42]
FEATURE [Part::Fillet] Fillet033
  Base = -> Fillet032
  Edges = 2 edges r=1.2: [Edge30,Edge35]
FEATURE [Part::Cut] Cut057  label="GUARDABARROS_FINAL"
  Base = -> Fillet033
  Tool = -> Fusion051
FEATURE [Part::MultiFuse] Fusion056  label="Taladros_Guardabarros001"
  Shapes = -> [Cylinder050,Cylinder049]
FEATURE [Part::Fillet] Fillet034
  Base = -> Fillet032
  Edges = 2 edges r=1.2: [Edge30,Edge35]
FEATURE [Part::Cut] Cut058  label="GUARDABARROS_FINAL2"
  Base = -> Fillet034
  Placement = pos=(0,92,0) rot=(0,0,1;0rad)
  Tool = -> Fusion056
FEATURE [App::DocumentObjectGroup] Group036  label="Guardabarros"
  Group = -> [Pad011,Cut057,Cut058]
FEATURE [Part::Box] Box042  label="Sujeta_Tuerca_Base_003"
  Height = 21
  Length = 10
  Placement = pos=(-22,15,3) rot=(0,0,1;0rad)
  Width = 10
FEATURE [Part::Chamfer] Chamfer008  label="[Chaflan]_Sujeta_Tuerca_Base_004"
  Base = -> Box042
  Edges = 1 edges r=9.99: [Edge10]
  Placement = pos=(18,0,0) rot=(0,0,1;3.14159rad)
FEATURE [Part::Cylinder] Cylinder052  label="Cilindro_Ajuste_pot_1"
  Angle = 360
  Height = 10
  Placement = pos=(30,-22,13) rot=(0,1,0;1.5708rad)
  Radius = 3.5
FEATURE [Part::Cylinder] Cylinder053  label="Cilindro_Ajuste_pot_2"
  Angle = 360
  Height = 10
  Placement = pos=(30,22,13) rot=(0,1,0;1.5708rad)
  Radius = 3.5
FEATURE [Part::MultiFuse] Fusion057  label="[Fusion]_Cuerpo"
  Shapes = -> [Cut,Chamfer005,Chamfer004,Chamfer008,Box033,Box031,Chamfer003,Box023,Box029]
FEATURE [PartDesign::Pad] Pad016  label="[Extrusion]_Huella_Zumbador"
  Length = 3
  Length2 = 100
  Placement = pos=(-5,0,33) rot=(0,0,1;0rad)
  Reversed = true
  Sketch = -> Sketch028
  Type = 0
FEATURE [Part::MultiFuse] Fusion058  label="[Fusion]_Orificios_cuerpo"
  Shapes = -> [Fusion053,Fusion054,Box002,Box003,Box004,Box005,Cylinder,Cylinder002,Cylinder001,Cylinder003,Box021,Box024,Box025,Box030,Box032,Box034,Cylinder024,Cylinder025,Cylinder026,Cylinder027,Cylinder028,Cylinder029,Cylinder030,Cylinder031,Cylinder032,Cylinder033,Cylinder034,Cylinder035,Pad016,Cylinder052,Cylinder053]
FEATURE [Part::Feature] Fusion055001  label="SUJETA_ULTRASONIDO_FINAL001"
  shape: bbox 20.6 x 56 x 17 mm, 32 faces (baked)
FEATURE [Part::Fillet] Fillet035  label="SUJETA_ULTRASONIDO_FINAL002"
  Base = -> Fusion055001
  Edges = 1 edges r=1: [Edge43]
FEATURE [Sketcher::SketchObject] Sketch048
  ExternalGeometry = -> [Fillet035]
  Placement = pos=(0,0,34.5) rot=(0,0,1;0rad)
  Support = -> Fillet035 [Face18]
  sketch-geometry (1):
    g0: Circle CenterX=61 CenterY=0 CenterZ=0 NormalX=0 NormalY=0 NormalZ=1 Radius=1.25
  constraints (2):
    c: Coincident(g0,g-3)
    c: Radius(g0) = 1.25
FEATURE [PartDesign::Pocket] Pocket  label="SUJETA_ULTRASONIDO_FINAL003"
  Length = 5
  Sketch = -> Sketch048
  Type = 0
FEATURE [Part::Feature] Cut048001  label="PORTA-PORTAPILAS_FINAL[Diferencia]_Logo001"
  shape: bbox 26 x 86 x 65.42 mm, 270 faces (baked)
FEATURE [Part::MultiFuse] Fusion025  label="[Fusion]Porta-Portapilas_Cables"
  Placement = pos=(0,0,0.5) rot=(0,0,1;0rad)
  Shapes = -> [Box019,Cylinder020]
FEATURE [PartDesign::Revolution] Revolution002
  Angle = 90
  Axis = (1,0,0)
  Base = (0,0,0)
  ReferenceAxis = -> Sketch036 [H_Axis]
  Reversed = true
  Sketch = -> Sketch036
FEATURE [PartDesign::Pad] Pad017
  Length = 25
  Length2 = 100
  Placement = pos=(-66,0,0) rot=(0.57735,-0.57735,-0.57735;2.0944rad)
  Sketch = -> Sketch037
  Type = 0
FEATURE [Part::Cut] Cut048002
  Base = -> Revolution002
  Placement = pos=(34.1,-28,3.6) rot=(0,0,1;0rad)
  Tool = -> Pad017
FEATURE [Part::MultiFuse] Fusion055002
  Placement = pos=(-0.025,0,0) rot=(0,0,1;0rad)
  Shapes = -> [Cylinder048,Cylinder045]
FEATURE [Part::Fillet] Fillet036
  Base = -> Cut048002
  Edges = 2 edges r=1.5: [Edge8,Edge21]
FEATURE [Sketcher::SketchObject] Sketch049
  sketch-geometry (8):
    g0: ArcOfCircle CenterX=-85.1605 CenterY=0 CenterZ=0 NormalX=0 NormalY=0 NormalZ=1 Radius=4 StartAngle=3.14159 EndAngle=3.95469
    g1: ArcOfCircle CenterX=-96.1565 CenterY=-11.6227 CenterZ=0 NormalX=0 NormalY=0 NormalZ=1 Radius=12 StartAngle=6.26222 EndAngle=7.09628
    g2: ArcOfCircle CenterX=-78.1605 CenterY=-12 CenterZ=0 NormalX=0 NormalY=0 NormalZ=1 Radius=6 StartAngle=3.12063 EndAngle=6.30415
    g3: ArcOfCircle CenterX=-71.1605 CenterY=-7.788e-09 CenterZ=0 NormalX=0 NormalY=0 NormalZ=1 Radius=4 StartAngle=5.47009 EndAngle=6.28319
    g4: ArcOfCircle CenterX=-60.1645 CenterY=-11.6227 CenterZ=0 NormalX=0 NormalY=0 NormalZ=1 Radius=12 StartAngle=2.3285 EndAngle=3.16255
    g5: LineSegment [constr] StartX=-78.1605 StartY=0 StartZ=0 EndX=-78.1605 EndY=-18 EndZ=0
    g6: LineSegment StartX=-89.1605 StartY=0 StartZ=0 EndX=-78.1605 EndY=0 EndZ=0
    g7: LineSegment StartX=-78.1605 StartY=0 StartZ=0 EndX=-67.1605 EndY=0 EndZ=0
  constraints (27):
    c: Coincident(g1,g0)
    c: Coincident(g2,g1)
    c: Coincident(g4,g3)
    c: Coincident(g4,g2)
    c: Tangent(g1,g2)
    c: Tangent(g4,g2)
    c: Tangent(g4,g3)
    c: Tangent(g1,g0)
    c: Equal(g0,g3)
    c: Vertical(g5)
    c: Symmetric(g1,g2,g5)
    c: Symmetric(g0,g3,g5)
    c: PointOnObject(g5,g2)
    c: Coincident(g6,g0)
    c: Coincident(g6,g5)
    c: Horizontal(g6)
    c: Coincident(g7,g5)
    c: Coincident(g7,g3)
    c: Horizontal(g7)
    c: DistanceX(g7) = 11
    c: Radius(g2) = 6
    c: Perpendicular(g0,g6)
    c: DistanceY(g5) = -18
    c: Radius(g1) = 12
    c: Radius(g0) = 4
    c: PointOnObject(g5,g-1)
    c: DistanceX(g-1,g3) = -67.1605
FEATURE [Sketcher::SketchObject] Sketch050
  Placement = pos=(-66,0,0) rot=(0.57735,-0.57735,-0.57735;2.0944rad)
  sketch-geometry (6):
    g0: ArcOfCircle CenterX=14.0605 CenterY=19.4746 CenterZ=0 NormalX=0 NormalY=0 NormalZ=1 Radius=15.4747 StartAngle=3.90571 EndAngle=4.70928
    g1: ArcOfCircle CenterX=0 CenterY=6 CenterZ=0 NormalX=0 NormalY=0 NormalZ=1 Radius=4 StartAngle=0.764125 EndAngle=1.5708
    g2: LineSegment StartX=0 StartY=18 StartZ=0 EndX=18 EndY=18 EndZ=0
    g3: LineSegment StartX=18 StartY=0 StartZ=0 EndX=18 EndY=18 EndZ=0
    g4: ArcOfCircle CenterX=14 CenterY=0 CenterZ=0 NormalX=0 NormalY=0 NormalZ=1 Radius=4 StartAngle=0 EndAngle=1.56769
    g5: LineSegment StartX=0 StartY=10 StartZ=0 EndX=0 EndY=18 EndZ=0
  constraints (21):
    c: Coincident(g1,g0)
    c: Tangent(g0,g1)
    c: PointOnObject(g3,g-1)
    c: PointOnObject(g1,g-2)
    c: Perpendicular(g1,g-2)
    c: Horizontal(g2)
    c: Vertical(g3)
    c: Coincident(g2,g3)
    c: PointOnObject(g4,g-1)
    c: Coincident(g4,g0)
    c: Coincident(g4,g3)
    c: Equal(g4,g1)
    c: Radius(g4) = 4
    c: Tangent(g4,g0)
    c: DistanceY(g3) = 18
    c: PointOnObject(g5,g-2)
    c: Vertical(g5)
    c: Coincident(g1,g5)
    c: Coincident(g2,g5)
    c: DistanceX(g2) = 18
    c: DistanceY(g5) = 8
FEATURE [PartDesign::Revolution] Revolution003
  Angle = 90
  Axis = (1,0,0)
  Base = (0,0,0)
  ReferenceAxis = -> Sketch049 [H_Axis]
  Reversed = true
  Sketch = -> Sketch049
FEATURE [PartDesign::Pad] Pad018
  Length = 25
  Length2 = 100
  Placement = pos=(-66,0,0) rot=(0.57735,-0.57735,-0.57735;2.0944rad)
  Sketch = -> Sketch050
  Type = 0
FEATURE [Part::Cut] Cut048003
  Base = -> Revolution003
  Placement = pos=(34.1,-28,3.6) rot=(0,0,1;0rad)
  Tool = -> Pad018
FEATURE [Part::Fillet] Fillet037
  Base = -> Cut048003
  Edges = 2 edges r=1.5: [Edge8,Edge21]
FEATURE [Part::Cut] Cut048004  label="Rail_superior"
  Base = -> Fillet036
  Placement = pos=(-0.05,0,0) rot=(0,0,1;0rad)
  Tool = -> Fusion055002
FEATURE [Part::Cylinder] Cylinder054  label="Cylinder058"
  Angle = 360
  Height = 10
  Placement = pos=(-44,-38,-2) rot=(0,0,1;0rad)
  Radius = 1.75
FEATURE [Sketcher::SketchObject] Sketch051
  Placement = pos=(-44,-38,13) rot=(0,0,1;0rad)
  sketch-geometry (7):
    g0: LineSegment StartX=-1.65 StartY=2.85788 StartZ=0 EndX=-3.3 EndY=0 EndZ=0
    g1: LineSegment StartX=-3.3 StartY=0 StartZ=0 EndX=-1.65 EndY=-2.85788 EndZ=0
    g2: LineSegment StartX=-1.65 StartY=-2.85788 StartZ=0 EndX=1.65 EndY=-2.85788 EndZ=0
    g3: LineSegment StartX=1.65 StartY=-2.85788 StartZ=0 EndX=3.3 EndY=0 EndZ=0
    g4: LineSegment StartX=3.3 StartY=0 StartZ=0 EndX=1.65 EndY=2.85788 EndZ=0
    g5: LineSegment StartX=1.65 StartY=2.85788 StartZ=0 EndX=-1.65 EndY=2.85788 EndZ=0
    g6: Circle [constr] CenterX=0 CenterY=0 CenterZ=0 NormalX=0 NormalY=0 NormalZ=1 Radius=3.3
  constraints (17):
    c: Coincident(g0,g1)
    c: Coincident(g1,g2)
    c: Coincident(g2,g3)
    c: Coincident(g3,g4)
    c: Coincident(g4,g5)
    c: Coincident(g5,g0)
    c: Equal(g0, g1-g5) x5
    c: PointOnObject(g0,g6)
    c: PointOnObject(g1,g6)
    c: PointOnObject(g2,g6)
    c: PointOnObject(g3,g6)
    c: PointOnObject(g4,g6)
    c: PointOnObject(g5,g6)
    c: Coincident(g3,g-1)
    c: Radius(g6) = 3.3
    c: Horizontal(g5)
    c: Coincident(g6,g-1)
FEATURE [PartDesign::Pad] Pad019
  Length = 8
  Length2 = 100
  Placement = pos=(-44,-38,13) rot=(0,0,1;0rad)
  Reversed = true
  Sketch = -> Sketch051
  Type = 0
FEATURE [Part::MultiFuse] Fusion055003
  Placement = pos=(-0.075,0,0) rot=(0,0,1;0rad)
  Shapes = -> [Pad019,Cylinder054]
FEATURE [Part::Cut] Cut048005  label="Rail_inferior"
  Base = -> Fillet037
  Placement = pos=(-88.15,0,3.5) rot=(0,1,0;3.14159rad)
  Tool = -> Fusion055003
FEATURE [Part::MultiFuse] Fusion055004  label="Rail_izquierdo"
  Shapes = -> [Cut048004,Cut048005]
FEATURE [Sketcher::SketchObject] Sketch052
  sketch-geometry (8):
    g0: ArcOfCircle CenterX=-85.1605 CenterY=0 CenterZ=0 NormalX=0 NormalY=0 NormalZ=1 Radius=4 StartAngle=3.14159 EndAngle=3.95469
    g1: ArcOfCircle CenterX=-96.1565 CenterY=-11.6227 CenterZ=0 NormalX=0 NormalY=0 NormalZ=1 Radius=12 StartAngle=6.26222 EndAngle=7.09628
    g2: ArcOfCircle CenterX=-78.1605 CenterY=-12 CenterZ=0 NormalX=0 NormalY=0 NormalZ=1 Radius=6 StartAngle=3.12063 EndAngle=6.30415
    g3: ArcOfCircle CenterX=-71.1605 CenterY=-7.788e-09 CenterZ=0 NormalX=0 NormalY=0 NormalZ=1 Radius=4 StartAngle=5.47009 EndAngle=6.28319
    g4: ArcOfCircle CenterX=-60.1645 CenterY=-11.6227 CenterZ=0 NormalX=0 NormalY=0 NormalZ=1 Radius=12 StartAngle=2.3285 EndAngle=3.16255
    g5: LineSegment [constr] StartX=-78.1605 StartY=0 StartZ=0 EndX=-78.1605 EndY=-18 EndZ=0
    g6: LineSegment StartX=-89.1605 StartY=0 StartZ=0 EndX=-78.1605 EndY=0 EndZ=0
    g7: LineSegment StartX=-78.1605 StartY=0 StartZ=0 EndX=-67.1605 EndY=0 EndZ=0
  constraints (27):
    c: Coincident(g1,g0)
    c: Coincident(g2,g1)
    c: Coincident(g4,g3)
    c: Coincident(g4,g2)
    c: Tangent(g1,g2)
    c: Tangent(g4,g2)
    c: Tangent(g4,g3)
    c: Tangent(g1,g0)
    c: Equal(g0,g3)
    c: Vertical(g5)
    c: Symmetric(g1,g2,g5)
    c: Symmetric(g0,g3,g5)
    c: PointOnObject(g5,g2)
    c: Coincident(g6,g0)
    c: Coincident(g6,g5)
    c: Horizontal(g6)
    c: Coincident(g7,g5)
    c: Coincident(g7,g3)
    c: Horizontal(g7)
    c: DistanceX(g7) = 11
    c: Radius(g2) = 6
    c: Perpendicular(g0,g6)
    c: DistanceY(g5) = -18
    c: Radius(g1) = 12
    c: Radius(g0) = 4
    c: PointOnObject(g5,g-1)
    c: DistanceX(g-1,g3) = -67.1605
FEATURE [Sketcher::SketchObject] Sketch053
  Placement = pos=(-66,0,0) rot=(0.57735,-0.57735,-0.57735;2.0944rad)
  sketch-geometry (6):
    g0: ArcOfCircle CenterX=14.0605 CenterY=19.4746 CenterZ=0 NormalX=0 NormalY=0 NormalZ=1 Radius=15.4747 StartAngle=3.90571 EndAngle=4.70928
    g1: ArcOfCircle CenterX=0 CenterY=6 CenterZ=0 NormalX=0 NormalY=0 NormalZ=1 Radius=4 StartAngle=0.764125 EndAngle=1.5708
    g2: LineSegment StartX=0 StartY=18 StartZ=0 EndX=18 EndY=18 EndZ=0
    g3: LineSegment StartX=18 StartY=0 StartZ=0 EndX=18 EndY=18 EndZ=0
    g4: ArcOfCircle CenterX=14 CenterY=0 CenterZ=0 NormalX=0 NormalY=0 NormalZ=1 Radius=4 StartAngle=0 EndAngle=1.56769
    g5: LineSegment StartX=0 StartY=10 StartZ=0 EndX=0 EndY=18 EndZ=0
  constraints (21):
    c: Coincident(g1,g0)
    c: Tangent(g0,g1)
    c: PointOnObject(g3,g-1)
    c: PointOnObject(g1,g-2)
    c: Perpendicular(g1,g-2)
    c: Horizontal(g2)
    c: Vertical(g3)
    c: Coincident(g2,g3)
    c: PointOnObject(g4,g-1)
    c: Coincident(g4,g0)
    c: Coincident(g4,g3)
    c: Equal(g4,g1)
    c: Radius(g4) = 4
    c: Tangent(g4,g0)
    c: DistanceY(g3) = 18
    c: PointOnObject(g5,g-2)
    c: Vertical(g5)
    c: Coincident(g1,g5)
    c: Coincident(g2,g5)
    c: DistanceX(g2) = 18
    c: DistanceY(g5) = 8
FEATURE [Part::Cylinder] Cylinder055  label="Cylinder062"
  Angle = 360
  Height = 10
  Placement = pos=(-44,-38,-2) rot=(0,0,1;0rad)
  Radius = 1.75
FEATURE [Part::Cylinder] Cylinder056  label="Cylinder060"
  Angle = 360
  Height = 8
  Placement = pos=(-44,-38,5) rot=(0,0,1;0rad)
  Radius = 2.75
FEATURE [PartDesign::Revolution] Revolution004
  Angle = 90
  Axis = (1,0,0)
  Base = (0,0,0)
  ReferenceAxis = -> Sketch052 [H_Axis]
  Reversed = true
  Sketch = -> Sketch052
FEATURE [PartDesign::Pad] Pad020
  Length = 25
  Length2 = 100
  Placement = pos=(-66,0,0) rot=(0.57735,-0.57735,-0.57735;2.0944rad)
  Sketch = -> Sketch053
  Type = 0
FEATURE [Part::Cut] Cut048006
  Base = -> Revolution004
  Placement = pos=(34.1,-28,3.6) rot=(0,0,1;0rad)
  Tool = -> Pad020
FEATURE [Part::MultiFuse] Fusion055005
  Placement = pos=(-0.025,0,0) rot=(0,0,1;0rad)
  Shapes = -> [Cylinder056,Cylinder055]
FEATURE [Part::Fillet] Fillet038
  Base = -> Cut048006
  Edges = 2 edges r=1.5: [Edge8,Edge21]
FEATURE [Sketcher::SketchObject] Sketch054
  sketch-geometry (8):
    g0: ArcOfCircle CenterX=-85.1605 CenterY=0 CenterZ=0 NormalX=0 NormalY=0 NormalZ=1 Radius=4 StartAngle=3.14159 EndAngle=3.95469
    g1: ArcOfCircle CenterX=-96.1565 CenterY=-11.6227 CenterZ=0 NormalX=0 NormalY=0 NormalZ=1 Radius=12 StartAngle=6.26222 EndAngle=7.09628
    g2: ArcOfCircle CenterX=-78.1605 CenterY=-12 CenterZ=0 NormalX=0 NormalY=0 NormalZ=1 Radius=6 StartAngle=3.12063 EndAngle=6.30415
    g3: ArcOfCircle CenterX=-71.1605 CenterY=-7.788e-09 CenterZ=0 NormalX=0 NormalY=0 NormalZ=1 Radius=4 StartAngle=5.47009 EndAngle=6.28319
    g4: ArcOfCircle CenterX=-60.1645 CenterY=-11.6227 CenterZ=0 NormalX=0 NormalY=0 NormalZ=1 Radius=12 StartAngle=2.3285 EndAngle=3.16255
    g5: LineSegment [constr] StartX=-78.1605 StartY=0 StartZ=0 EndX=-78.1605 EndY=-18 EndZ=0
    g6: LineSegment StartX=-89.1605 StartY=0 StartZ=0 EndX=-78.1605 EndY=0 EndZ=0
    g7: LineSegment StartX=-78.1605 StartY=0 StartZ=0 EndX=-67.1605 EndY=0 EndZ=0
  constraints (27):
    c: Coincident(g1,g0)
    c: Coincident(g2,g1)
    c: Coincident(g4,g3)
    c: Coincident(g4,g2)
    c: Tangent(g1,g2)
    c: Tangent(g4,g2)
    c: Tangent(g4,g3)
    c: Tangent(g1,g0)
    c: Equal(g0,g3)
    c: Vertical(g5)
    c: Symmetric(g1,g2,g5)
    c: Symmetric(g0,g3,g5)
    c: PointOnObject(g5,g2)
    c: Coincident(g6,g0)
    c: Coincident(g6,g5)
    c: Horizontal(g6)
    c: Coincident(g7,g5)
    c: Coincident(g7,g3)
    c: Horizontal(g7)
    c: DistanceX(g7) = 11
    c: Radius(g2) = 6
    c: Perpendicular(g0,g6)
    c: DistanceY(g5) = -18
    c: Radius(g1) = 12
    c: Radius(g0) = 4
    c: PointOnObject(g5,g-1)
    c: DistanceX(g-1,g3) = -67.1605
FEATURE [Sketcher::SketchObject] Sketch055
  Placement = pos=(-66,0,0) rot=(0.57735,-0.57735,-0.57735;2.0944rad)
  sketch-geometry (6):
    g0: ArcOfCircle CenterX=14.0605 CenterY=19.4746 CenterZ=0 NormalX=0 NormalY=0 NormalZ=1 Radius=15.4747 StartAngle=3.90571 EndAngle=4.70928
    g1: ArcOfCircle CenterX=0 CenterY=6 CenterZ=0 NormalX=0 NormalY=0 NormalZ=1 Radius=4 StartAngle=0.764125 EndAngle=1.5708
    g2: LineSegment StartX=0 StartY=18 StartZ=0 EndX=18 EndY=18 EndZ=0
    g3: LineSegment StartX=18 StartY=0 StartZ=0 EndX=18 EndY=18 EndZ=0
    g4: ArcOfCircle CenterX=14 CenterY=0 CenterZ=0 NormalX=0 NormalY=0 NormalZ=1 Radius=4 StartAngle=0 EndAngle=1.56769
    g5: LineSegment StartX=0 StartY=10 StartZ=0 EndX=0 EndY=18 EndZ=0
  constraints (21):
    c: Coincident(g1,g0)
    c: Tangent(g0,g1)
    c: PointOnObject(g3,g-1)
    c: PointOnObject(g1,g-2)
    c: Perpendicular(g1,g-2)
    c: Horizontal(g2)
    c: Vertical(g3)
    c: Coincident(g2,g3)
    c: PointOnObject(g4,g-1)
    c: Coincident(g4,g0)
    c: Coincident(g4,g3)
    c: Equal(g4,g1)
    c: Radius(g4) = 4
    c: Tangent(g4,g0)
    c: DistanceY(g3) = 18
    c: PointOnObject(g5,g-2)
    c: Vertical(g5)
    c: Coincident(g1,g5)
    c: Coincident(g2,g5)
    c: DistanceX(g2) = 18
    c: DistanceY(g5) = 8
FEATURE [PartDesign::Revolution] Revolution005
  Angle = 90
  Axis = (1,0,0)
  Base = (0,0,0)
  ReferenceAxis = -> Sketch054 [H_Axis]
  Reversed = true
  Sketch = -> Sketch054
FEATURE [PartDesign::Pad] Pad021
  Length = 25
  Length2 = 100
  Placement = pos=(-66,0,0) rot=(0.57735,-0.57735,-0.57735;2.0944rad)
  Sketch = -> Sketch055
  Type = 0
FEATURE [Part::Cut] Cut048007
  Base = -> Revolution005
  Placement = pos=(34.1,-28,3.6) rot=(0,0,1;0rad)
  Tool = -> Pad021
FEATURE [Part::Fillet] Fillet039
  Base = -> Cut048007
  Edges = 2 edges r=1.5: [Edge8,Edge21]
FEATURE [Part::Cut] Cut048008  label="Rail_superior001"
  Base = -> Fillet038
  Placement = pos=(-0.05,0,0) rot=(0,0,1;0rad)
  Tool = -> Fusion055005
FEATURE [Part::Cylinder] Cylinder057  label="Cylinder063"
  Angle = 360
  Height = 10
  Placement = pos=(-44,-38,-2) rot=(0,0,1;0rad)
  Radius = 1.75
FEATURE [Sketcher::SketchObject] Sketch056
  Placement = pos=(-44,-38,13) rot=(0,0,1;0rad)
  sketch-geometry (7):
    g0: LineSegment StartX=-1.65 StartY=2.85788 StartZ=0 EndX=-3.3 EndY=0 EndZ=0
    g1: LineSegment StartX=-3.3 StartY=0 StartZ=0 EndX=-1.65 EndY=-2.85788 EndZ=0
    g2: LineSegment StartX=-1.65 StartY=-2.85788 StartZ=0 EndX=1.65 EndY=-2.85788 EndZ=0
    g3: LineSegment StartX=1.65 StartY=-2.85788 StartZ=0 EndX=3.3 EndY=0 EndZ=0
    g4: LineSegment StartX=3.3 StartY=0 StartZ=0 EndX=1.65 EndY=2.85788 EndZ=0
    g5: LineSegment StartX=1.65 StartY=2.85788 StartZ=0 EndX=-1.65 EndY=2.85788 EndZ=0
    g6: Circle [constr] CenterX=0 CenterY=0 CenterZ=0 NormalX=0 NormalY=0 NormalZ=1 Radius=3.3
  constraints (17):
    c: Coincident(g0,g1)
    c: Coincident(g1,g2)
    c: Coincident(g2,g3)
    c: Coincident(g3,g4)
    c: Coincident(g4,g5)
    c: Coincident(g5,g0)
    c: Equal(g0, g1-g5) x5
    c: PointOnObject(g0,g6)
    c: PointOnObject(g1,g6)
    c: PointOnObject(g2,g6)
    c: PointOnObject(g3,g6)
    c: PointOnObject(g4,g6)
    c: PointOnObject(g5,g6)
    c: Coincident(g3,g-1)
    c: Radius(g6) = 3.3
    c: Horizontal(g5)
    c: Coincident(g6,g-1)
FEATURE [PartDesign::Pad] Pad022
  Length = 8
  Length2 = 100
  Placement = pos=(-44,-38,13) rot=(0,0,1;0rad)
  Reversed = true
  Sketch = -> Sketch056
  Type = 0
FEATURE [Part::MultiFuse] Fusion055006
  Placement = pos=(-0.075,0,0) rot=(0,0,1;0rad)
  Shapes = -> [Pad022,Cylinder057]
FEATURE [Part::Cut] Cut048009  label="Rail_inferior001"
  Base = -> Fillet039
  Placement = pos=(-88.15,0,3.5) rot=(0,1,0;3.14159rad)
  Tool = -> Fusion055006
FEATURE [Part::MultiFuse] Fusion055007  label="Rail_iderecho"
  Placement = pos=(-88,0,0) rot=(0,0,1;3.14159rad)
  Shapes = -> [Cut048008,Cut048009]
FEATURE [Part::MultiFuse] Fusion055008  label="Rueda_loca"
  Placement = pos=(0,0,2) rot=(0,0,1;0rad)
  Shapes = -> [Pad002,Revolution001,Revolution]
FEATURE [Part::MultiFuse] Fusion055009  label="Huecos_portapilas"
  Shapes = -> [Box018,bq_logo007_solid,Fusion025]
FEATURE [Part::Cut] Cut048010
  Base = -> Box017
  Tool = -> Fusion055009
FEATURE [Part::Fillet] Fillet040
  Base = -> Cut048010
  Edges = 17 edges: [Edge1 r=2,Edge2 r=2,Edge3 r=2,Edge4 r=2,Edge103 r=2,Edge104 r=1.8,Edge105 r=2,Edge106 r=2,Edge107 r=1.2,Edge108 r=1.2,Edge109 r=1.2,Edge110 r=1.2,Edge111 r=1.2,Edge112 r=2,Edge113 r=1.2,Edge114 r=1.8,Edge322 r=1.2]
FEATURE [Part::Cut] Cut048011
  Base = -> Fillet040
  Tool = -> Fusion017
FEATURE [Part::Fillet] Fillet041
  Base = -> Cut048011
  Edges = 2 edges r=2: [Edge318,Edge336]
FEATURE [Part::MultiFuse] Fusion055010  label="PORTA-PORTAPILAS_FINAL"
  Shapes = -> [Fusion055004,Fillet041,Fusion055008,Fusion055007]
FEATURE [Part::Box] Box043  label="Cubo"
  Height = 12.5
  Length = 5.95
  Placement = pos=(-57,-37,-5) rot=(0,0,1;0rad)
  Width = 2
FEATURE [Part::Box] Box044  label="Cubo001"
  Height = 12.5
  Length = 6.75
  Placement = pos=(-57,-40,-5) rot=(0,0,1;0rad)
  Width = 2
FEATURE [Part::MultiFuse] Fusion055011
  Shapes = -> [Box043,Box044]
FEATURE [Part::Box] Box045  label="Cubo002"
  Height = 12.5
  Length = 5.95
  Placement = pos=(-57,-37,-5) rot=(0,0,1;0rad)
  Width = 2
FEATURE [Part::Box] Box046  label="Cubo003"
  Height = 12.5
  Length = 6.75
  Placement = pos=(-57,-40,-5) rot=(0,0,1;0rad)
  Width = 2
FEATURE [Part::MultiFuse] Fusion055012
  Placement = pos=(0,0,3) rot=(1,0,0;3.14159rad)
  Shapes = -> [Box045,Box046]
FEATURE [Part::Cylinder] Cylinder059  label="Cylinder064"
  Angle = 360
  Height = 8
  Placement = pos=(-44,38,5) rot=(0,0,1;0rad)
  Radius = 3
FEATURE [Sketcher::SketchObject] Sketch058
  Placement = pos=(0,0,-1.45) rot=(1,0,0;3.14159rad)
  sketch-geometry (7):
    g0: LineSegment StartX=-47.5 StartY=-38 StartZ=0 EndX=-45.75 EndY=-41.0311 EndZ=0
    g1: LineSegment StartX=-45.75 StartY=-41.0311 StartZ=0 EndX=-42.25 EndY=-41.0311 EndZ=0
    g2: LineSegment StartX=-42.25 StartY=-41.0311 StartZ=0 EndX=-40.5 EndY=-38 EndZ=0
    g3: LineSegment StartX=-40.5 StartY=-38 StartZ=0 EndX=-42.25 EndY=-34.9689 EndZ=0
    g4: LineSegment StartX=-42.25 StartY=-34.9689 StartZ=0 EndX=-45.75 EndY=-34.9689 EndZ=0
    g5: LineSegment StartX=-45.75 StartY=-34.9689 StartZ=0 EndX=-47.5 EndY=-38 EndZ=0
    g6: Circle [constr] CenterX=-44 CenterY=-38 CenterZ=0 NormalX=0 NormalY=0 NormalZ=1 Radius=3.5
  constraints (17):
    c: Coincident(g0,g1)
    c: Coincident(g1,g2)
    c: Coincident(g2,g3)
    c: Coincident(g3,g4)
    c: Coincident(g4,g5)
    c: Coincident(g5,g0)
    c: Equal(g0, g1-g5) x5
    c: PointOnObject(g0,g6)
    c: PointOnObject(g1,g6)
    c: PointOnObject(g2,g6)
    c: PointOnObject(g3,g6)
    c: PointOnObject(g4,g6)
    c: PointOnObject(g5,g6)
    c: Horizontal(g4)
    c: Radius(g6) = 3.5
    c: DistanceX(g-1,g6) = -44
    c: DistanceY(g-1,g6) = -38
FEATURE [PartDesign::Pad] Pad023
  Length = 10
  Length2 = 100
  Placement = pos=(0,0,-1.45) rot=(1,0,0;3.14159rad)
  Sketch = -> Sketch058
  Type = 0
FEATURE [Part::MultiFuse] Fusion055013
  Shapes = -> [Pad023,Cylinder059]
FEATURE [Part::MultiFuse] Fusion055014  label="Soportes_Portapilas"
  Shapes = -> [Fusion055012,Fusion055011]
FEATURE [Part::Feature] Cut048014  label="[Refinado]_Cuerpo"
  shape: bbox 62 x 66 x 30 mm, 212 faces (baked)
FEATURE [Part::Cylinder] Cylinder061  label="Cylinder065"
  Angle = 360
  Height = 8
  Placement = pos=(-44,38,5) rot=(0,0,1;0rad)
  Radius = 3
FEATURE [Sketcher::SketchObject] Sketch060
  Placement = pos=(0,0,-1.45) rot=(1,0,0;3.14159rad)
  sketch-geometry (7):
    g0: LineSegment StartX=-47.5 StartY=-38 StartZ=0 EndX=-45.75 EndY=-41.0311 EndZ=0
    g1: LineSegment StartX=-45.75 StartY=-41.0311 StartZ=0 EndX=-42.25 EndY=-41.0311 EndZ=0
    g2: LineSegment StartX=-42.25 StartY=-41.0311 StartZ=0 EndX=-40.5 EndY=-38 EndZ=0
    g3: LineSegment StartX=-40.5 StartY=-38 StartZ=0 EndX=-42.25 EndY=-34.9689 EndZ=0
    g4: LineSegment StartX=-42.25 StartY=-34.9689 StartZ=0 EndX=-45.75 EndY=-34.9689 EndZ=0
    g5: LineSegment StartX=-45.75 StartY=-34.9689 StartZ=0 EndX=-47.5 EndY=-38 EndZ=0
    g6: Circle [constr] CenterX=-44 CenterY=-38 CenterZ=0 NormalX=0 NormalY=0 NormalZ=1 Radius=3.5
  constraints (17):
    c: Coincident(g0,g1)
    c: Coincident(g1,g2)
    c: Coincident(g2,g3)
    c: Coincident(g3,g4)
    c: Coincident(g4,g5)
    c: Coincident(g5,g0)
    c: Equal(g0, g1-g5) x5
    c: PointOnObject(g0,g6)
    c: PointOnObject(g1,g6)
    c: PointOnObject(g2,g6)
    c: PointOnObject(g3,g6)
    c: PointOnObject(g4,g6)
    c: PointOnObject(g5,g6)
    c: Horizontal(g4)
    c: Radius(g6) = 3.5
    c: DistanceX(g-1,g6) = -44
    c: DistanceY(g-1,g6) = -38
FEATURE [PartDesign::Pad] Pad025
  Length = 10
  Length2 = 100
  Placement = pos=(0,0,-1.45) rot=(1,0,0;3.14159rad)
  Sketch = -> Sketch060
  Type = 0
FEATURE [Part::MultiFuse] Fusion055015
  Placement = pos=(0,-76,0) rot=(0,0,1;0rad)
  Shapes = -> [Pad025,Cylinder061]
FEATURE [Part::MultiFuse] Fusion055016
  Shapes = -> [Fusion055013,Fusion055015]
FEATURE [Part::Cut] Cut048015  label="Soportes_portapilas"
  Base = -> Fusion055010
  Tool = -> Fusion055016
FEATURE [App::DocumentObjectGroup] Group023  label="Porta-Portapilas"
  Group = -> [Fusion004,Group032,Fusion055014,Cut048001,Cut048015]
FEATURE [Part::Cut] Cut048016
  Base = -> Fusion057
  Tool = -> Fusion058
FEATURE [Part::Feature] Cut048016001  label="Cut048017"
  shape: bbox 62 x 66 x 30 mm, 214 faces (baked)
FEATURE [Part::Fillet] Fillet  label="Redondeo_cuerpo"
  Base = -> Cut048016001
  Edges = 35 edges: [Edge159 r=1,Edge162 r=2,Edge164 r=2,Edge166 r=2,Edge169 r=2,Edge170 r=2,Edge171 r=2,Edge172 r=1,Edge173 r=1,Edge174 r=1,Edge175 r=1,Edge180 r=2,Edge183 r=2,Edge191 r=1,Edge192 r=1,Edge193 r=1,Edge195 r=1,Edge197 r=1,Edge204 r=1,Edge206 r=1,Edge272 r=1,Edge273 r=1,Edge274 r=1,Edge275 r=1,Edge276 r=1,Edge294 r=1,Edge295 r=1,Edge391 r=2,Edge393 r=1,Edge397 r=2,Edge403 r=1,Edge523 r=2,Edge525 r=1,Edge549 r=2,Edge550 r=1]
FEATURE [Part::Chamfer] Chamfer009  label="CUERPO_FINAL"
  Base = -> Fillet
  Edges = 30 edges r=0.4: [Edge70,Edge72,Edge74,Edge79,Edge89,Edge92,Edge96,Edge99,Edge101,Edge102,Edge104,Edge106,Edge108,Edge110,Edge112,Edge419,Edge421,Edge424,Edge426,Edge430,Edge432,Edge436,Edge438,Edge441,Edge443,Edge444,Edge446,Edge448,Edge450,Edge455]
FEATURE [App::DocumentObjectGroup] Group002  label="Cuerpo"
  Group = -> [Cut048014,Cut048016,Fillet,Chamfer009]
FEATURE [Sketcher::SketchObject] Sketch061
  ExternalGeometry = -> [Pocket]
  Placement = pos=(0,0,32.5) rot=(1,0,0;3.14159rad)
  Support = -> Pocket [Face45]
  sketch-geometry (1):
    g0: Circle CenterX=61 CenterY=-0.05 CenterZ=0 NormalX=0 NormalY=0 NormalZ=1 Radius=3.25
  constraints (2):
    c: Coincident(g0,g-3)
    c: Radius(g0) = 3.25
FEATURE [PartDesign::Pocket] Pocket023  label="Sujeta_Ultrasonido_FINAL"
  Length = 1
  Sketch = -> Sketch061
  Type = 0
FEATURE [Sketcher::SketchObject] Sketch062
  Placement = pos=(0,0,33) rot=(0,0,1;0rad)
  sketch-geometry (8):
    g0: Circle [constr] CenterX=-17 CenterY=-24 CenterZ=0 NormalX=0 NormalY=0 NormalZ=1 Radius=3
    g1: LineSegment StartX=-18.5 StartY=-21.4019 StartZ=0 EndX=-20 EndY=-24 EndZ=0
    g2: LineSegment StartX=-20 StartY=-24 StartZ=0 EndX=-18.5 EndY=-26.5981 EndZ=0
    g3: LineSegment StartX=-18.5 StartY=-26.5981 StartZ=0 EndX=-15.5 EndY=-26.5981 EndZ=0
    g4: LineSegment StartX=-15.5 StartY=-26.5981 StartZ=0 EndX=-14 EndY=-24 EndZ=0
    g5: LineSegment StartX=-14 StartY=-24 StartZ=0 EndX=-15.5 EndY=-21.4019 EndZ=0
    g6: LineSegment StartX=-15.5 StartY=-21.4019 StartZ=0 EndX=-18.5 EndY=-21.4019 EndZ=0
    g7: Circle [constr] CenterX=-17 CenterY=-24 CenterZ=0 NormalX=0 NormalY=0 NormalZ=1 Radius=3
  constraints (20):
    c: Radius(g0) = 3
    c: DistanceX(g-1,g0) = -17
    c: DistanceY(g-1,g0) = -24
    c: Coincident(g1,g2)
    c: Coincident(g2,g3)
    c: Coincident(g3,g4)
    c: Coincident(g4,g5)
    c: Coincident(g5,g6)
    c: Coincident(g6,g1)
    c: Equal(g1, g2-g6) x5
    c: PointOnObject(g1,g7)
    c: PointOnObject(g2,g7)
    c: PointOnObject(g3,g7)
    c: PointOnObject(g4,g7)
    c: PointOnObject(g5,g7)
    c: PointOnObject(g6,g7)
    c: Coincident(g4,g0)
    c: PointOnObject(g5,g0)
    c: Horizontal(g6)
    c: Coincident(g0,g7)
FEATURE [PartDesign::Pad] Pad026
  Length = 15.45
  Length2 = 100
  Placement = pos=(0,0,33) rot=(0,0,1;0rad)
  Sketch = -> Sketch062
  Type = 0
FEATURE [Part::Cut] Cut048016002  label="Separador_Hexagonal_1"
  Base = -> Pad026
  Tool = -> Cylinder005
FEATURE [Part::Feature] Cut048016002001  label="Separador_Hexagonal_2"
  Placement = pos=(52,5,0) rot=(0,0,1;0rad)
  shape: bbox 6 x 5.196 x 15.45 mm, 9 faces (baked)
FEATURE [Part::Feature] Cut048016002002  label="Separador_Hexagonal_3"
  Placement = pos=(52,33,0) rot=(0,0,1;0rad)
  shape: bbox 6 x 5.196 x 15.45 mm, 9 faces (baked)
FEATURE [Part::Feature] Cut048016002003  label="Separador_Hexagonal_4"
  Placement = pos=(1,49,0) rot=(0,0,1;0rad)
  shape: bbox 6 x 5.196 x 15.45 mm, 9 faces (baked)
FEATURE [App::DocumentObjectGroup] Group026  label="ZUM_Separadaroes"
  Group = -> [Cut048016002,Cut048016002001,Cut048016002002,Cut048016002003]
FEATURE [App::DocumentObjectGroup] Group004  label="ZUM"
  Group = -> [Part__Feature064,Group006,Group007,Group026]
FEATURE [Part::Compound] Compound004  label="Doble IR"
  Links = -> [Fusion006,Fusion005]
  Placement = pos=(22,0,0) rot=(0,0,1;0rad)
FEATURE [App::DocumentObjectGroup] Group016  label="Sensores"
  Group = -> [Group008,Group009,Fusion005,Fusion006,Fusion028,Fusion029,Compound004]
FEATURE [Part::Feature] Part__Feature210  label="BASE_FINAL"
  shape: bbox 217.5 x 140 x 48.35 mm, 110 faces (baked)
FEATURE [App::DocumentObjectGroup] Group001  label="Base"
  Group = -> [Pocket009,Pad006,Fillet026,Pad010,Pocket018,Fillet031,Part__Feature210]
FEATURE [Sketcher::SketchObject] Sketch063
  ExternalGeometry = -> [Pocket023]
  Placement = pos=(0,0,34.5) rot=(0,0,1;0rad)
  Support = -> Pocket023 [Face18]
  sketch-geometry (2):
    g0: Circle CenterX=61 CenterY=0 CenterZ=0 NormalX=0 NormalY=0 NormalZ=1 Radius=2.5
    g1: Circle CenterX=61 CenterY=0 CenterZ=0 NormalX=0 NormalY=0 NormalZ=1 Radius=1.25
  constraints (4):
    c: Coincident(g0,g-3)
    c: Coincident(g1,g0)
    c: Equal(g1,g-3)
    c: Radius(g0) = 2.5
FEATURE [PartDesign::Pad] Pad027
  Length = 1
  Length2 = 100
  Sketch = -> Sketch063
  Type = 0
FEATURE [Part::Chamfer] Chamfer010  label="Sujeta_Ultrasonido_FINAL001"
  Base = -> Pad027
  Edges = 1 edges r=0.99: [Edge118]
FEATURE [App::DocumentObjectGroup] Group025  label="Sujeta_Ultrasonido"
  Group = -> [Pad,Pocket012,Box013,Cut030,Sketch,Fusion027,Fusion045,Pocket017,Cut032,Cut051,Cut052,Extrude,Pocket022,Fusion055,Cut031,Fillet035,Pocket,Pocket023,Pad027,Chamfer010]
FEATURE [App::DocumentObjectGroup] Group012  label="Miniservo_Ultrasonido"
  Group = -> [Part__Feature078,Miniservo001,Group021,Group022,Group024,Group025]
